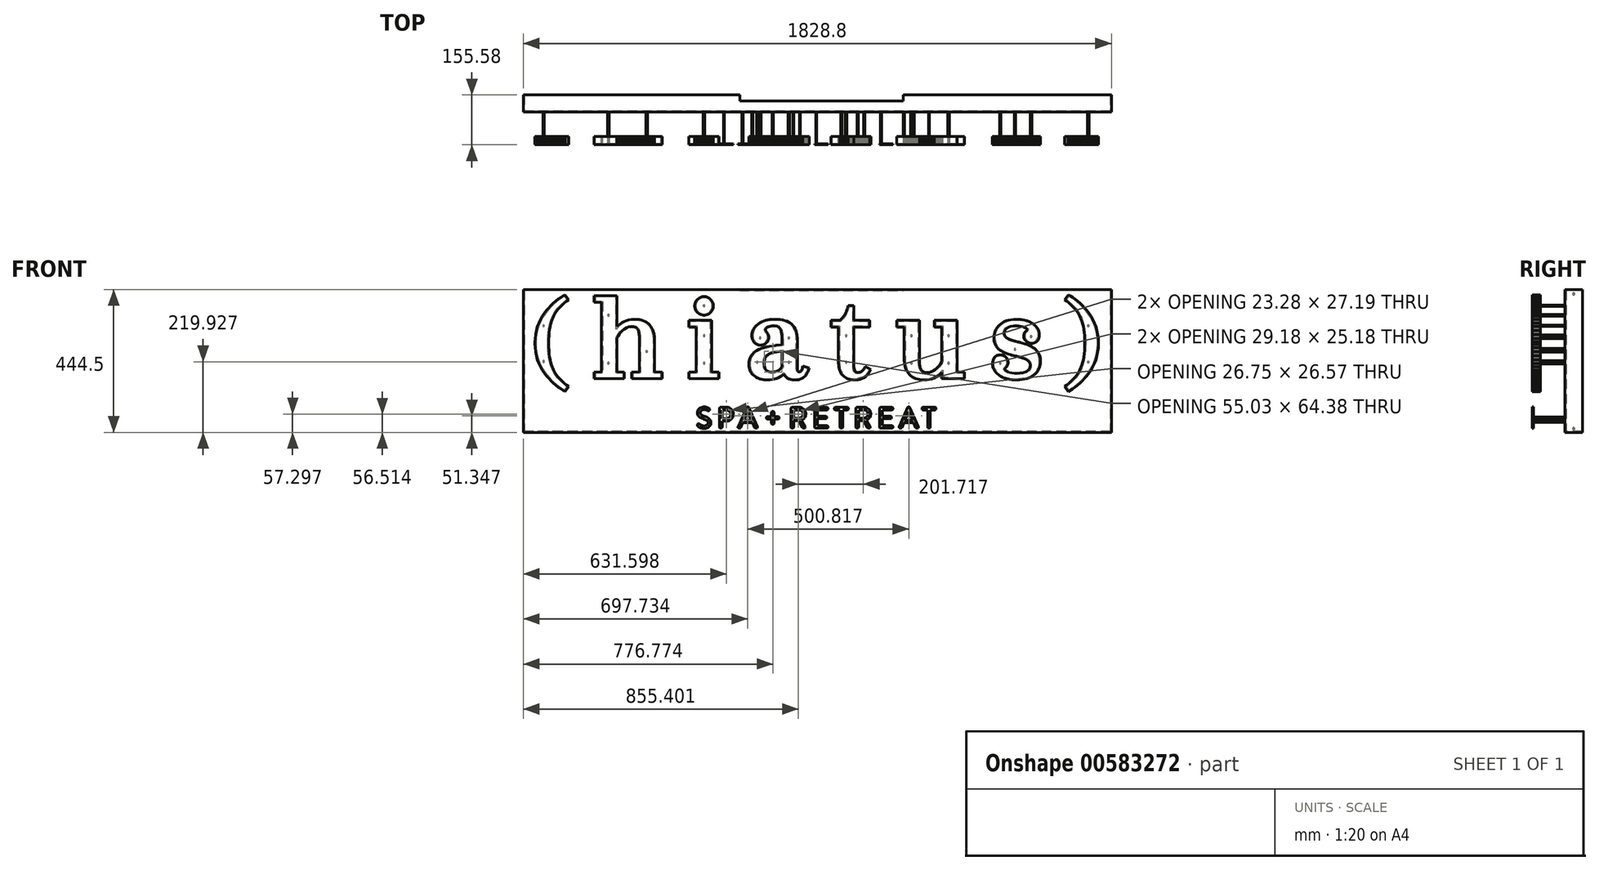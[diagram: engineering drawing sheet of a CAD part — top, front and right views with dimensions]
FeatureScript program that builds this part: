
annotation { "Feature Type Name" : "Feature", "Feature Type Description" : "" }
export const myFeature = defineFeature(function(context is Context, id is Id, definition is map)
    precondition{}
    {
        {
            var Q0;
            Q0=qCreatedBy(makeId("Front.planeOp"),FACE);
            var sketch = newSketch(context, id + "F0", { "sketchPlane" : qUnion([Q0])});
            skLineSegment(sketch, "E0", {"start": v(-821.4, -18.32) * mm, "end": v(-822.15, -16.45) * mm});
            skLineSegment(sketch, "E1", {"start": v(-822.15, -16.45) * mm, "end": v(-824.19, -10.72) * mm});
            skLineSegment(sketch, "E2", {"start": v(-824.19, -10.72) * mm, "end": v(-826.59, -2.66) * mm});
            skLineSegment(sketch, "E3", {"start": v(-826.59, -2.66) * mm, "end": v(-828.6, 5.9) * mm});
            skLineSegment(sketch, "E4", {"start": v(-828.6, 5.9) * mm, "end": v(-830.23, 14.98) * mm});
            skLineSegment(sketch, "E5", {"start": v(-830.23, 14.98) * mm, "end": v(-831.49, 24.64) * mm});
            skLineSegment(sketch, "E6", {"start": v(-831.49, 24.64) * mm, "end": v(-832.38, 34.93) * mm});
            skLineSegment(sketch, "E7", {"start": v(-832.38, 34.93) * mm, "end": v(-832.9, 45.87) * mm});
            skLineSegment(sketch, "E8", {"start": v(-832.9, 45.87) * mm, "end": v(-833.08, 54.6) * mm});
            skLineSegment(sketch, "E9", {"start": v(-833.08, 54.6) * mm, "end": v(-833.08, 57.5) * mm});
            skLineSegment(sketch, "E10", {"start": v(-833.08, 57.5) * mm, "end": v(-833.08, 60.42) * mm});
            skLineSegment(sketch, "E11", {"start": v(-833.08, 60.42) * mm, "end": v(-832.9, 69.15) * mm});
            skLineSegment(sketch, "E12", {"start": v(-832.9, 69.15) * mm, "end": v(-832.38, 80.1) * mm});
            skLineSegment(sketch, "E13", {"start": v(-832.38, 80.1) * mm, "end": v(-831.49, 90.37) * mm});
            skLineSegment(sketch, "E14", {"start": v(-831.49, 90.37) * mm, "end": v(-830.23, 100.03) * mm});
            skLineSegment(sketch, "E15", {"start": v(-830.23, 100.03) * mm, "end": v(-828.6, 109.12) * mm});
            skLineSegment(sketch, "E16", {"start": v(-828.6, 109.12) * mm, "end": v(-826.59, 117.67) * mm});
            skLineSegment(sketch, "E17", {"start": v(-826.59, 117.67) * mm, "end": v(-824.19, 125.73) * mm});
            skLineSegment(sketch, "E18", {"start": v(-824.19, 125.73) * mm, "end": v(-822.15, 131.46) * mm});
            skLineSegment(sketch, "E19", {"start": v(-822.15, 131.46) * mm, "end": v(-821.4, 133.34) * mm});
            skLineSegment(sketch, "E20", {"start": v(-821.4, 133.34) * mm, "end": v(-820.58, 135.36) * mm});
            skLineSegment(sketch, "E21", {"start": v(-820.58, 135.36) * mm, "end": v(-817.84, 141.3) * mm});
            skLineSegment(sketch, "E22", {"start": v(-817.84, 141.3) * mm, "end": v(-813.76, 148.88) * mm});
            skLineSegment(sketch, "E23", {"start": v(-813.76, 148.88) * mm, "end": v(-809.12, 156.12) * mm});
            skLineSegment(sketch, "E24", {"start": v(-809.12, 156.12) * mm, "end": v(-803.9, 163.04) * mm});
            skLineSegment(sketch, "E25", {"start": v(-803.9, 163.04) * mm, "end": v(-798.07, 169.69) * mm});
            skLineSegment(sketch, "E26", {"start": v(-798.07, 169.69) * mm, "end": v(-791.62, 176.07) * mm});
            skLineSegment(sketch, "E27", {"start": v(-791.62, 176.07) * mm, "end": v(-784.52, 182.24) * mm});
            skLineSegment(sketch, "E28", {"start": v(-784.52, 182.24) * mm, "end": v(-778.72, 186.78) * mm});
            skLineSegment(sketch, "E29", {"start": v(-778.72, 186.78) * mm, "end": v(-776.74, 188.22) * mm});
            skLineSegment(sketch, "E30", {"start": v(-776.74, 188.22) * mm, "end": v(-771.25, 192.19) * mm});
            skLineSegment(sketch, "E31", {"start": v(-771.25, 192.19) * mm, "end": v(-782.57, 208.03) * mm});
            skLineSegment(sketch, "E32", {"start": v(-782.57, 208.03) * mm, "end": v(-788, 204.63) * mm});
            skLineSegment(sketch, "E33", {"start": v(-788, 204.63) * mm, "end": v(-789.93, 203.43) * mm});
            skLineSegment(sketch, "E34", {"start": v(-789.93, 203.43) * mm, "end": v(-795.63, 199.68) * mm});
            skLineSegment(sketch, "E35", {"start": v(-795.63, 199.68) * mm, "end": v(-803.36, 194.22) * mm});
            skLineSegment(sketch, "E36", {"start": v(-803.36, 194.22) * mm, "end": v(-811.1, 188.24) * mm});
            skLineSegment(sketch, "E37", {"start": v(-811.1, 188.24) * mm, "end": v(-818.8, 181.74) * mm});
            skLineSegment(sketch, "E38", {"start": v(-818.8, 181.74) * mm, "end": v(-826.33, 174.7) * mm});
            skLineSegment(sketch, "E39", {"start": v(-826.33, 174.7) * mm, "end": v(-833.64, 167.1) * mm});
            skLineSegment(sketch, "E40", {"start": v(-833.64, 167.1) * mm, "end": v(-840.64, 158.93) * mm});
            skLineSegment(sketch, "E41", {"start": v(-840.64, 158.93) * mm, "end": v(-847.26, 150.17) * mm});
            skLineSegment(sketch, "E42", {"start": v(-847.26, 150.17) * mm, "end": v(-853.4, 140.82) * mm});
            skLineSegment(sketch, "E43", {"start": v(-853.4, 140.82) * mm, "end": v(-858.98, 130.86) * mm});
            skLineSegment(sketch, "E44", {"start": v(-858.98, 130.86) * mm, "end": v(-863.94, 120.28) * mm});
            skLineSegment(sketch, "E45", {"start": v(-863.94, 120.28) * mm, "end": v(-868.17, 109.05) * mm});
            skLineSegment(sketch, "E46", {"start": v(-868.17, 109.05) * mm, "end": v(-871.6, 97.18) * mm});
            skLineSegment(sketch, "E47", {"start": v(-871.6, 97.18) * mm, "end": v(-874.16, 84.64) * mm});
            skLineSegment(sketch, "E48", {"start": v(-874.16, 84.64) * mm, "end": v(-875.75, 71.42) * mm});
            skLineSegment(sketch, "E49", {"start": v(-875.75, 71.42) * mm, "end": v(-876.3, 60.99) * mm});
            skLineSegment(sketch, "E50", {"start": v(-876.3, 60.99) * mm, "end": v(-876.3, 57.5) * mm});
            skLineSegment(sketch, "E51", {"start": v(-876.3, 57.5) * mm, "end": v(-876.3, 54.03) * mm});
            skLineSegment(sketch, "E52", {"start": v(-876.3, 54.03) * mm, "end": v(-875.75, 43.6) * mm});
            skLineSegment(sketch, "E53", {"start": v(-875.75, 43.6) * mm, "end": v(-874.16, 30.38) * mm});
            skLineSegment(sketch, "E54", {"start": v(-874.16, 30.38) * mm, "end": v(-871.6, 17.84) * mm});
            skLineSegment(sketch, "E55", {"start": v(-871.6, 17.84) * mm, "end": v(-868.17, 5.96) * mm});
            skLineSegment(sketch, "E56", {"start": v(-868.17, 5.96) * mm, "end": v(-863.94, -5.26) * mm});
            skLineSegment(sketch, "E57", {"start": v(-863.94, -5.26) * mm, "end": v(-858.98, -15.85) * mm});
            skLineSegment(sketch, "E58", {"start": v(-858.98, -15.85) * mm, "end": v(-853.4, -25.8) * mm});
            skLineSegment(sketch, "E59", {"start": v(-853.4, -25.8) * mm, "end": v(-847.26, -35.16) * mm});
            skLineSegment(sketch, "E60", {"start": v(-847.26, -35.16) * mm, "end": v(-840.64, -43.91) * mm});
            skLineSegment(sketch, "E61", {"start": v(-840.64, -43.91) * mm, "end": v(-833.64, -52.08) * mm});
            skLineSegment(sketch, "E62", {"start": v(-833.64, -52.08) * mm, "end": v(-826.33, -59.68) * mm});
            skLineSegment(sketch, "E63", {"start": v(-826.33, -59.68) * mm, "end": v(-818.8, -66.73) * mm});
            skLineSegment(sketch, "E64", {"start": v(-818.8, -66.73) * mm, "end": v(-811.1, -73.23) * mm});
            skLineSegment(sketch, "E65", {"start": v(-811.1, -73.23) * mm, "end": v(-803.36, -79.2) * mm});
            skLineSegment(sketch, "E66", {"start": v(-803.36, -79.2) * mm, "end": v(-795.63, -84.66) * mm});
            skLineSegment(sketch, "E67", {"start": v(-795.63, -84.66) * mm, "end": v(-789.93, -88.42) * mm});
            skLineSegment(sketch, "E68", {"start": v(-789.93, -88.42) * mm, "end": v(-788, -89.62) * mm});
            skLineSegment(sketch, "E69", {"start": v(-788, -89.62) * mm, "end": v(-782.57, -93.01) * mm});
            skLineSegment(sketch, "E70", {"start": v(-782.57, -93.01) * mm, "end": v(-771.25, -77.17) * mm});
            skLineSegment(sketch, "E71", {"start": v(-771.25, -77.17) * mm, "end": v(-776.74, -73.2) * mm});
            skLineSegment(sketch, "E72", {"start": v(-776.74, -73.2) * mm, "end": v(-778.72, -71.76) * mm});
            skLineSegment(sketch, "E73", {"start": v(-778.72, -71.76) * mm, "end": v(-784.52, -67.23) * mm});
            skLineSegment(sketch, "E74", {"start": v(-784.52, -67.23) * mm, "end": v(-791.62, -61.06) * mm});
            skLineSegment(sketch, "E75", {"start": v(-791.62, -61.06) * mm, "end": v(-798.07, -54.67) * mm});
            skLineSegment(sketch, "E76", {"start": v(-798.07, -54.67) * mm, "end": v(-803.9, -48.03) * mm});
            skLineSegment(sketch, "E77", {"start": v(-803.9, -48.03) * mm, "end": v(-809.12, -41.1) * mm});
            skLineSegment(sketch, "E78", {"start": v(-809.12, -41.1) * mm, "end": v(-813.76, -33.86) * mm});
            skLineSegment(sketch, "E79", {"start": v(-813.76, -33.86) * mm, "end": v(-817.84, -26.28) * mm});
            skLineSegment(sketch, "E80", {"start": v(-817.84, -26.28) * mm, "end": v(-820.58, -20.34) * mm});
            skLineSegment(sketch, "E81", {"start": v(-820.58, -20.34) * mm, "end": v(-821.4, -18.32) * mm});
            skLineSegment(sketch, "E82", {"start": v(-503.7, 62.99) * mm, "end": v(-503.7, 65.1) * mm});
            skLineSegment(sketch, "E83", {"start": v(-503.7, 65.1) * mm, "end": v(-503.94, 71.4) * mm});
            skLineSegment(sketch, "E84", {"start": v(-503.94, 71.4) * mm, "end": v(-504.67, 79.26) * mm});
            skLineSegment(sketch, "E85", {"start": v(-504.67, 79.26) * mm, "end": v(-505.9, 86.56) * mm});
            skLineSegment(sketch, "E86", {"start": v(-505.9, 86.56) * mm, "end": v(-507.62, 93.31) * mm});
            skLineSegment(sketch, "E87", {"start": v(-507.62, 93.31) * mm, "end": v(-509.84, 99.51) * mm});
            skLineSegment(sketch, "E88", {"start": v(-509.84, 99.51) * mm, "end": v(-512.56, 105.17) * mm});
            skLineSegment(sketch, "E89", {"start": v(-512.56, 105.17) * mm, "end": v(-515.77, 110.27) * mm});
            skLineSegment(sketch, "E90", {"start": v(-515.77, 110.27) * mm, "end": v(-519.5, 114.82) * mm});
            skLineSegment(sketch, "E91", {"start": v(-519.5, 114.82) * mm, "end": v(-523.71, 118.84) * mm});
            skLineSegment(sketch, "E92", {"start": v(-523.71, 118.84) * mm, "end": v(-528.43, 122.31) * mm});
            skLineSegment(sketch, "E93", {"start": v(-528.43, 122.31) * mm, "end": v(-533.67, 125.25) * mm});
            skLineSegment(sketch, "E94", {"start": v(-533.67, 125.25) * mm, "end": v(-539.4, 127.64) * mm});
            skLineSegment(sketch, "E95", {"start": v(-539.4, 127.64) * mm, "end": v(-545.66, 129.5) * mm});
            skLineSegment(sketch, "E96", {"start": v(-545.66, 129.5) * mm, "end": v(-552.42, 130.83) * mm});
            skLineSegment(sketch, "E97", {"start": v(-552.42, 130.83) * mm, "end": v(-559.7, 131.63) * mm});
            skLineSegment(sketch, "E98", {"start": v(-559.7, 131.63) * mm, "end": v(-565.53, 131.9) * mm});
            skLineSegment(sketch, "E99", {"start": v(-565.53, 131.9) * mm, "end": v(-567.48, 131.9) * mm});
            skLineSegment(sketch, "E100", {"start": v(-567.48, 131.9) * mm, "end": v(-569.67, 131.9) * mm});
            skLineSegment(sketch, "E101", {"start": v(-569.67, 131.9) * mm, "end": v(-576.24, 131.42) * mm});
            skLineSegment(sketch, "E102", {"start": v(-576.24, 131.42) * mm, "end": v(-584.36, 130.08) * mm});
            skLineSegment(sketch, "E103", {"start": v(-584.36, 130.08) * mm, "end": v(-591.88, 127.95) * mm});
            skLineSegment(sketch, "E104", {"start": v(-591.88, 127.95) * mm, "end": v(-598.8, 125.16) * mm});
            skLineSegment(sketch, "E105", {"start": v(-598.8, 125.16) * mm, "end": v(-605.14, 121.78) * mm});
            skLineSegment(sketch, "E106", {"start": v(-605.14, 121.78) * mm, "end": v(-610.93, 117.92) * mm});
            skLineSegment(sketch, "E107", {"start": v(-610.93, 117.92) * mm, "end": v(-616.19, 113.68) * mm});
            skLineSegment(sketch, "E108", {"start": v(-616.19, 113.68) * mm, "end": v(-619.8, 110.34) * mm});
            skLineSegment(sketch, "E109", {"start": v(-619.8, 110.34) * mm, "end": v(-620.93, 109.17) * mm});
            skLineSegment(sketch, "E110", {"start": v(-620.93, 109.17) * mm, "end": v(-620.93, 204.94) * mm});
            skLineSegment(sketch, "E111", {"start": v(-620.93, 204.94) * mm, "end": v(-691.9, 204.94) * mm});
            skLineSegment(sketch, "E112", {"start": v(-691.9, 204.94) * mm, "end": v(-691.9, 184) * mm});
            skLineSegment(sketch, "E113", {"start": v(-691.9, 184) * mm, "end": v(-668.9, 184) * mm});
            skLineSegment(sketch, "E114", {"start": v(-668.9, 184) * mm, "end": v(-668.9, -32.46) * mm});
            skLineSegment(sketch, "E115", {"start": v(-668.9, -32.46) * mm, "end": v(-691.9, -32.46) * mm});
            skLineSegment(sketch, "E116", {"start": v(-691.9, -32.46) * mm, "end": v(-691.9, -53.4) * mm});
            skLineSegment(sketch, "E117", {"start": v(-691.9, -53.4) * mm, "end": v(-597.92, -53.4) * mm});
            skLineSegment(sketch, "E118", {"start": v(-597.92, -53.4) * mm, "end": v(-597.92, -32.46) * mm});
            skLineSegment(sketch, "E119", {"start": v(-597.92, -32.46) * mm, "end": v(-620.93, -32.46) * mm});
            skLineSegment(sketch, "E120", {"start": v(-620.93, -32.46) * mm, "end": v(-620.93, 73.68) * mm});
            skLineSegment(sketch, "E121", {"start": v(-620.93, 73.68) * mm, "end": v(-620.17, 75.07) * mm});
            skLineSegment(sketch, "E122", {"start": v(-620.17, 75.07) * mm, "end": v(-617.74, 79.14) * mm});
            skLineSegment(sketch, "E123", {"start": v(-617.74, 79.14) * mm, "end": v(-613.83, 84.97) * mm});
            skLineSegment(sketch, "E124", {"start": v(-613.83, 84.97) * mm, "end": v(-609.21, 90.83) * mm});
            skLineSegment(sketch, "E125", {"start": v(-609.21, 90.83) * mm, "end": v(-603.9, 96.38) * mm});
            skLineSegment(sketch, "E126", {"start": v(-603.9, 96.38) * mm, "end": v(-597.9, 101.3) * mm});
            skLineSegment(sketch, "E127", {"start": v(-597.9, 101.3) * mm, "end": v(-591.23, 105.22) * mm});
            skLineSegment(sketch, "E128", {"start": v(-591.23, 105.22) * mm, "end": v(-583.88, 107.82) * mm});
            skLineSegment(sketch, "E129", {"start": v(-583.88, 107.82) * mm, "end": v(-577.88, 108.76) * mm});
            skLineSegment(sketch, "E130", {"start": v(-577.88, 108.76) * mm, "end": v(-575.88, 108.76) * mm});
            skLineSegment(sketch, "E131", {"start": v(-575.88, 108.76) * mm, "end": v(-575.22, 108.76) * mm});
            skLineSegment(sketch, "E132", {"start": v(-575.22, 108.76) * mm, "end": v(-573.21, 108.7) * mm});
            skLineSegment(sketch, "E133", {"start": v(-573.21, 108.7) * mm, "end": v(-570.67, 108.46) * mm});
            skLineSegment(sketch, "E134", {"start": v(-570.67, 108.46) * mm, "end": v(-568.25, 108.04) * mm});
            skLineSegment(sketch, "E135", {"start": v(-568.25, 108.04) * mm, "end": v(-565.96, 107.42) * mm});
            skLineSegment(sketch, "E136", {"start": v(-565.96, 107.42) * mm, "end": v(-563.82, 106.55) * mm});
            skLineSegment(sketch, "E137", {"start": v(-563.82, 106.55) * mm, "end": v(-561.83, 105.44) * mm});
            skLineSegment(sketch, "E138", {"start": v(-561.83, 105.44) * mm, "end": v(-560, 104.04) * mm});
            skLineSegment(sketch, "E139", {"start": v(-560, 104.04) * mm, "end": v(-558.32, 102.33) * mm});
            skLineSegment(sketch, "E140", {"start": v(-558.32, 102.33) * mm, "end": v(-556.81, 100.29) * mm});
            skLineSegment(sketch, "E141", {"start": v(-556.81, 100.29) * mm, "end": v(-555.49, 97.9) * mm});
            skLineSegment(sketch, "E142", {"start": v(-555.49, 97.9) * mm, "end": v(-554.35, 95.12) * mm});
            skLineSegment(sketch, "E143", {"start": v(-554.35, 95.12) * mm, "end": v(-553.4, 91.94) * mm});
            skLineSegment(sketch, "E144", {"start": v(-553.4, 91.94) * mm, "end": v(-552.65, 88.33) * mm});
            skLineSegment(sketch, "E145", {"start": v(-552.65, 88.33) * mm, "end": v(-552.1, 84.26) * mm});
            skLineSegment(sketch, "E146", {"start": v(-552.1, 84.26) * mm, "end": v(-551.77, 79.72) * mm});
            skLineSegment(sketch, "E147", {"start": v(-551.77, 79.72) * mm, "end": v(-551.65, 75.94) * mm});
            skLineSegment(sketch, "E148", {"start": v(-551.65, 75.94) * mm, "end": v(-551.65, 74.68) * mm});
            skLineSegment(sketch, "E149", {"start": v(-551.65, 74.68) * mm, "end": v(-551.65, -32.46) * mm});
            skLineSegment(sketch, "E150", {"start": v(-551.65, -32.46) * mm, "end": v(-575.03, -32.46) * mm});
            skLineSegment(sketch, "E151", {"start": v(-575.03, -32.46) * mm, "end": v(-575.03, -53.4) * mm});
            skLineSegment(sketch, "E152", {"start": v(-575.03, -53.4) * mm, "end": v(-480.69, -53.4) * mm});
            skLineSegment(sketch, "E153", {"start": v(-480.69, -53.4) * mm, "end": v(-480.69, -32.46) * mm});
            skLineSegment(sketch, "E154", {"start": v(-480.69, -32.46) * mm, "end": v(-503.7, -32.46) * mm});
            skLineSegment(sketch, "E155", {"start": v(-503.7, -32.46) * mm, "end": v(-503.7, 62.99) * mm});
            skLineSegment(sketch, "E156", {"start": v(-326.96, 128.24) * mm, "end": v(-397.93, 128.24) * mm});
            skLineSegment(sketch, "E157", {"start": v(-397.93, 128.24) * mm, "end": v(-397.93, 107.3) * mm});
            skLineSegment(sketch, "E158", {"start": v(-397.93, 107.3) * mm, "end": v(-374.92, 107.3) * mm});
            skLineSegment(sketch, "E159", {"start": v(-374.92, 107.3) * mm, "end": v(-374.92, -32.46) * mm});
            skLineSegment(sketch, "E160", {"start": v(-374.92, -32.46) * mm, "end": v(-397.93, -32.46) * mm});
            skLineSegment(sketch, "E161", {"start": v(-397.93, -32.46) * mm, "end": v(-397.93, -53.4) * mm});
            skLineSegment(sketch, "E162", {"start": v(-397.93, -53.4) * mm, "end": v(-303.95, -53.4) * mm});
            skLineSegment(sketch, "E163", {"start": v(-303.95, -53.4) * mm, "end": v(-303.95, -32.46) * mm});
            skLineSegment(sketch, "E164", {"start": v(-303.95, -32.46) * mm, "end": v(-326.96, -32.46) * mm});
            skLineSegment(sketch, "E165", {"start": v(-326.96, -32.46) * mm, "end": v(-326.96, 128.24) * mm});
            skLineSegment(sketch, "E166", {"start": v(-349.84, 144.55) * mm, "end": v(-348.42, 144.55) * mm});
            skLineSegment(sketch, "E167", {"start": v(-348.42, 144.55) * mm, "end": v(-344.13, 145.14) * mm});
            skLineSegment(sketch, "E168", {"start": v(-344.13, 145.14) * mm, "end": v(-338.81, 146.82) * mm});
            skLineSegment(sketch, "E169", {"start": v(-338.81, 146.82) * mm, "end": v(-334, 149.47) * mm});
            skLineSegment(sketch, "E170", {"start": v(-334, 149.47) * mm, "end": v(-329.8, 152.98) * mm});
            skLineSegment(sketch, "E171", {"start": v(-329.8, 152.98) * mm, "end": v(-326.33, 157.23) * mm});
            skLineSegment(sketch, "E172", {"start": v(-326.33, 157.23) * mm, "end": v(-323.71, 162.11) * mm});
            skLineSegment(sketch, "E173", {"start": v(-323.71, 162.11) * mm, "end": v(-322.05, 167.5) * mm});
            skLineSegment(sketch, "E174", {"start": v(-322.05, 167.5) * mm, "end": v(-321.47, 171.84) * mm});
            skLineSegment(sketch, "E175", {"start": v(-321.47, 171.84) * mm, "end": v(-321.47, 173.28) * mm});
            skLineSegment(sketch, "E176", {"start": v(-321.47, 173.28) * mm, "end": v(-321.47, 174.77) * mm});
            skLineSegment(sketch, "E177", {"start": v(-321.47, 174.77) * mm, "end": v(-322.04, 179.22) * mm});
            skLineSegment(sketch, "E178", {"start": v(-322.04, 179.22) * mm, "end": v(-323.67, 184.71) * mm});
            skLineSegment(sketch, "E179", {"start": v(-323.67, 184.71) * mm, "end": v(-326.26, 189.66) * mm});
            skLineSegment(sketch, "E180", {"start": v(-326.26, 189.66) * mm, "end": v(-329.7, 193.95) * mm});
            skLineSegment(sketch, "E181", {"start": v(-329.7, 193.95) * mm, "end": v(-333.88, 197.48) * mm});
            skLineSegment(sketch, "E182", {"start": v(-333.88, 197.48) * mm, "end": v(-338.7, 200.13) * mm});
            skLineSegment(sketch, "E183", {"start": v(-338.7, 200.13) * mm, "end": v(-344.06, 201.8) * mm});
            skLineSegment(sketch, "E184", {"start": v(-344.06, 201.8) * mm, "end": v(-348.4, 202.38) * mm});
            skLineSegment(sketch, "E185", {"start": v(-348.4, 202.38) * mm, "end": v(-349.84, 202.38) * mm});
            skLineSegment(sketch, "E186", {"start": v(-349.84, 202.38) * mm, "end": v(-351.32, 202.38) * mm});
            skLineSegment(sketch, "E187", {"start": v(-351.32, 202.38) * mm, "end": v(-355.77, 201.8) * mm});
            skLineSegment(sketch, "E188", {"start": v(-355.77, 201.8) * mm, "end": v(-361.3, 200.1) * mm});
            skLineSegment(sketch, "E189", {"start": v(-361.3, 200.1) * mm, "end": v(-366.3, 197.4) * mm});
            skLineSegment(sketch, "E190", {"start": v(-366.3, 197.4) * mm, "end": v(-370.66, 193.85) * mm});
            skLineSegment(sketch, "E191", {"start": v(-370.66, 193.85) * mm, "end": v(-374.26, 189.54) * mm});
            skLineSegment(sketch, "E192", {"start": v(-374.26, 189.54) * mm, "end": v(-376.98, 184.6) * mm});
            skLineSegment(sketch, "E193", {"start": v(-376.98, 184.6) * mm, "end": v(-378.7, 179.14) * mm});
            skLineSegment(sketch, "E194", {"start": v(-378.7, 179.14) * mm, "end": v(-379.3, 174.75) * mm});
            skLineSegment(sketch, "E195", {"start": v(-379.3, 174.75) * mm, "end": v(-379.3, 173.28) * mm});
            skLineSegment(sketch, "E196", {"start": v(-379.3, 173.28) * mm, "end": v(-379.3, 171.84) * mm});
            skLineSegment(sketch, "E197", {"start": v(-379.3, 171.84) * mm, "end": v(-378.7, 167.5) * mm});
            skLineSegment(sketch, "E198", {"start": v(-378.7, 167.5) * mm, "end": v(-376.98, 162.11) * mm});
            skLineSegment(sketch, "E199", {"start": v(-376.98, 162.11) * mm, "end": v(-374.26, 157.23) * mm});
            skLineSegment(sketch, "E200", {"start": v(-374.26, 157.23) * mm, "end": v(-370.66, 152.98) * mm});
            skLineSegment(sketch, "E201", {"start": v(-370.66, 152.98) * mm, "end": v(-366.3, 149.47) * mm});
            skLineSegment(sketch, "E202", {"start": v(-366.3, 149.47) * mm, "end": v(-361.3, 146.82) * mm});
            skLineSegment(sketch, "E203", {"start": v(-361.3, 146.82) * mm, "end": v(-355.77, 145.14) * mm});
            skLineSegment(sketch, "E204", {"start": v(-355.77, 145.14) * mm, "end": v(-351.32, 144.55) * mm});
            skLineSegment(sketch, "E205", {"start": v(-351.32, 144.55) * mm, "end": v(-349.84, 144.55) * mm});
            skLineSegment(sketch, "E206", {"start": v(-107.97, -16.47) * mm, "end": v(-108.92, -17.64) * mm});
            skLineSegment(sketch, "E207", {"start": v(-108.92, -17.64) * mm, "end": v(-112.02, -20.94) * mm});
            skLineSegment(sketch, "E208", {"start": v(-112.02, -20.94) * mm, "end": v(-116.09, -24.52) * mm});
            skLineSegment(sketch, "E209", {"start": v(-116.09, -24.52) * mm, "end": v(-120.12, -27.31) * mm});
            skLineSegment(sketch, "E210", {"start": v(-120.12, -27.31) * mm, "end": v(-124.07, -29.4) * mm});
            skLineSegment(sketch, "E211", {"start": v(-124.07, -29.4) * mm, "end": v(-127.9, -30.87) * mm});
            skLineSegment(sketch, "E212", {"start": v(-127.9, -30.87) * mm, "end": v(-131.53, -31.82) * mm});
            skLineSegment(sketch, "E213", {"start": v(-131.53, -31.82) * mm, "end": v(-134.92, -32.32) * mm});
            skLineSegment(sketch, "E214", {"start": v(-134.92, -32.32) * mm, "end": v(-137.26, -32.46) * mm});
            skLineSegment(sketch, "E215", {"start": v(-137.26, -32.46) * mm, "end": v(-138.04, -32.46) * mm});
            skLineSegment(sketch, "E216", {"start": v(-138.04, -32.46) * mm, "end": v(-139.55, -32.46) * mm});
            skLineSegment(sketch, "E217", {"start": v(-139.55, -32.46) * mm, "end": v(-144.07, -32.07) * mm});
            skLineSegment(sketch, "E218", {"start": v(-144.07, -32.07) * mm, "end": v(-149.22, -30.86) * mm});
            skLineSegment(sketch, "E219", {"start": v(-149.22, -30.86) * mm, "end": v(-153.52, -28.82) * mm});
            skLineSegment(sketch, "E220", {"start": v(-153.52, -28.82) * mm, "end": v(-157, -25.93) * mm});
            skLineSegment(sketch, "E221", {"start": v(-157, -25.93) * mm, "end": v(-159.66, -22.15) * mm});
            skLineSegment(sketch, "E222", {"start": v(-159.66, -22.15) * mm, "end": v(-161.53, -17.48) * mm});
            skLineSegment(sketch, "E223", {"start": v(-161.53, -17.48) * mm, "end": v(-162.64, -11.87) * mm});
            skLineSegment(sketch, "E224", {"start": v(-162.64, -11.87) * mm, "end": v(-163, -6.95) * mm});
            skLineSegment(sketch, "E225", {"start": v(-163, -6.95) * mm, "end": v(-163, -5.31) * mm});
            skLineSegment(sketch, "E226", {"start": v(-163, -5.31) * mm, "end": v(-163, -4.3) * mm});
            skLineSegment(sketch, "E227", {"start": v(-163, -4.3) * mm, "end": v(-162.87, -1.28) * mm});
            skLineSegment(sketch, "E228", {"start": v(-162.87, -1.28) * mm, "end": v(-162.5, 2.46) * mm});
            skLineSegment(sketch, "E229", {"start": v(-162.5, 2.46) * mm, "end": v(-161.85, 5.92) * mm});
            skLineSegment(sketch, "E230", {"start": v(-161.85, 5.92) * mm, "end": v(-160.93, 9.1) * mm});
            skLineSegment(sketch, "E231", {"start": v(-160.93, 9.1) * mm, "end": v(-159.72, 12.04) * mm});
            skLineSegment(sketch, "E232", {"start": v(-159.72, 12.04) * mm, "end": v(-158.2, 14.72) * mm});
            skLineSegment(sketch, "E233", {"start": v(-158.2, 14.72) * mm, "end": v(-156.4, 17.16) * mm});
            skLineSegment(sketch, "E234", {"start": v(-156.4, 17.16) * mm, "end": v(-154.26, 19.37) * mm});
            skLineSegment(sketch, "E235", {"start": v(-154.26, 19.37) * mm, "end": v(-151.8, 21.36) * mm});
            skLineSegment(sketch, "E236", {"start": v(-151.8, 21.36) * mm, "end": v(-149, 23.14) * mm});
            skLineSegment(sketch, "E237", {"start": v(-149, 23.14) * mm, "end": v(-145.84, 24.72) * mm});
            skLineSegment(sketch, "E238", {"start": v(-145.84, 24.72) * mm, "end": v(-142.32, 26.1) * mm});
            skLineSegment(sketch, "E239", {"start": v(-142.32, 26.1) * mm, "end": v(-138.43, 27.31) * mm});
            skLineSegment(sketch, "E240", {"start": v(-138.43, 27.31) * mm, "end": v(-134.17, 28.34) * mm});
            skLineSegment(sketch, "E241", {"start": v(-134.17, 28.34) * mm, "end": v(-129.5, 29.2) * mm});
            skLineSegment(sketch, "E242", {"start": v(-129.5, 29.2) * mm, "end": v(-125.7, 29.77) * mm});
            skLineSegment(sketch, "E243", {"start": v(-125.7, 29.77) * mm, "end": v(-124.44, 29.92) * mm});
            skLineSegment(sketch, "E244", {"start": v(-124.44, 29.92) * mm, "end": v(-107.97, 31.92) * mm});
            skLineSegment(sketch, "E245", {"start": v(-107.97, 31.92) * mm, "end": v(-107.97, -16.47) * mm});
            skLineSegment(sketch, "E246", {"start": v(-44.83, -20.02) * mm, "end": v(-45.13, -20.97) * mm});
            skLineSegment(sketch, "E247", {"start": v(-45.13, -20.97) * mm, "end": v(-46.21, -23.76) * mm});
            skLineSegment(sketch, "E248", {"start": v(-46.21, -23.76) * mm, "end": v(-47.6, -26.58) * mm});
            skLineSegment(sketch, "E249", {"start": v(-47.6, -26.58) * mm, "end": v(-48.96, -28.6) * mm});
            skLineSegment(sketch, "E250", {"start": v(-48.96, -28.6) * mm, "end": v(-50.27, -29.95) * mm});
            skLineSegment(sketch, "E251", {"start": v(-50.27, -29.95) * mm, "end": v(-51.5, -30.77) * mm});
            skLineSegment(sketch, "E252", {"start": v(-51.5, -30.77) * mm, "end": v(-52.62, -31.19) * mm});
            skLineSegment(sketch, "E253", {"start": v(-52.62, -31.19) * mm, "end": v(-53.6, -31.34) * mm});
            skLineSegment(sketch, "E254", {"start": v(-53.6, -31.34) * mm, "end": v(-54.2, -31.37) * mm});
            skLineSegment(sketch, "E255", {"start": v(-54.2, -31.37) * mm, "end": v(-54.41, -31.37) * mm});
            skLineSegment(sketch, "E256", {"start": v(-54.41, -31.37) * mm, "end": v(-54.79, -31.37) * mm});
            skLineSegment(sketch, "E257", {"start": v(-54.79, -31.37) * mm, "end": v(-55.9, -31.22) * mm});
            skLineSegment(sketch, "E258", {"start": v(-55.9, -31.22) * mm, "end": v(-56.9, -30.84) * mm});
            skLineSegment(sketch, "E259", {"start": v(-56.9, -30.84) * mm, "end": v(-57.57, -30.27) * mm});
            skLineSegment(sketch, "E260", {"start": v(-57.57, -30.27) * mm, "end": v(-57.93, -29.77) * mm});
            skLineSegment(sketch, "E261", {"start": v(-57.93, -29.77) * mm, "end": v(-58.04, -29.59) * mm});
            skLineSegment(sketch, "E262", {"start": v(-58.04, -29.59) * mm, "end": v(-58.25, -29.24) * mm});
            skLineSegment(sketch, "E263", {"start": v(-58.25, -29.24) * mm, "end": v(-58.72, -28.1) * mm});
            skLineSegment(sketch, "E264", {"start": v(-58.72, -28.1) * mm, "end": v(-59.36, -25.81) * mm});
            skLineSegment(sketch, "E265", {"start": v(-59.36, -25.81) * mm, "end": v(-59.82, -22.53) * mm});
            skLineSegment(sketch, "E266", {"start": v(-59.82, -22.53) * mm, "end": v(-60, -19.2) * mm});
            skLineSegment(sketch, "E267", {"start": v(-60, -19.2) * mm, "end": v(-60, -18.1) * mm});
            skLineSegment(sketch, "E268", {"start": v(-60, -18.1) * mm, "end": v(-60, 65.18) * mm});
            skLineSegment(sketch, "E269", {"start": v(-60, 65.18) * mm, "end": v(-60, 67.3) * mm});
            skLineSegment(sketch, "E270", {"start": v(-60, 67.3) * mm, "end": v(-60.26, 73.7) * mm});
            skLineSegment(sketch, "E271", {"start": v(-60.26, 73.7) * mm, "end": v(-61.02, 81.53) * mm});
            skLineSegment(sketch, "E272", {"start": v(-61.02, 81.53) * mm, "end": v(-62.3, 88.7) * mm});
            skLineSegment(sketch, "E273", {"start": v(-62.3, 88.7) * mm, "end": v(-64.11, 95.27) * mm});
            skLineSegment(sketch, "E274", {"start": v(-64.11, 95.27) * mm, "end": v(-66.46, 101.23) * mm});
            skLineSegment(sketch, "E275", {"start": v(-66.46, 101.23) * mm, "end": v(-69.35, 106.62) * mm});
            skLineSegment(sketch, "E276", {"start": v(-69.35, 106.62) * mm, "end": v(-72.8, 111.48) * mm});
            skLineSegment(sketch, "E277", {"start": v(-72.8, 111.48) * mm, "end": v(-75.76, 114.8) * mm});
            skLineSegment(sketch, "E278", {"start": v(-75.76, 114.8) * mm, "end": v(-76.82, 115.82) * mm});
            skLineSegment(sketch, "E279", {"start": v(-76.82, 115.82) * mm, "end": v(-77.9, 116.84) * mm});
            skLineSegment(sketch, "E280", {"start": v(-77.9, 116.84) * mm, "end": v(-81.42, 119.66) * mm});
            skLineSegment(sketch, "E281", {"start": v(-81.42, 119.66) * mm, "end": v(-86.56, 122.95) * mm});
            skLineSegment(sketch, "E282", {"start": v(-86.56, 122.95) * mm, "end": v(-92.3, 125.72) * mm});
            skLineSegment(sketch, "E283", {"start": v(-92.3, 125.72) * mm, "end": v(-98.64, 127.96) * mm});
            skLineSegment(sketch, "E284", {"start": v(-98.64, 127.96) * mm, "end": v(-105.62, 129.7) * mm});
            skLineSegment(sketch, "E285", {"start": v(-105.62, 129.7) * mm, "end": v(-113.28, 130.92) * mm});
            skLineSegment(sketch, "E286", {"start": v(-113.28, 130.92) * mm, "end": v(-121.64, 131.65) * mm});
            skLineSegment(sketch, "E287", {"start": v(-121.64, 131.65) * mm, "end": v(-128.47, 131.9) * mm});
            skLineSegment(sketch, "E288", {"start": v(-128.47, 131.9) * mm, "end": v(-130.74, 131.9) * mm});
            skLineSegment(sketch, "E289", {"start": v(-130.74, 131.9) * mm, "end": v(-132.65, 131.9) * mm});
            skLineSegment(sketch, "E290", {"start": v(-132.65, 131.9) * mm, "end": v(-138.37, 131.65) * mm});
            skLineSegment(sketch, "E291", {"start": v(-138.37, 131.65) * mm, "end": v(-145.7, 130.94) * mm});
            skLineSegment(sketch, "E292", {"start": v(-145.7, 130.94) * mm, "end": v(-152.71, 129.76) * mm});
            skLineSegment(sketch, "E293", {"start": v(-152.71, 129.76) * mm, "end": v(-159.38, 128.11) * mm});
            skLineSegment(sketch, "E294", {"start": v(-159.38, 128.11) * mm, "end": v(-165.68, 126.02) * mm});
            skLineSegment(sketch, "E295", {"start": v(-165.68, 126.02) * mm, "end": v(-171.6, 123.47) * mm});
            skLineSegment(sketch, "E296", {"start": v(-171.6, 123.47) * mm, "end": v(-177.1, 120.48) * mm});
            skLineSegment(sketch, "E297", {"start": v(-177.1, 120.48) * mm, "end": v(-180.95, 117.98) * mm});
            skLineSegment(sketch, "E298", {"start": v(-180.95, 117.98) * mm, "end": v(-182.17, 117.06) * mm});
            skLineSegment(sketch, "E299", {"start": v(-182.17, 117.06) * mm, "end": v(-183.33, 116.18) * mm});
            skLineSegment(sketch, "E300", {"start": v(-183.33, 116.18) * mm, "end": v(-186.66, 113.32) * mm});
            skLineSegment(sketch, "E301", {"start": v(-186.66, 113.32) * mm, "end": v(-190.6, 109.26) * mm});
            skLineSegment(sketch, "E302", {"start": v(-190.6, 109.26) * mm, "end": v(-193.96, 104.9) * mm});
            skLineSegment(sketch, "E303", {"start": v(-193.96, 104.9) * mm, "end": v(-196.75, 100.3) * mm});
            skLineSegment(sketch, "E304", {"start": v(-196.75, 100.3) * mm, "end": v(-198.95, 95.45) * mm});
            skLineSegment(sketch, "E305", {"start": v(-198.95, 95.45) * mm, "end": v(-200.54, 90.4) * mm});
            skLineSegment(sketch, "E306", {"start": v(-200.54, 90.4) * mm, "end": v(-201.5, 85.17) * mm});
            skLineSegment(sketch, "E307", {"start": v(-201.5, 85.17) * mm, "end": v(-201.83, 81.13) * mm});
            skLineSegment(sketch, "E308", {"start": v(-201.83, 81.13) * mm, "end": v(-201.83, 79.79) * mm});
            skLineSegment(sketch, "E309", {"start": v(-201.83, 79.79) * mm, "end": v(-201.83, 78.3) * mm});
            skLineSegment(sketch, "E310", {"start": v(-201.83, 78.3) * mm, "end": v(-201.3, 73.85) * mm});
            skLineSegment(sketch, "E311", {"start": v(-201.3, 73.85) * mm, "end": v(-199.8, 68.39) * mm});
            skLineSegment(sketch, "E312", {"start": v(-199.8, 68.39) * mm, "end": v(-197.42, 63.5) * mm});
            skLineSegment(sketch, "E313", {"start": v(-197.42, 63.5) * mm, "end": v(-194.24, 59.28) * mm});
            skLineSegment(sketch, "E314", {"start": v(-194.24, 59.28) * mm, "end": v(-190.34, 55.83) * mm});
            skLineSegment(sketch, "E315", {"start": v(-190.34, 55.83) * mm, "end": v(-185.82, 53.24) * mm});
            skLineSegment(sketch, "E316", {"start": v(-185.82, 53.24) * mm, "end": v(-180.78, 51.62) * mm});
            skLineSegment(sketch, "E317", {"start": v(-180.78, 51.62) * mm, "end": v(-176.66, 51.06) * mm});
            skLineSegment(sketch, "E318", {"start": v(-176.66, 51.06) * mm, "end": v(-175.3, 51.06) * mm});
            skLineSegment(sketch, "E319", {"start": v(-175.3, 51.06) * mm, "end": v(-173.9, 51.06) * mm});
            skLineSegment(sketch, "E320", {"start": v(-173.9, 51.06) * mm, "end": v(-169.74, 51.55) * mm});
            skLineSegment(sketch, "E321", {"start": v(-169.74, 51.55) * mm, "end": v(-164.66, 52.96) * mm});
            skLineSegment(sketch, "E322", {"start": v(-164.66, 52.96) * mm, "end": v(-160.14, 55.22) * mm});
            skLineSegment(sketch, "E323", {"start": v(-160.14, 55.22) * mm, "end": v(-156.26, 58.25) * mm});
            skLineSegment(sketch, "E324", {"start": v(-156.26, 58.25) * mm, "end": v(-153.1, 61.97) * mm});
            skLineSegment(sketch, "E325", {"start": v(-153.1, 61.97) * mm, "end": v(-150.73, 66.3) * mm});
            skLineSegment(sketch, "E326", {"start": v(-150.73, 66.3) * mm, "end": v(-149.26, 71.17) * mm});
            skLineSegment(sketch, "E327", {"start": v(-149.26, 71.17) * mm, "end": v(-148.75, 75.17) * mm});
            skLineSegment(sketch, "E328", {"start": v(-148.75, 75.17) * mm, "end": v(-148.75, 76.5) * mm});
            skLineSegment(sketch, "E329", {"start": v(-148.75, 76.5) * mm, "end": v(-148.75, 77.73) * mm});
            skLineSegment(sketch, "E330", {"start": v(-148.75, 77.73) * mm, "end": v(-149.4, 81.43) * mm});
            skLineSegment(sketch, "E331", {"start": v(-149.4, 81.43) * mm, "end": v(-151, 85.57) * mm});
            skLineSegment(sketch, "E332", {"start": v(-151, 85.57) * mm, "end": v(-153.15, 89.02) * mm});
            skLineSegment(sketch, "E333", {"start": v(-153.15, 89.02) * mm, "end": v(-154.8, 91.2) * mm});
            skLineSegment(sketch, "E334", {"start": v(-154.8, 91.2) * mm, "end": v(-155.36, 91.9) * mm});
            skLineSegment(sketch, "E335", {"start": v(-155.36, 91.9) * mm, "end": v(-155.76, 92.4) * mm});
            skLineSegment(sketch, "E336", {"start": v(-155.76, 92.4) * mm, "end": v(-156.93, 93.91) * mm});
            skLineSegment(sketch, "E337", {"start": v(-156.93, 93.91) * mm, "end": v(-158.06, 95.6) * mm});
            skLineSegment(sketch, "E338", {"start": v(-158.06, 95.6) * mm, "end": v(-158.75, 97.17) * mm});
            skLineSegment(sketch, "E339", {"start": v(-158.75, 97.17) * mm, "end": v(-158.98, 98.38) * mm});
            skLineSegment(sketch, "E340", {"start": v(-158.98, 98.38) * mm, "end": v(-158.98, 98.78) * mm});
            skLineSegment(sketch, "E341", {"start": v(-158.98, 98.78) * mm, "end": v(-158.98, 99.43) * mm});
            skLineSegment(sketch, "E342", {"start": v(-158.98, 99.43) * mm, "end": v(-158.51, 101.36) * mm});
            skLineSegment(sketch, "E343", {"start": v(-158.51, 101.36) * mm, "end": v(-157.15, 103.7) * mm});
            skLineSegment(sketch, "E344", {"start": v(-157.15, 103.7) * mm, "end": v(-154.96, 105.78) * mm});
            skLineSegment(sketch, "E345", {"start": v(-154.96, 105.78) * mm, "end": v(-152.01, 107.56) * mm});
            skLineSegment(sketch, "E346", {"start": v(-152.01, 107.56) * mm, "end": v(-148.38, 109) * mm});
            skLineSegment(sketch, "E347", {"start": v(-148.38, 109) * mm, "end": v(-144.12, 110.06) * mm});
            skLineSegment(sketch, "E348", {"start": v(-144.12, 110.06) * mm, "end": v(-139.31, 110.73) * mm});
            skLineSegment(sketch, "E349", {"start": v(-139.31, 110.73) * mm, "end": v(-135.35, 110.95) * mm});
            skLineSegment(sketch, "E350", {"start": v(-135.35, 110.95) * mm, "end": v(-134.02, 110.95) * mm});
            skLineSegment(sketch, "E351", {"start": v(-134.02, 110.95) * mm, "end": v(-133.34, 110.95) * mm});
            skLineSegment(sketch, "E352", {"start": v(-133.34, 110.95) * mm, "end": v(-131.3, 110.9) * mm});
            skLineSegment(sketch, "E353", {"start": v(-131.3, 110.9) * mm, "end": v(-128.67, 110.74) * mm});
            skLineSegment(sketch, "E354", {"start": v(-128.67, 110.74) * mm, "end": v(-126.14, 110.4) * mm});
            skLineSegment(sketch, "E355", {"start": v(-126.14, 110.4) * mm, "end": v(-123.73, 109.83) * mm});
            skLineSegment(sketch, "E356", {"start": v(-123.73, 109.83) * mm, "end": v(-121.44, 109) * mm});
            skLineSegment(sketch, "E357", {"start": v(-121.44, 109) * mm, "end": v(-119.3, 107.84) * mm});
            skLineSegment(sketch, "E358", {"start": v(-119.3, 107.84) * mm, "end": v(-117.3, 106.3) * mm});
            skLineSegment(sketch, "E359", {"start": v(-117.3, 106.3) * mm, "end": v(-115.46, 104.36) * mm});
            skLineSegment(sketch, "E360", {"start": v(-115.46, 104.36) * mm, "end": v(-113.8, 101.94) * mm});
            skLineSegment(sketch, "E361", {"start": v(-113.8, 101.94) * mm, "end": v(-112.32, 99) * mm});
            skLineSegment(sketch, "E362", {"start": v(-112.32, 99) * mm, "end": v(-111.04, 95.5) * mm});
            skLineSegment(sketch, "E363", {"start": v(-111.04, 95.5) * mm, "end": v(-109.97, 91.38) * mm});
            skLineSegment(sketch, "E364", {"start": v(-109.97, 91.38) * mm, "end": v(-109.11, 86.6) * mm});
            skLineSegment(sketch, "E365", {"start": v(-109.11, 86.6) * mm, "end": v(-108.49, 81.09) * mm});
            skLineSegment(sketch, "E366", {"start": v(-108.49, 81.09) * mm, "end": v(-108.1, 74.82) * mm});
            skLineSegment(sketch, "E367", {"start": v(-108.1, 74.82) * mm, "end": v(-107.97, 69.5) * mm});
            skLineSegment(sketch, "E368", {"start": v(-107.97, 69.5) * mm, "end": v(-107.97, 67.74) * mm});
            skLineSegment(sketch, "E369", {"start": v(-107.97, 67.74) * mm, "end": v(-107.97, 52.96) * mm});
            skLineSegment(sketch, "E370", {"start": v(-107.97, 52.96) * mm, "end": v(-126.05, 50.76) * mm});
            skLineSegment(sketch, "E371", {"start": v(-126.05, 50.76) * mm, "end": v(-128.76, 50.45) * mm});
            skLineSegment(sketch, "E372", {"start": v(-128.76, 50.45) * mm, "end": v(-136.9, 49.33) * mm});
            skLineSegment(sketch, "E373", {"start": v(-136.9, 49.33) * mm, "end": v(-146.92, 47.65) * mm});
            skLineSegment(sketch, "E374", {"start": v(-146.92, 47.65) * mm, "end": v(-156.15, 45.7) * mm});
            skLineSegment(sketch, "E375", {"start": v(-156.15, 45.7) * mm, "end": v(-164.6, 43.49) * mm});
            skLineSegment(sketch, "E376", {"start": v(-164.6, 43.49) * mm, "end": v(-172.27, 40.99) * mm});
            skLineSegment(sketch, "E377", {"start": v(-172.27, 40.99) * mm, "end": v(-179.19, 38.2) * mm});
            skLineSegment(sketch, "E378", {"start": v(-179.19, 38.2) * mm, "end": v(-185.37, 35.08) * mm});
            skLineSegment(sketch, "E379", {"start": v(-185.37, 35.08) * mm, "end": v(-190.84, 31.66) * mm});
            skLineSegment(sketch, "E380", {"start": v(-190.84, 31.66) * mm, "end": v(-195.6, 27.9) * mm});
            skLineSegment(sketch, "E381", {"start": v(-195.6, 27.9) * mm, "end": v(-199.68, 23.8) * mm});
            skLineSegment(sketch, "E382", {"start": v(-199.68, 23.8) * mm, "end": v(-203.08, 19.35) * mm});
            skLineSegment(sketch, "E383", {"start": v(-203.08, 19.35) * mm, "end": v(-205.83, 14.54) * mm});
            skLineSegment(sketch, "E384", {"start": v(-205.83, 14.54) * mm, "end": v(-207.94, 9.35) * mm});
            skLineSegment(sketch, "E385", {"start": v(-207.94, 9.35) * mm, "end": v(-209.43, 3.77) * mm});
            skLineSegment(sketch, "E386", {"start": v(-209.43, 3.77) * mm, "end": v(-210.3, -2.2) * mm});
            skLineSegment(sketch, "E387", {"start": v(-210.3, -2.2) * mm, "end": v(-210.6, -7) * mm});
            skLineSegment(sketch, "E388", {"start": v(-210.6, -7) * mm, "end": v(-210.6, -8.6) * mm});
            skLineSegment(sketch, "E389", {"start": v(-210.6, -8.6) * mm, "end": v(-210.6, -9.98) * mm});
            skLineSegment(sketch, "E390", {"start": v(-210.6, -9.98) * mm, "end": v(-210.33, -14.14) * mm});
            skLineSegment(sketch, "E391", {"start": v(-210.33, -14.14) * mm, "end": v(-209.57, -19.4) * mm});
            skLineSegment(sketch, "E392", {"start": v(-209.57, -19.4) * mm, "end": v(-208.3, -24.34) * mm});
            skLineSegment(sketch, "E393", {"start": v(-208.3, -24.34) * mm, "end": v(-206.54, -28.97) * mm});
            skLineSegment(sketch, "E394", {"start": v(-206.54, -28.97) * mm, "end": v(-204.3, -33.28) * mm});
            skLineSegment(sketch, "E395", {"start": v(-204.3, -33.28) * mm, "end": v(-201.6, -37.26) * mm});
            skLineSegment(sketch, "E396", {"start": v(-201.6, -37.26) * mm, "end": v(-198.45, -40.9) * mm});
            skLineSegment(sketch, "E397", {"start": v(-198.45, -40.9) * mm, "end": v(-194.84, -44.2) * mm});
            skLineSegment(sketch, "E398", {"start": v(-194.84, -44.2) * mm, "end": v(-190.8, -47.14) * mm});
            skLineSegment(sketch, "E399", {"start": v(-190.8, -47.14) * mm, "end": v(-186.33, -49.72) * mm});
            skLineSegment(sketch, "E400", {"start": v(-186.33, -49.72) * mm, "end": v(-181.45, -51.93) * mm});
            skLineSegment(sketch, "E401", {"start": v(-181.45, -51.93) * mm, "end": v(-176.17, -53.75) * mm});
            skLineSegment(sketch, "E402", {"start": v(-176.17, -53.75) * mm, "end": v(-170.48, -55.18) * mm});
            skLineSegment(sketch, "E403", {"start": v(-170.48, -55.18) * mm, "end": v(-164.42, -56.22) * mm});
            skLineSegment(sketch, "E404", {"start": v(-164.42, -56.22) * mm, "end": v(-157.99, -56.84) * mm});
            skLineSegment(sketch, "E405", {"start": v(-157.99, -56.84) * mm, "end": v(-152.89, -57.05) * mm});
            skLineSegment(sketch, "E406", {"start": v(-152.89, -57.05) * mm, "end": v(-151.19, -57.05) * mm});
            skLineSegment(sketch, "E407", {"start": v(-151.19, -57.05) * mm, "end": v(-149.46, -57.05) * mm});
            skLineSegment(sketch, "E408", {"start": v(-149.46, -57.05) * mm, "end": v(-144.28, -56.78) * mm});
            skLineSegment(sketch, "E409", {"start": v(-144.28, -56.78) * mm, "end": v(-137.6, -55.94) * mm});
            skLineSegment(sketch, "E410", {"start": v(-137.6, -55.94) * mm, "end": v(-131.15, -54.56) * mm});
            skLineSegment(sketch, "E411", {"start": v(-131.15, -54.56) * mm, "end": v(-124.93, -52.62) * mm});
            skLineSegment(sketch, "E412", {"start": v(-124.93, -52.62) * mm, "end": v(-118.94, -50.14) * mm});
            skLineSegment(sketch, "E413", {"start": v(-118.94, -50.14) * mm, "end": v(-113.2, -47.1) * mm});
            skLineSegment(sketch, "E414", {"start": v(-113.2, -47.1) * mm, "end": v(-107.68, -43.52) * mm});
            skLineSegment(sketch, "E415", {"start": v(-107.68, -43.52) * mm, "end": v(-103.7, -40.48) * mm});
            skLineSegment(sketch, "E416", {"start": v(-103.7, -40.48) * mm, "end": v(-102.42, -39.4) * mm});
            skLineSegment(sketch, "E417", {"start": v(-102.42, -39.4) * mm, "end": v(-101.72, -40.67) * mm});
            skLineSegment(sketch, "E418", {"start": v(-101.72, -40.67) * mm, "end": v(-99.16, -44.26) * mm});
            skLineSegment(sketch, "E419", {"start": v(-99.16, -44.26) * mm, "end": v(-95.34, -48.2) * mm});
            skLineSegment(sketch, "E420", {"start": v(-95.34, -48.2) * mm, "end": v(-91.08, -51.27) * mm});
            skLineSegment(sketch, "E421", {"start": v(-91.08, -51.27) * mm, "end": v(-86.5, -53.6) * mm});
            skLineSegment(sketch, "E422", {"start": v(-86.5, -53.6) * mm, "end": v(-81.7, -55.24) * mm});
            skLineSegment(sketch, "E423", {"start": v(-81.7, -55.24) * mm, "end": v(-76.8, -56.3) * mm});
            skLineSegment(sketch, "E424", {"start": v(-76.8, -56.3) * mm, "end": v(-71.93, -56.88) * mm});
            skLineSegment(sketch, "E425", {"start": v(-71.93, -56.88) * mm, "end": v(-68.37, -57.05) * mm});
            skLineSegment(sketch, "E426", {"start": v(-68.37, -57.05) * mm, "end": v(-67.19, -57.05) * mm});
            skLineSegment(sketch, "E427", {"start": v(-67.19, -57.05) * mm, "end": v(-66.54, -57.05) * mm});
            skLineSegment(sketch, "E428", {"start": v(-66.54, -57.05) * mm, "end": v(-64.59, -57.01) * mm});
            skLineSegment(sketch, "E429", {"start": v(-64.59, -57.01) * mm, "end": v(-61.88, -56.86) * mm});
            skLineSegment(sketch, "E430", {"start": v(-61.88, -56.86) * mm, "end": v(-59.1, -56.58) * mm});
            skLineSegment(sketch, "E431", {"start": v(-59.1, -56.58) * mm, "end": v(-56.23, -56.13) * mm});
            skLineSegment(sketch, "E432", {"start": v(-56.23, -56.13) * mm, "end": v(-53.33, -55.49) * mm});
            skLineSegment(sketch, "E433", {"start": v(-53.33, -55.49) * mm, "end": v(-50.41, -54.61) * mm});
            skLineSegment(sketch, "E434", {"start": v(-50.41, -54.61) * mm, "end": v(-47.5, -53.48) * mm});
            skLineSegment(sketch, "E435", {"start": v(-47.5, -53.48) * mm, "end": v(-44.6, -52.06) * mm});
            skLineSegment(sketch, "E436", {"start": v(-44.6, -52.06) * mm, "end": v(-41.75, -50.31) * mm});
            skLineSegment(sketch, "E437", {"start": v(-41.75, -50.31) * mm, "end": v(-38.97, -48.22) * mm});
            skLineSegment(sketch, "E438", {"start": v(-38.97, -48.22) * mm, "end": v(-36.28, -45.74) * mm});
            skLineSegment(sketch, "E439", {"start": v(-36.28, -45.74) * mm, "end": v(-33.7, -42.85) * mm});
            skLineSegment(sketch, "E440", {"start": v(-33.7, -42.85) * mm, "end": v(-31.26, -39.52) * mm});
            skLineSegment(sketch, "E441", {"start": v(-31.26, -39.52) * mm, "end": v(-28.98, -35.72) * mm});
            skLineSegment(sketch, "E442", {"start": v(-28.98, -35.72) * mm, "end": v(-26.87, -31.4) * mm});
            skLineSegment(sketch, "E443", {"start": v(-26.87, -31.4) * mm, "end": v(-25.4, -27.79) * mm});
            skLineSegment(sketch, "E444", {"start": v(-25.4, -27.79) * mm, "end": v(-24.97, -26.56) * mm});
            skLineSegment(sketch, "E445", {"start": v(-24.97, -26.56) * mm, "end": v(-22.64, -19.92) * mm});
            skLineSegment(sketch, "E446", {"start": v(-22.64, -19.92) * mm, "end": v(-42.75, -13.58) * mm});
            skLineSegment(sketch, "E447", {"start": v(-42.75, -13.58) * mm, "end": v(-44.83, -20.02) * mm});
            skLineSegment(sketch, "E448", {"start": v(147.96, -19.96) * mm, "end": v(147.34, -20.94) * mm});
            skLineSegment(sketch, "E449", {"start": v(147.34, -20.94) * mm, "end": v(145.36, -23.8) * mm});
            skLineSegment(sketch, "E450", {"start": v(145.36, -23.8) * mm, "end": v(142.86, -26.86) * mm});
            skLineSegment(sketch, "E451", {"start": v(142.86, -26.86) * mm, "end": v(140.42, -29.24) * mm});
            skLineSegment(sketch, "E452", {"start": v(140.42, -29.24) * mm, "end": v(138.02, -31) * mm});
            skLineSegment(sketch, "E453", {"start": v(138.02, -31) * mm, "end": v(135.63, -32.24) * mm});
            skLineSegment(sketch, "E454", {"start": v(135.63, -32.24) * mm, "end": v(133.2, -33.03) * mm});
            skLineSegment(sketch, "E455", {"start": v(133.2, -33.03) * mm, "end": v(130.73, -33.44) * mm});
            skLineSegment(sketch, "E456", {"start": v(130.73, -33.44) * mm, "end": v(128.81, -33.56) * mm});
            skLineSegment(sketch, "E457", {"start": v(128.81, -33.56) * mm, "end": v(128.17, -33.56) * mm});
            skLineSegment(sketch, "E458", {"start": v(128.17, -33.56) * mm, "end": v(127.53, -33.56) * mm});
            skLineSegment(sketch, "E459", {"start": v(127.53, -33.56) * mm, "end": v(125.6, -33.43) * mm});
            skLineSegment(sketch, "E460", {"start": v(125.6, -33.43) * mm, "end": v(123.21, -32.88) * mm});
            skLineSegment(sketch, "E461", {"start": v(123.21, -32.88) * mm, "end": v(121.08, -31.68) * mm});
            skLineSegment(sketch, "E462", {"start": v(121.08, -31.68) * mm, "end": v(119.24, -29.58) * mm});
            skLineSegment(sketch, "E463", {"start": v(119.24, -29.58) * mm, "end": v(117.72, -26.35) * mm});
            skLineSegment(sketch, "E464", {"start": v(117.72, -26.35) * mm, "end": v(116.6, -21.76) * mm});
            skLineSegment(sketch, "E465", {"start": v(116.6, -21.76) * mm, "end": v(115.88, -15.55) * mm});
            skLineSegment(sketch, "E466", {"start": v(115.88, -15.55) * mm, "end": v(115.63, -9.52) * mm});
            skLineSegment(sketch, "E467", {"start": v(115.63, -9.52) * mm, "end": v(115.63, -7.5) * mm});
            skLineSegment(sketch, "E468", {"start": v(115.63, -7.5) * mm, "end": v(115.63, 107.3) * mm});
            skLineSegment(sketch, "E469", {"start": v(115.63, 107.3) * mm, "end": v(164.94, 107.3) * mm});
            skLineSegment(sketch, "E470", {"start": v(164.94, 107.3) * mm, "end": v(164.94, 128.24) * mm});
            skLineSegment(sketch, "E471", {"start": v(164.94, 128.24) * mm, "end": v(115.63, 128.24) * mm});
            skLineSegment(sketch, "E472", {"start": v(115.63, 128.24) * mm, "end": v(115.63, 173.9) * mm});
            skLineSegment(sketch, "E473", {"start": v(115.63, 173.9) * mm, "end": v(97.68, 173.9) * mm});
            skLineSegment(sketch, "E474", {"start": v(97.68, 173.9) * mm, "end": v(96.37, 168.76) * mm});
            skLineSegment(sketch, "E475", {"start": v(96.37, 168.76) * mm, "end": v(95.97, 167.2) * mm});
            skLineSegment(sketch, "E476", {"start": v(95.97, 167.2) * mm, "end": v(94.57, 162.62) * mm});
            skLineSegment(sketch, "E477", {"start": v(94.57, 162.62) * mm, "end": v(92.4, 156.73) * mm});
            skLineSegment(sketch, "E478", {"start": v(92.4, 156.73) * mm, "end": v(89.84, 151.12) * mm});
            skLineSegment(sketch, "E479", {"start": v(89.84, 151.12) * mm, "end": v(86.93, 145.82) * mm});
            skLineSegment(sketch, "E480", {"start": v(86.93, 145.82) * mm, "end": v(83.68, 140.85) * mm});
            skLineSegment(sketch, "E481", {"start": v(83.68, 140.85) * mm, "end": v(80.11, 136.25) * mm});
            skLineSegment(sketch, "E482", {"start": v(80.11, 136.25) * mm, "end": v(76.25, 132.04) * mm});
            skLineSegment(sketch, "E483", {"start": v(76.25, 132.04) * mm, "end": v(73.17, 129.14) * mm});
            skLineSegment(sketch, "E484", {"start": v(73.17, 129.14) * mm, "end": v(72.1, 128.24) * mm});
            skLineSegment(sketch, "E485", {"start": v(72.1, 128.24) * mm, "end": v(44.67, 128.24) * mm});
            skLineSegment(sketch, "E486", {"start": v(44.67, 128.24) * mm, "end": v(44.67, 107.3) * mm});
            skLineSegment(sketch, "E487", {"start": v(44.67, 107.3) * mm, "end": v(67.67, 107.3) * mm});
            skLineSegment(sketch, "E488", {"start": v(67.67, 107.3) * mm, "end": v(67.67, -2.76) * mm});
            skLineSegment(sketch, "E489", {"start": v(67.67, -2.76) * mm, "end": v(67.67, -4.37) * mm});
            skLineSegment(sketch, "E490", {"start": v(67.67, -4.37) * mm, "end": v(67.88, -9.22) * mm});
            skLineSegment(sketch, "E491", {"start": v(67.88, -9.22) * mm, "end": v(68.52, -15.29) * mm});
            skLineSegment(sketch, "E492", {"start": v(68.52, -15.29) * mm, "end": v(69.58, -20.96) * mm});
            skLineSegment(sketch, "E493", {"start": v(69.58, -20.96) * mm, "end": v(71.06, -26.23) * mm});
            skLineSegment(sketch, "E494", {"start": v(71.06, -26.23) * mm, "end": v(72.96, -31.09) * mm});
            skLineSegment(sketch, "E495", {"start": v(72.96, -31.09) * mm, "end": v(75.27, -35.55) * mm});
            skLineSegment(sketch, "E496", {"start": v(75.27, -35.55) * mm, "end": v(78, -39.6) * mm});
            skLineSegment(sketch, "E497", {"start": v(78, -39.6) * mm, "end": v(81.12, -43.23) * mm});
            skLineSegment(sketch, "E498", {"start": v(81.12, -43.23) * mm, "end": v(84.66, -46.44) * mm});
            skLineSegment(sketch, "E499", {"start": v(84.66, -46.44) * mm, "end": v(88.6, -49.24) * mm});
            skLineSegment(sketch, "E500", {"start": v(88.6, -49.24) * mm, "end": v(92.93, -51.61) * mm});
            skLineSegment(sketch, "E501", {"start": v(92.93, -51.61) * mm, "end": v(97.66, -53.57) * mm});
            skLineSegment(sketch, "E502", {"start": v(97.66, -53.57) * mm, "end": v(102.79, -55.09) * mm});
            skLineSegment(sketch, "E503", {"start": v(102.79, -55.09) * mm, "end": v(108.3, -56.18) * mm});
            skLineSegment(sketch, "E504", {"start": v(108.3, -56.18) * mm, "end": v(114.21, -56.83) * mm});
            skLineSegment(sketch, "E505", {"start": v(114.21, -56.83) * mm, "end": v(118.93, -57.05) * mm});
            skLineSegment(sketch, "E506", {"start": v(118.93, -57.05) * mm, "end": v(120.5, -57.05) * mm});
            skLineSegment(sketch, "E507", {"start": v(120.5, -57.05) * mm, "end": v(122.26, -57.05) * mm});
            skLineSegment(sketch, "E508", {"start": v(122.26, -57.05) * mm, "end": v(127.55, -56.62) * mm});
            skLineSegment(sketch, "E509", {"start": v(127.55, -56.62) * mm, "end": v(134.24, -55.33) * mm});
            skLineSegment(sketch, "E510", {"start": v(134.24, -55.33) * mm, "end": v(140.53, -53.2) * mm});
            skLineSegment(sketch, "E511", {"start": v(140.53, -53.2) * mm, "end": v(146.41, -50.23) * mm});
            skLineSegment(sketch, "E512", {"start": v(146.41, -50.23) * mm, "end": v(151.87, -46.45) * mm});
            skLineSegment(sketch, "E513", {"start": v(151.87, -46.45) * mm, "end": v(156.88, -41.85) * mm});
            skLineSegment(sketch, "E514", {"start": v(156.88, -41.85) * mm, "end": v(161.42, -36.46) * mm});
            skLineSegment(sketch, "E515", {"start": v(161.42, -36.46) * mm, "end": v(164.55, -31.87) * mm});
            skLineSegment(sketch, "E516", {"start": v(164.55, -31.87) * mm, "end": v(165.48, -30.28) * mm});
            skLineSegment(sketch, "E517", {"start": v(165.48, -30.28) * mm, "end": v(168.93, -24.31) * mm});
            skLineSegment(sketch, "E518", {"start": v(168.93, -24.31) * mm, "end": v(151.4, -14.43) * mm});
            skLineSegment(sketch, "E519", {"start": v(151.4, -14.43) * mm, "end": v(147.96, -19.96) * mm});
            skLineSegment(sketch, "E520", {"start": v(437, 128.24) * mm, "end": v(365.66, 128.24) * mm});
            skLineSegment(sketch, "E521", {"start": v(365.66, 128.24) * mm, "end": v(365.66, 107.3) * mm});
            skLineSegment(sketch, "E522", {"start": v(365.66, 107.3) * mm, "end": v(389.03, 107.3) * mm});
            skLineSegment(sketch, "E523", {"start": v(389.03, 107.3) * mm, "end": v(389.03, 1.15) * mm});
            skLineSegment(sketch, "E524", {"start": v(389.03, 1.15) * mm, "end": v(387.91, -0.9) * mm});
            skLineSegment(sketch, "E525", {"start": v(387.91, -0.9) * mm, "end": v(384.22, -6.85) * mm});
            skLineSegment(sketch, "E526", {"start": v(384.22, -6.85) * mm, "end": v(379.1, -13.87) * mm});
            skLineSegment(sketch, "E527", {"start": v(379.1, -13.87) * mm, "end": v(373.68, -19.9) * mm});
            skLineSegment(sketch, "E528", {"start": v(373.68, -19.9) * mm, "end": v(368.03, -24.87) * mm});
            skLineSegment(sketch, "E529", {"start": v(368.03, -24.87) * mm, "end": v(362.16, -28.8) * mm});
            skLineSegment(sketch, "E530", {"start": v(362.16, -28.8) * mm, "end": v(356.12, -31.62) * mm});
            skLineSegment(sketch, "E531", {"start": v(356.12, -31.62) * mm, "end": v(349.93, -33.34) * mm});
            skLineSegment(sketch, "E532", {"start": v(349.93, -33.34) * mm, "end": v(345.2, -33.92) * mm});
            skLineSegment(sketch, "E533", {"start": v(345.2, -33.92) * mm, "end": v(343.63, -33.92) * mm});
            skLineSegment(sketch, "E534", {"start": v(343.63, -33.92) * mm, "end": v(342.97, -33.92) * mm});
            skLineSegment(sketch, "E535", {"start": v(342.97, -33.92) * mm, "end": v(341, -33.85) * mm});
            skLineSegment(sketch, "E536", {"start": v(341, -33.85) * mm, "end": v(338.49, -33.62) * mm});
            skLineSegment(sketch, "E537", {"start": v(338.49, -33.62) * mm, "end": v(336.1, -33.2) * mm});
            skLineSegment(sketch, "E538", {"start": v(336.1, -33.2) * mm, "end": v(333.85, -32.57) * mm});
            skLineSegment(sketch, "E539", {"start": v(333.85, -32.57) * mm, "end": v(331.74, -31.71) * mm});
            skLineSegment(sketch, "E540", {"start": v(331.74, -31.71) * mm, "end": v(329.78, -30.6) * mm});
            skLineSegment(sketch, "E541", {"start": v(329.78, -30.6) * mm, "end": v(327.97, -29.2) * mm});
            skLineSegment(sketch, "E542", {"start": v(327.97, -29.2) * mm, "end": v(326.32, -27.49) * mm});
            skLineSegment(sketch, "E543", {"start": v(326.32, -27.49) * mm, "end": v(324.84, -25.45) * mm});
            skLineSegment(sketch, "E544", {"start": v(324.84, -25.45) * mm, "end": v(323.53, -23.05) * mm});
            skLineSegment(sketch, "E545", {"start": v(323.53, -23.05) * mm, "end": v(322.4, -20.27) * mm});
            skLineSegment(sketch, "E546", {"start": v(322.4, -20.27) * mm, "end": v(321.48, -17.1) * mm});
            skLineSegment(sketch, "E547", {"start": v(321.48, -17.1) * mm, "end": v(320.74, -13.48) * mm});
            skLineSegment(sketch, "E548", {"start": v(320.74, -13.48) * mm, "end": v(320.2, -9.42) * mm});
            skLineSegment(sketch, "E549", {"start": v(320.2, -9.42) * mm, "end": v(319.87, -4.88) * mm});
            skLineSegment(sketch, "E550", {"start": v(319.87, -4.88) * mm, "end": v(319.76, -1.1) * mm});
            skLineSegment(sketch, "E551", {"start": v(319.76, -1.1) * mm, "end": v(319.76, 0.17) * mm});
            skLineSegment(sketch, "E552", {"start": v(319.76, 0.17) * mm, "end": v(319.76, 128.24) * mm});
            skLineSegment(sketch, "E553", {"start": v(319.76, 128.24) * mm, "end": v(248.8, 128.24) * mm});
            skLineSegment(sketch, "E554", {"start": v(248.8, 128.24) * mm, "end": v(248.8, 107.3) * mm});
            skLineSegment(sketch, "E555", {"start": v(248.8, 107.3) * mm, "end": v(271.8, 107.3) * mm});
            skLineSegment(sketch, "E556", {"start": v(271.8, 107.3) * mm, "end": v(271.8, 11.85) * mm});
            skLineSegment(sketch, "E557", {"start": v(271.8, 11.85) * mm, "end": v(271.8, 9.75) * mm});
            skLineSegment(sketch, "E558", {"start": v(271.8, 9.75) * mm, "end": v(272.04, 3.44) * mm});
            skLineSegment(sketch, "E559", {"start": v(272.04, 3.44) * mm, "end": v(272.78, -4.42) * mm});
            skLineSegment(sketch, "E560", {"start": v(272.78, -4.42) * mm, "end": v(274, -11.72) * mm});
            skLineSegment(sketch, "E561", {"start": v(274, -11.72) * mm, "end": v(275.73, -18.47) * mm});
            skLineSegment(sketch, "E562", {"start": v(275.73, -18.47) * mm, "end": v(277.95, -24.67) * mm});
            skLineSegment(sketch, "E563", {"start": v(277.95, -24.67) * mm, "end": v(280.67, -30.33) * mm});
            skLineSegment(sketch, "E564", {"start": v(280.67, -30.33) * mm, "end": v(283.88, -35.43) * mm});
            skLineSegment(sketch, "E565", {"start": v(283.88, -35.43) * mm, "end": v(287.6, -39.99) * mm});
            skLineSegment(sketch, "E566", {"start": v(287.6, -39.99) * mm, "end": v(291.82, -44) * mm});
            skLineSegment(sketch, "E567", {"start": v(291.82, -44) * mm, "end": v(296.54, -47.48) * mm});
            skLineSegment(sketch, "E568", {"start": v(296.54, -47.48) * mm, "end": v(301.78, -50.41) * mm});
            skLineSegment(sketch, "E569", {"start": v(301.78, -50.41) * mm, "end": v(307.51, -52.8) * mm});
            skLineSegment(sketch, "E570", {"start": v(307.51, -52.8) * mm, "end": v(313.77, -54.67) * mm});
            skLineSegment(sketch, "E571", {"start": v(313.77, -54.67) * mm, "end": v(320.53, -56) * mm});
            skLineSegment(sketch, "E572", {"start": v(320.53, -56) * mm, "end": v(327.8, -56.79) * mm});
            skLineSegment(sketch, "E573", {"start": v(327.8, -56.79) * mm, "end": v(333.64, -57.05) * mm});
            skLineSegment(sketch, "E574", {"start": v(333.64, -57.05) * mm, "end": v(335.6, -57.05) * mm});
            skLineSegment(sketch, "E575", {"start": v(335.6, -57.05) * mm, "end": v(337.52, -57.05) * mm});
            skLineSegment(sketch, "E576", {"start": v(337.52, -57.05) * mm, "end": v(343.28, -56.7) * mm});
            skLineSegment(sketch, "E577", {"start": v(343.28, -56.7) * mm, "end": v(350.68, -55.62) * mm});
            skLineSegment(sketch, "E578", {"start": v(350.68, -55.62) * mm, "end": v(357.8, -53.82) * mm});
            skLineSegment(sketch, "E579", {"start": v(357.8, -53.82) * mm, "end": v(364.64, -51.32) * mm});
            skLineSegment(sketch, "E580", {"start": v(364.64, -51.32) * mm, "end": v(371.18, -48.1) * mm});
            skLineSegment(sketch, "E581", {"start": v(371.18, -48.1) * mm, "end": v(377.43, -44.17) * mm});
            skLineSegment(sketch, "E582", {"start": v(377.43, -44.17) * mm, "end": v(383.38, -39.53) * mm});
            skLineSegment(sketch, "E583", {"start": v(383.38, -39.53) * mm, "end": v(387.68, -35.58) * mm});
            skLineSegment(sketch, "E584", {"start": v(387.68, -35.58) * mm, "end": v(389.03, -34.19) * mm});
            skLineSegment(sketch, "E585", {"start": v(389.03, -34.19) * mm, "end": v(389.03, -53.4) * mm});
            skLineSegment(sketch, "E586", {"start": v(389.03, -53.4) * mm, "end": v(460, -53.4) * mm});
            skLineSegment(sketch, "E587", {"start": v(460, -53.4) * mm, "end": v(460, -32.46) * mm});
            skLineSegment(sketch, "E588", {"start": v(460, -32.46) * mm, "end": v(437, -32.46) * mm});
            skLineSegment(sketch, "E589", {"start": v(437, -32.46) * mm, "end": v(437, 128.24) * mm});
            skLineSegment(sketch, "E590", {"start": v(626.48, 61.3) * mm, "end": v(624.1, 61.92) * mm});
            skLineSegment(sketch, "E591", {"start": v(624.1, 61.92) * mm, "end": v(616.96, 63.8) * mm});
            skLineSegment(sketch, "E592", {"start": v(616.96, 63.8) * mm, "end": v(608.49, 66.25) * mm});
            skLineSegment(sketch, "E593", {"start": v(608.49, 66.25) * mm, "end": v(601.12, 68.8) * mm});
            skLineSegment(sketch, "E594", {"start": v(601.12, 68.8) * mm, "end": v(594.94, 71.58) * mm});
            skLineSegment(sketch, "E595", {"start": v(594.94, 71.58) * mm, "end": v(590, 74.74) * mm});
            skLineSegment(sketch, "E596", {"start": v(590, 74.74) * mm, "end": v(586.4, 78.4) * mm});
            skLineSegment(sketch, "E597", {"start": v(586.4, 78.4) * mm, "end": v(584.17, 82.72) * mm});
            skLineSegment(sketch, "E598", {"start": v(584.17, 82.72) * mm, "end": v(583.42, 86.54) * mm});
            skLineSegment(sketch, "E599", {"start": v(583.42, 86.54) * mm, "end": v(583.42, 87.82) * mm});
            skLineSegment(sketch, "E600", {"start": v(583.42, 87.82) * mm, "end": v(583.42, 89) * mm});
            skLineSegment(sketch, "E601", {"start": v(583.42, 89) * mm, "end": v(583.92, 92.5) * mm});
            skLineSegment(sketch, "E602", {"start": v(583.92, 92.5) * mm, "end": v(585.4, 96.71) * mm});
            skLineSegment(sketch, "E603", {"start": v(585.4, 96.71) * mm, "end": v(587.88, 100.43) * mm});
            skLineSegment(sketch, "E604", {"start": v(587.88, 100.43) * mm, "end": v(590.4, 102.94) * mm});
            skLineSegment(sketch, "E605", {"start": v(590.4, 102.94) * mm, "end": v(591.34, 103.65) * mm});
            skLineSegment(sketch, "E606", {"start": v(591.34, 103.65) * mm, "end": v(592.58, 104.58) * mm});
            skLineSegment(sketch, "E607", {"start": v(592.58, 104.58) * mm, "end": v(596.75, 106.8) * mm});
            skLineSegment(sketch, "E608", {"start": v(596.75, 106.8) * mm, "end": v(603.42, 109.1) * mm});
            skLineSegment(sketch, "E609", {"start": v(603.42, 109.1) * mm, "end": v(611.22, 110.49) * mm});
            skLineSegment(sketch, "E610", {"start": v(611.22, 110.49) * mm, "end": v(617.85, 110.95) * mm});
            skLineSegment(sketch, "E611", {"start": v(617.85, 110.95) * mm, "end": v(620.06, 110.95) * mm});
            skLineSegment(sketch, "E612", {"start": v(620.06, 110.95) * mm, "end": v(622.05, 110.95) * mm});
            skLineSegment(sketch, "E613", {"start": v(622.05, 110.95) * mm, "end": v(628.03, 110.57) * mm});
            skLineSegment(sketch, "E614", {"start": v(628.03, 110.57) * mm, "end": v(634.98, 109.53) * mm});
            skLineSegment(sketch, "E615", {"start": v(634.98, 109.53) * mm, "end": v(640.9, 108.03) * mm});
            skLineSegment(sketch, "E616", {"start": v(640.9, 108.03) * mm, "end": v(645.79, 106.22) * mm});
            skLineSegment(sketch, "E617", {"start": v(645.79, 106.22) * mm, "end": v(649.63, 104.28) * mm});
            skLineSegment(sketch, "E618", {"start": v(649.63, 104.28) * mm, "end": v(652.43, 102.4) * mm});
            skLineSegment(sketch, "E619", {"start": v(652.43, 102.4) * mm, "end": v(654.18, 100.76) * mm});
            skLineSegment(sketch, "E620", {"start": v(654.18, 100.76) * mm, "end": v(654.82, 99.84) * mm});
            skLineSegment(sketch, "E621", {"start": v(654.82, 99.84) * mm, "end": v(654.88, 99.51) * mm});
            skLineSegment(sketch, "E622", {"start": v(654.88, 99.51) * mm, "end": v(654.88, 99.36) * mm});
            skLineSegment(sketch, "E623", {"start": v(654.88, 99.36) * mm, "end": v(654.76, 98.9) * mm});
            skLineSegment(sketch, "E624", {"start": v(654.76, 98.9) * mm, "end": v(654.34, 98.22) * mm});
            skLineSegment(sketch, "E625", {"start": v(654.34, 98.22) * mm, "end": v(653.46, 97.28) * mm});
            skLineSegment(sketch, "E626", {"start": v(653.46, 97.28) * mm, "end": v(652.36, 96.27) * mm});
            skLineSegment(sketch, "E627", {"start": v(652.36, 96.27) * mm, "end": v(652, 95.93) * mm});
            skLineSegment(sketch, "E628", {"start": v(652, 95.93) * mm, "end": v(651.67, 95.65) * mm});
            skLineSegment(sketch, "E629", {"start": v(651.67, 95.65) * mm, "end": v(650.72, 94.78) * mm});
            skLineSegment(sketch, "E630", {"start": v(650.72, 94.78) * mm, "end": v(649.37, 93.46) * mm});
            skLineSegment(sketch, "E631", {"start": v(649.37, 93.46) * mm, "end": v(648.03, 91.94) * mm});
            skLineSegment(sketch, "E632", {"start": v(648.03, 91.94) * mm, "end": v(646.75, 90.2) * mm});
            skLineSegment(sketch, "E633", {"start": v(646.75, 90.2) * mm, "end": v(645.63, 88.22) * mm});
            skLineSegment(sketch, "E634", {"start": v(645.63, 88.22) * mm, "end": v(644.73, 85.97) * mm});
            skLineSegment(sketch, "E635", {"start": v(644.73, 85.97) * mm, "end": v(644.13, 83.4) * mm});
            skLineSegment(sketch, "E636", {"start": v(644.13, 83.4) * mm, "end": v(643.92, 81.24) * mm});
            skLineSegment(sketch, "E637", {"start": v(643.92, 81.24) * mm, "end": v(643.92, 80.52) * mm});
            skLineSegment(sketch, "E638", {"start": v(643.92, 80.52) * mm, "end": v(643.92, 79.26) * mm});
            skLineSegment(sketch, "E639", {"start": v(643.92, 79.26) * mm, "end": v(644.39, 75.51) * mm});
            skLineSegment(sketch, "E640", {"start": v(644.39, 75.51) * mm, "end": v(645.74, 70.96) * mm});
            skLineSegment(sketch, "E641", {"start": v(645.74, 70.96) * mm, "end": v(647.9, 66.94) * mm});
            skLineSegment(sketch, "E642", {"start": v(647.9, 66.94) * mm, "end": v(650.82, 63.5) * mm});
            skLineSegment(sketch, "E643", {"start": v(650.82, 63.5) * mm, "end": v(654.42, 60.7) * mm});
            skLineSegment(sketch, "E644", {"start": v(654.42, 60.7) * mm, "end": v(658.63, 58.64) * mm});
            skLineSegment(sketch, "E645", {"start": v(658.63, 58.64) * mm, "end": v(663.4, 57.35) * mm});
            skLineSegment(sketch, "E646", {"start": v(663.4, 57.35) * mm, "end": v(667.32, 56.9) * mm});
            skLineSegment(sketch, "E647", {"start": v(667.32, 56.9) * mm, "end": v(668.63, 56.9) * mm});
            skLineSegment(sketch, "E648", {"start": v(668.63, 56.9) * mm, "end": v(669.93, 56.9) * mm});
            skLineSegment(sketch, "E649", {"start": v(669.93, 56.9) * mm, "end": v(673.84, 57.39) * mm});
            skLineSegment(sketch, "E650", {"start": v(673.84, 57.39) * mm, "end": v(678.53, 58.8) * mm});
            skLineSegment(sketch, "E651", {"start": v(678.53, 58.8) * mm, "end": v(682.62, 61.1) * mm});
            skLineSegment(sketch, "E652", {"start": v(682.62, 61.1) * mm, "end": v(686.09, 64.22) * mm});
            skLineSegment(sketch, "E653", {"start": v(686.09, 64.22) * mm, "end": v(688.87, 68.1) * mm});
            skLineSegment(sketch, "E654", {"start": v(688.87, 68.1) * mm, "end": v(690.92, 72.7) * mm});
            skLineSegment(sketch, "E655", {"start": v(690.92, 72.7) * mm, "end": v(692.18, 77.95) * mm});
            skLineSegment(sketch, "E656", {"start": v(692.18, 77.95) * mm, "end": v(692.62, 82.34) * mm});
            skLineSegment(sketch, "E657", {"start": v(692.62, 82.34) * mm, "end": v(692.62, 83.8) * mm});
            skLineSegment(sketch, "E658", {"start": v(692.62, 83.8) * mm, "end": v(692.62, 85.12) * mm});
            skLineSegment(sketch, "E659", {"start": v(692.62, 85.12) * mm, "end": v(692.25, 89.08) * mm});
            skLineSegment(sketch, "E660", {"start": v(692.25, 89.08) * mm, "end": v(691.16, 94.18) * mm});
            skLineSegment(sketch, "E661", {"start": v(691.16, 94.18) * mm, "end": v(689.36, 99.07) * mm});
            skLineSegment(sketch, "E662", {"start": v(689.36, 99.07) * mm, "end": v(686.87, 103.74) * mm});
            skLineSegment(sketch, "E663", {"start": v(686.87, 103.74) * mm, "end": v(683.7, 108.15) * mm});
            skLineSegment(sketch, "E664", {"start": v(683.7, 108.15) * mm, "end": v(679.9, 112.28) * mm});
            skLineSegment(sketch, "E665", {"start": v(679.9, 112.28) * mm, "end": v(675.44, 116.1) * mm});
            skLineSegment(sketch, "E666", {"start": v(675.44, 116.1) * mm, "end": v(671.68, 118.76) * mm});
            skLineSegment(sketch, "E667", {"start": v(671.68, 118.76) * mm, "end": v(670.37, 119.56) * mm});
            skLineSegment(sketch, "E668", {"start": v(670.37, 119.56) * mm, "end": v(669.13, 120.32) * mm});
            skLineSegment(sketch, "E669", {"start": v(669.13, 120.32) * mm, "end": v(665.28, 122.38) * mm});
            skLineSegment(sketch, "E670", {"start": v(665.28, 122.38) * mm, "end": v(659.8, 124.85) * mm});
            skLineSegment(sketch, "E671", {"start": v(659.8, 124.85) * mm, "end": v(653.93, 126.96) * mm});
            skLineSegment(sketch, "E672", {"start": v(653.93, 126.96) * mm, "end": v(647.74, 128.7) * mm});
            skLineSegment(sketch, "E673", {"start": v(647.74, 128.7) * mm, "end": v(641.25, 130.09) * mm});
            skLineSegment(sketch, "E674", {"start": v(641.25, 130.09) * mm, "end": v(634.52, 131.08) * mm});
            skLineSegment(sketch, "E675", {"start": v(634.52, 131.08) * mm, "end": v(627.56, 131.69) * mm});
            skLineSegment(sketch, "E676", {"start": v(627.56, 131.69) * mm, "end": v(622.2, 131.9) * mm});
            skLineSegment(sketch, "E677", {"start": v(622.2, 131.9) * mm, "end": v(620.42, 131.9) * mm});
            skLineSegment(sketch, "E678", {"start": v(620.42, 131.9) * mm, "end": v(618.25, 131.9) * mm});
            skLineSegment(sketch, "E679", {"start": v(618.25, 131.9) * mm, "end": v(611.71, 131.56) * mm});
            skLineSegment(sketch, "E680", {"start": v(611.71, 131.56) * mm, "end": v(603.62, 130.6) * mm});
            skLineSegment(sketch, "E681", {"start": v(603.62, 130.6) * mm, "end": v(596.14, 129.03) * mm});
            skLineSegment(sketch, "E682", {"start": v(596.14, 129.03) * mm, "end": v(589.25, 126.92) * mm});
            skLineSegment(sketch, "E683", {"start": v(589.25, 126.92) * mm, "end": v(582.96, 124.3) * mm});
            skLineSegment(sketch, "E684", {"start": v(582.96, 124.3) * mm, "end": v(577.25, 121.23) * mm});
            skLineSegment(sketch, "E685", {"start": v(577.25, 121.23) * mm, "end": v(572.13, 117.73) * mm});
            skLineSegment(sketch, "E686", {"start": v(572.13, 117.73) * mm, "end": v(567.57, 113.85) * mm});
            skLineSegment(sketch, "E687", {"start": v(567.57, 113.85) * mm, "end": v(563.58, 109.63) * mm});
            skLineSegment(sketch, "E688", {"start": v(563.58, 109.63) * mm, "end": v(560.14, 105.12) * mm});
            skLineSegment(sketch, "E689", {"start": v(560.14, 105.12) * mm, "end": v(557.25, 100.36) * mm});
            skLineSegment(sketch, "E690", {"start": v(557.25, 100.36) * mm, "end": v(554.9, 95.4) * mm});
            skLineSegment(sketch, "E691", {"start": v(554.9, 95.4) * mm, "end": v(553.1, 90.27) * mm});
            skLineSegment(sketch, "E692", {"start": v(553.1, 90.27) * mm, "end": v(551.81, 85.01) * mm});
            skLineSegment(sketch, "E693", {"start": v(551.81, 85.01) * mm, "end": v(551.04, 79.68) * mm});
            skLineSegment(sketch, "E694", {"start": v(551.04, 79.68) * mm, "end": v(550.79, 75.65) * mm});
            skLineSegment(sketch, "E695", {"start": v(550.79, 75.65) * mm, "end": v(550.79, 74.3) * mm});
            skLineSegment(sketch, "E696", {"start": v(550.79, 74.3) * mm, "end": v(550.79, 72.5) * mm});
            skLineSegment(sketch, "E697", {"start": v(550.79, 72.5) * mm, "end": v(551.22, 67.04) * mm});
            skLineSegment(sketch, "E698", {"start": v(551.22, 67.04) * mm, "end": v(552.47, 60.46) * mm});
            skLineSegment(sketch, "E699", {"start": v(552.47, 60.46) * mm, "end": v(554.47, 54.54) * mm});
            skLineSegment(sketch, "E700", {"start": v(554.47, 54.54) * mm, "end": v(557.16, 49.23) * mm});
            skLineSegment(sketch, "E701", {"start": v(557.16, 49.23) * mm, "end": v(560.46, 44.48) * mm});
            skLineSegment(sketch, "E702", {"start": v(560.46, 44.48) * mm, "end": v(564.32, 40.26) * mm});
            skLineSegment(sketch, "E703", {"start": v(564.32, 40.26) * mm, "end": v(568.67, 36.51) * mm});
            skLineSegment(sketch, "E704", {"start": v(568.67, 36.51) * mm, "end": v(573.43, 33.2) * mm});
            skLineSegment(sketch, "E705", {"start": v(573.43, 33.2) * mm, "end": v(578.56, 30.28) * mm});
            skLineSegment(sketch, "E706", {"start": v(578.56, 30.28) * mm, "end": v(583.97, 27.71) * mm});
            skLineSegment(sketch, "E707", {"start": v(583.97, 27.71) * mm, "end": v(589.6, 25.45) * mm});
            skLineSegment(sketch, "E708", {"start": v(589.6, 25.45) * mm, "end": v(595.4, 23.44) * mm});
            skLineSegment(sketch, "E709", {"start": v(595.4, 23.44) * mm, "end": v(601.28, 21.65) * mm});
            skLineSegment(sketch, "E710", {"start": v(601.28, 21.65) * mm, "end": v(607.18, 20.03) * mm});
            skLineSegment(sketch, "E711", {"start": v(607.18, 20.03) * mm, "end": v(613.05, 18.54) * mm});
            skLineSegment(sketch, "E712", {"start": v(613.05, 18.54) * mm, "end": v(617.37, 17.49) * mm});
            skLineSegment(sketch, "E713", {"start": v(617.37, 17.49) * mm, "end": v(618.8, 17.14) * mm});
            skLineSegment(sketch, "E714", {"start": v(618.8, 17.14) * mm, "end": v(621.29, 16.54) * mm});
            skLineSegment(sketch, "E715", {"start": v(621.29, 16.54) * mm, "end": v(628.71, 14.68) * mm});
            skLineSegment(sketch, "E716", {"start": v(628.71, 14.68) * mm, "end": v(637.54, 12.23) * mm});
            skLineSegment(sketch, "E717", {"start": v(637.54, 12.23) * mm, "end": v(645.2, 9.64) * mm});
            skLineSegment(sketch, "E718", {"start": v(645.2, 9.64) * mm, "end": v(651.64, 6.75) * mm});
            skLineSegment(sketch, "E719", {"start": v(651.64, 6.75) * mm, "end": v(656.78, 3.42) * mm});
            skLineSegment(sketch, "E720", {"start": v(656.78, 3.42) * mm, "end": v(660.54, -0.5) * mm});
            skLineSegment(sketch, "E721", {"start": v(660.54, -0.5) * mm, "end": v(662.85, -5.2) * mm});
            skLineSegment(sketch, "E722", {"start": v(662.85, -5.2) * mm, "end": v(663.64, -9.4) * mm});
            skLineSegment(sketch, "E723", {"start": v(663.64, -9.4) * mm, "end": v(663.64, -10.8) * mm});
            skLineSegment(sketch, "E724", {"start": v(663.64, -10.8) * mm, "end": v(663.64, -12.33) * mm});
            skLineSegment(sketch, "E725", {"start": v(663.64, -12.33) * mm, "end": v(663, -16.95) * mm});
            skLineSegment(sketch, "E726", {"start": v(663, -16.95) * mm, "end": v(661.04, -22.15) * mm});
            skLineSegment(sketch, "E727", {"start": v(661.04, -22.15) * mm, "end": v(657.71, -26.47) * mm});
            skLineSegment(sketch, "E728", {"start": v(657.71, -26.47) * mm, "end": v(654.25, -29.27) * mm});
            skLineSegment(sketch, "E729", {"start": v(654.25, -29.27) * mm, "end": v(652.98, -30) * mm});
            skLineSegment(sketch, "E730", {"start": v(652.98, -30) * mm, "end": v(651.6, -30.8) * mm});
            skLineSegment(sketch, "E731", {"start": v(651.6, -30.8) * mm, "end": v(647.14, -32.64) * mm});
            skLineSegment(sketch, "E732", {"start": v(647.14, -32.64) * mm, "end": v(640.07, -34.56) * mm});
            skLineSegment(sketch, "E733", {"start": v(640.07, -34.56) * mm, "end": v(631.85, -35.72) * mm});
            skLineSegment(sketch, "E734", {"start": v(631.85, -35.72) * mm, "end": v(624.93, -36.11) * mm});
            skLineSegment(sketch, "E735", {"start": v(624.93, -36.11) * mm, "end": v(622.62, -36.11) * mm});
            skLineSegment(sketch, "E736", {"start": v(622.62, -36.11) * mm, "end": v(620.56, -36.11) * mm});
            skLineSegment(sketch, "E737", {"start": v(620.56, -36.11) * mm, "end": v(614.4, -35.8) * mm});
            skLineSegment(sketch, "E738", {"start": v(614.4, -35.8) * mm, "end": v(606.78, -34.85) * mm});
            skLineSegment(sketch, "E739", {"start": v(606.78, -34.85) * mm, "end": v(599.9, -33.3) * mm});
            skLineSegment(sketch, "E740", {"start": v(599.9, -33.3) * mm, "end": v(595.38, -31.83) * mm});
            skLineSegment(sketch, "E741", {"start": v(595.38, -31.83) * mm, "end": v(593.94, -31.2) * mm});
            skLineSegment(sketch, "E742", {"start": v(593.94, -31.2) * mm, "end": v(593, -30.8) * mm});
            skLineSegment(sketch, "E743", {"start": v(593, -30.8) * mm, "end": v(590.28, -29.32) * mm});
            skLineSegment(sketch, "E744", {"start": v(590.28, -29.32) * mm, "end": v(587.55, -27.3) * mm});
            skLineSegment(sketch, "E745", {"start": v(587.55, -27.3) * mm, "end": v(585.83, -25.23) * mm});
            skLineSegment(sketch, "E746", {"start": v(585.83, -25.23) * mm, "end": v(585.24, -23.72) * mm});
            skLineSegment(sketch, "E747", {"start": v(585.24, -23.72) * mm, "end": v(585.24, -23.2) * mm});
            skLineSegment(sketch, "E748", {"start": v(585.24, -23.2) * mm, "end": v(585.24, -22.96) * mm});
            skLineSegment(sketch, "E749", {"start": v(585.24, -22.96) * mm, "end": v(585.33, -22.2) * mm});
            skLineSegment(sketch, "E750", {"start": v(585.33, -22.2) * mm, "end": v(585.7, -21.34) * mm});
            skLineSegment(sketch, "E751", {"start": v(585.7, -21.34) * mm, "end": v(586.47, -20.35) * mm});
            skLineSegment(sketch, "E752", {"start": v(586.47, -20.35) * mm, "end": v(587.43, -19.33) * mm});
            skLineSegment(sketch, "E753", {"start": v(587.43, -19.33) * mm, "end": v(587.76, -19) * mm});
            skLineSegment(sketch, "E754", {"start": v(587.76, -19) * mm, "end": v(588.05, -18.7) * mm});
            skLineSegment(sketch, "E755", {"start": v(588.05, -18.7) * mm, "end": v(588.92, -17.81) * mm});
            skLineSegment(sketch, "E756", {"start": v(588.92, -17.81) * mm, "end": v(590.14, -16.45) * mm});
            skLineSegment(sketch, "E757", {"start": v(590.14, -16.45) * mm, "end": v(591.37, -14.87) * mm});
            skLineSegment(sketch, "E758", {"start": v(591.37, -14.87) * mm, "end": v(592.53, -13.03) * mm});
            skLineSegment(sketch, "E759", {"start": v(592.53, -13.03) * mm, "end": v(593.55, -10.9) * mm});
            skLineSegment(sketch, "E760", {"start": v(593.55, -10.9) * mm, "end": v(594.37, -8.45) * mm});
            skLineSegment(sketch, "E761", {"start": v(594.37, -8.45) * mm, "end": v(594.9, -5.62) * mm});
            skLineSegment(sketch, "E762", {"start": v(594.9, -5.62) * mm, "end": v(595.1, -3.2) * mm});
            skLineSegment(sketch, "E763", {"start": v(595.1, -3.2) * mm, "end": v(595.1, -2.39) * mm});
            skLineSegment(sketch, "E764", {"start": v(595.1, -2.39) * mm, "end": v(595.1, -1.16) * mm});
            skLineSegment(sketch, "E765", {"start": v(595.1, -1.16) * mm, "end": v(594.65, 2.54) * mm});
            skLineSegment(sketch, "E766", {"start": v(594.65, 2.54) * mm, "end": v(593.32, 7.02) * mm});
            skLineSegment(sketch, "E767", {"start": v(593.32, 7.02) * mm, "end": v(591.18, 10.99) * mm});
            skLineSegment(sketch, "E768", {"start": v(591.18, 10.99) * mm, "end": v(588.3, 14.37) * mm});
            skLineSegment(sketch, "E769", {"start": v(588.3, 14.37) * mm, "end": v(584.76, 17.12) * mm});
            skLineSegment(sketch, "E770", {"start": v(584.76, 17.12) * mm, "end": v(580.6, 19.16) * mm});
            skLineSegment(sketch, "E771", {"start": v(580.6, 19.16) * mm, "end": v(575.92, 20.43) * mm});
            skLineSegment(sketch, "E772", {"start": v(575.92, 20.43) * mm, "end": v(572.05, 20.86) * mm});
            skLineSegment(sketch, "E773", {"start": v(572.05, 20.86) * mm, "end": v(570.76, 20.86) * mm});
            skLineSegment(sketch, "E774", {"start": v(570.76, 20.86) * mm, "end": v(569.4, 20.86) * mm});
            skLineSegment(sketch, "E775", {"start": v(569.4, 20.86) * mm, "end": v(565.34, 20.38) * mm});
            skLineSegment(sketch, "E776", {"start": v(565.34, 20.38) * mm, "end": v(560.52, 18.95) * mm});
            skLineSegment(sketch, "E777", {"start": v(560.52, 18.95) * mm, "end": v(556.36, 16.63) * mm});
            skLineSegment(sketch, "E778", {"start": v(556.36, 16.63) * mm, "end": v(552.87, 13.44) * mm});
            skLineSegment(sketch, "E779", {"start": v(552.87, 13.44) * mm, "end": v(550.1, 9.43) * mm});
            skLineSegment(sketch, "E780", {"start": v(550.1, 9.43) * mm, "end": v(548.07, 4.64) * mm});
            skLineSegment(sketch, "E781", {"start": v(548.07, 4.64) * mm, "end": v(546.83, -0.9) * mm});
            skLineSegment(sketch, "E782", {"start": v(546.83, -0.9) * mm, "end": v(546.41, -5.58) * mm});
            skLineSegment(sketch, "E783", {"start": v(546.41, -5.58) * mm, "end": v(546.41, -7.14) * mm});
            skLineSegment(sketch, "E784", {"start": v(546.41, -7.14) * mm, "end": v(546.41, -8.43) * mm});
            skLineSegment(sketch, "E785", {"start": v(546.41, -8.43) * mm, "end": v(546.75, -12.31) * mm});
            skLineSegment(sketch, "E786", {"start": v(546.75, -12.31) * mm, "end": v(547.76, -17.34) * mm});
            skLineSegment(sketch, "E787", {"start": v(547.76, -17.34) * mm, "end": v(549.43, -22.18) * mm});
            skLineSegment(sketch, "E788", {"start": v(549.43, -22.18) * mm, "end": v(551.73, -26.83) * mm});
            skLineSegment(sketch, "E789", {"start": v(551.73, -26.83) * mm, "end": v(554.65, -31.24) * mm});
            skLineSegment(sketch, "E790", {"start": v(554.65, -31.24) * mm, "end": v(558.2, -35.4) * mm});
            skLineSegment(sketch, "E791", {"start": v(558.2, -35.4) * mm, "end": v(562.32, -39.26) * mm});
            skLineSegment(sketch, "E792", {"start": v(562.32, -39.26) * mm, "end": v(565.8, -41.99) * mm});
            skLineSegment(sketch, "E793", {"start": v(565.8, -41.99) * mm, "end": v(567.02, -42.82) * mm});
            skLineSegment(sketch, "E794", {"start": v(567.02, -42.82) * mm, "end": v(568.32, -43.7) * mm});
            skLineSegment(sketch, "E795", {"start": v(568.32, -43.7) * mm, "end": v(572.41, -46.1) * mm});
            skLineSegment(sketch, "E796", {"start": v(572.41, -46.1) * mm, "end": v(578.32, -48.97) * mm});
            skLineSegment(sketch, "E797", {"start": v(578.32, -48.97) * mm, "end": v(584.7, -51.41) * mm});
            skLineSegment(sketch, "E798", {"start": v(584.7, -51.41) * mm, "end": v(591.54, -53.43) * mm});
            skLineSegment(sketch, "E799", {"start": v(591.54, -53.43) * mm, "end": v(598.82, -55) * mm});
            skLineSegment(sketch, "E800", {"start": v(598.82, -55) * mm, "end": v(606.5, -56.14) * mm});
            skLineSegment(sketch, "E801", {"start": v(606.5, -56.14) * mm, "end": v(614.56, -56.82) * mm});
            skLineSegment(sketch, "E802", {"start": v(614.56, -56.82) * mm, "end": v(620.87, -57.05) * mm});
            skLineSegment(sketch, "E803", {"start": v(620.87, -57.05) * mm, "end": v(622.98, -57.05) * mm});
            skLineSegment(sketch, "E804", {"start": v(622.98, -57.05) * mm, "end": v(625.04, -57.05) * mm});
            skLineSegment(sketch, "E805", {"start": v(625.04, -57.05) * mm, "end": v(631.23, -56.79) * mm});
            skLineSegment(sketch, "E806", {"start": v(631.23, -56.79) * mm, "end": v(639.1, -56) * mm});
            skLineSegment(sketch, "E807", {"start": v(639.1, -56) * mm, "end": v(646.57, -54.67) * mm});
            skLineSegment(sketch, "E808", {"start": v(646.57, -54.67) * mm, "end": v(653.61, -52.84) * mm});
            skLineSegment(sketch, "E809", {"start": v(653.61, -52.84) * mm, "end": v(660.2, -50.5) * mm});
            skLineSegment(sketch, "E810", {"start": v(660.2, -50.5) * mm, "end": v(666.3, -47.67) * mm});
            skLineSegment(sketch, "E811", {"start": v(666.3, -47.67) * mm, "end": v(671.91, -44.34) * mm});
            skLineSegment(sketch, "E812", {"start": v(671.91, -44.34) * mm, "end": v(675.78, -41.54) * mm});
            skLineSegment(sketch, "E813", {"start": v(675.78, -41.54) * mm, "end": v(677, -40.52) * mm});
            skLineSegment(sketch, "E814", {"start": v(677, -40.52) * mm, "end": v(678.13, -39.56) * mm});
            skLineSegment(sketch, "E815", {"start": v(678.13, -39.56) * mm, "end": v(681.36, -36.43) * mm});
            skLineSegment(sketch, "E816", {"start": v(681.36, -36.43) * mm, "end": v(685.17, -31.98) * mm});
            skLineSegment(sketch, "E817", {"start": v(685.17, -31.98) * mm, "end": v(688.41, -27.18) * mm});
            skLineSegment(sketch, "E818", {"start": v(688.41, -27.18) * mm, "end": v(691.09, -22.07) * mm});
            skLineSegment(sketch, "E819", {"start": v(691.09, -22.07) * mm, "end": v(693.18, -16.65) * mm});
            skLineSegment(sketch, "E820", {"start": v(693.18, -16.65) * mm, "end": v(694.69, -10.94) * mm});
            skLineSegment(sketch, "E821", {"start": v(694.69, -10.94) * mm, "end": v(695.6, -4.97) * mm});
            skLineSegment(sketch, "E822", {"start": v(695.6, -4.97) * mm, "end": v(695.9, -0.3) * mm});
            skLineSegment(sketch, "E823", {"start": v(695.9, -0.3) * mm, "end": v(695.9, 1.26) * mm});
            skLineSegment(sketch, "E824", {"start": v(695.9, 1.26) * mm, "end": v(695.9, 3.15) * mm});
            skLineSegment(sketch, "E825", {"start": v(695.9, 3.15) * mm, "end": v(695.46, 8.82) * mm});
            skLineSegment(sketch, "E826", {"start": v(695.46, 8.82) * mm, "end": v(694.19, 15.66) * mm});
            skLineSegment(sketch, "E827", {"start": v(694.19, 15.66) * mm, "end": v(692.15, 21.84) * mm});
            skLineSegment(sketch, "E828", {"start": v(692.15, 21.84) * mm, "end": v(689.4, 27.38) * mm});
            skLineSegment(sketch, "E829", {"start": v(689.4, 27.38) * mm, "end": v(686.03, 32.35) * mm});
            skLineSegment(sketch, "E830", {"start": v(686.03, 32.35) * mm, "end": v(682.09, 36.77) * mm});
            skLineSegment(sketch, "E831", {"start": v(682.09, 36.77) * mm, "end": v(677.65, 40.7) * mm});
            skLineSegment(sketch, "E832", {"start": v(677.65, 40.7) * mm, "end": v(672.79, 44.2) * mm});
            skLineSegment(sketch, "E833", {"start": v(672.79, 44.2) * mm, "end": v(667.56, 47.27) * mm});
            skLineSegment(sketch, "E834", {"start": v(667.56, 47.27) * mm, "end": v(662.03, 50) * mm});
            skLineSegment(sketch, "E835", {"start": v(662.03, 50) * mm, "end": v(656.28, 52.4) * mm});
            skLineSegment(sketch, "E836", {"start": v(656.28, 52.4) * mm, "end": v(650.37, 54.54) * mm});
            skLineSegment(sketch, "E837", {"start": v(650.37, 54.54) * mm, "end": v(644.37, 56.46) * mm});
            skLineSegment(sketch, "E838", {"start": v(644.37, 56.46) * mm, "end": v(638.34, 58.2) * mm});
            skLineSegment(sketch, "E839", {"start": v(638.34, 58.2) * mm, "end": v(632.36, 59.8) * mm});
            skLineSegment(sketch, "E840", {"start": v(632.36, 59.8) * mm, "end": v(627.95, 60.93) * mm});
            skLineSegment(sketch, "E841", {"start": v(627.95, 60.93) * mm, "end": v(626.48, 61.3) * mm});
            skLineSegment(sketch, "E842", {"start": v(788, 204.63) * mm, "end": v(782.57, 208.03) * mm});
            skLineSegment(sketch, "E843", {"start": v(782.57, 208.03) * mm, "end": v(771.25, 192.19) * mm});
            skLineSegment(sketch, "E844", {"start": v(771.25, 192.19) * mm, "end": v(776.74, 188.22) * mm});
            skLineSegment(sketch, "E845", {"start": v(776.74, 188.22) * mm, "end": v(778.72, 186.78) * mm});
            skLineSegment(sketch, "E846", {"start": v(778.72, 186.78) * mm, "end": v(784.51, 182.24) * mm});
            skLineSegment(sketch, "E847", {"start": v(784.51, 182.24) * mm, "end": v(791.62, 176.07) * mm});
            skLineSegment(sketch, "E848", {"start": v(791.62, 176.07) * mm, "end": v(798.07, 169.69) * mm});
            skLineSegment(sketch, "E849", {"start": v(798.07, 169.69) * mm, "end": v(803.9, 163.04) * mm});
            skLineSegment(sketch, "E850", {"start": v(803.9, 163.04) * mm, "end": v(809.11, 156.12) * mm});
            skLineSegment(sketch, "E851", {"start": v(809.11, 156.12) * mm, "end": v(813.75, 148.88) * mm});
            skLineSegment(sketch, "E852", {"start": v(813.75, 148.88) * mm, "end": v(817.84, 141.3) * mm});
            skLineSegment(sketch, "E853", {"start": v(817.84, 141.3) * mm, "end": v(820.58, 135.36) * mm});
            skLineSegment(sketch, "E854", {"start": v(820.58, 135.36) * mm, "end": v(821.4, 133.34) * mm});
            skLineSegment(sketch, "E855", {"start": v(821.4, 133.34) * mm, "end": v(822.15, 131.46) * mm});
            skLineSegment(sketch, "E856", {"start": v(822.15, 131.46) * mm, "end": v(824.18, 125.73) * mm});
            skLineSegment(sketch, "E857", {"start": v(824.18, 125.73) * mm, "end": v(826.58, 117.67) * mm});
            skLineSegment(sketch, "E858", {"start": v(826.58, 117.67) * mm, "end": v(828.6, 109.12) * mm});
            skLineSegment(sketch, "E859", {"start": v(828.6, 109.12) * mm, "end": v(830.23, 100.03) * mm});
            skLineSegment(sketch, "E860", {"start": v(830.23, 100.03) * mm, "end": v(831.49, 90.37) * mm});
            skLineSegment(sketch, "E861", {"start": v(831.49, 90.37) * mm, "end": v(832.38, 80.1) * mm});
            skLineSegment(sketch, "E862", {"start": v(832.38, 80.1) * mm, "end": v(832.9, 69.15) * mm});
            skLineSegment(sketch, "E863", {"start": v(832.9, 69.15) * mm, "end": v(833.08, 60.42) * mm});
            skLineSegment(sketch, "E864", {"start": v(833.08, 60.42) * mm, "end": v(833.08, 57.5) * mm});
            skLineSegment(sketch, "E865", {"start": v(833.08, 57.5) * mm, "end": v(833.08, 54.6) * mm});
            skLineSegment(sketch, "E866", {"start": v(833.08, 54.6) * mm, "end": v(832.9, 45.87) * mm});
            skLineSegment(sketch, "E867", {"start": v(832.9, 45.87) * mm, "end": v(832.38, 34.93) * mm});
            skLineSegment(sketch, "E868", {"start": v(832.38, 34.93) * mm, "end": v(831.49, 24.65) * mm});
            skLineSegment(sketch, "E869", {"start": v(831.49, 24.65) * mm, "end": v(830.23, 14.98) * mm});
            skLineSegment(sketch, "E870", {"start": v(830.23, 14.98) * mm, "end": v(828.6, 5.9) * mm});
            skLineSegment(sketch, "E871", {"start": v(828.6, 5.9) * mm, "end": v(826.58, -2.66) * mm});
            skLineSegment(sketch, "E872", {"start": v(826.58, -2.66) * mm, "end": v(824.18, -10.72) * mm});
            skLineSegment(sketch, "E873", {"start": v(824.18, -10.72) * mm, "end": v(822.15, -16.45) * mm});
            skLineSegment(sketch, "E874", {"start": v(822.15, -16.45) * mm, "end": v(821.4, -18.32) * mm});
            skLineSegment(sketch, "E875", {"start": v(821.4, -18.32) * mm, "end": v(820.58, -20.34) * mm});
            skLineSegment(sketch, "E876", {"start": v(820.58, -20.34) * mm, "end": v(817.84, -26.28) * mm});
            skLineSegment(sketch, "E877", {"start": v(817.84, -26.28) * mm, "end": v(813.75, -33.86) * mm});
            skLineSegment(sketch, "E878", {"start": v(813.75, -33.86) * mm, "end": v(809.11, -41.1) * mm});
            skLineSegment(sketch, "E879", {"start": v(809.11, -41.1) * mm, "end": v(803.9, -48.03) * mm});
            skLineSegment(sketch, "E880", {"start": v(803.9, -48.03) * mm, "end": v(798.07, -54.67) * mm});
            skLineSegment(sketch, "E881", {"start": v(798.07, -54.67) * mm, "end": v(791.62, -61.06) * mm});
            skLineSegment(sketch, "E882", {"start": v(791.62, -61.06) * mm, "end": v(784.51, -67.23) * mm});
            skLineSegment(sketch, "E883", {"start": v(784.51, -67.23) * mm, "end": v(778.72, -71.76) * mm});
            skLineSegment(sketch, "E884", {"start": v(778.72, -71.76) * mm, "end": v(776.74, -73.2) * mm});
            skLineSegment(sketch, "E885", {"start": v(776.74, -73.2) * mm, "end": v(771.25, -77.17) * mm});
            skLineSegment(sketch, "E886", {"start": v(771.25, -77.17) * mm, "end": v(782.57, -93.01) * mm});
            skLineSegment(sketch, "E887", {"start": v(782.57, -93.01) * mm, "end": v(788, -89.62) * mm});
            skLineSegment(sketch, "E888", {"start": v(788, -89.62) * mm, "end": v(789.93, -88.42) * mm});
            skLineSegment(sketch, "E889", {"start": v(789.93, -88.42) * mm, "end": v(795.63, -84.66) * mm});
            skLineSegment(sketch, "E890", {"start": v(795.63, -84.66) * mm, "end": v(803.36, -79.2) * mm});
            skLineSegment(sketch, "E891", {"start": v(803.36, -79.2) * mm, "end": v(811.1, -73.23) * mm});
            skLineSegment(sketch, "E892", {"start": v(811.1, -73.23) * mm, "end": v(818.8, -66.73) * mm});
            skLineSegment(sketch, "E893", {"start": v(818.8, -66.73) * mm, "end": v(826.33, -59.68) * mm});
            skLineSegment(sketch, "E894", {"start": v(826.33, -59.68) * mm, "end": v(833.64, -52.08) * mm});
            skLineSegment(sketch, "E895", {"start": v(833.64, -52.08) * mm, "end": v(840.64, -43.91) * mm});
            skLineSegment(sketch, "E896", {"start": v(840.64, -43.91) * mm, "end": v(847.25, -35.16) * mm});
            skLineSegment(sketch, "E897", {"start": v(847.25, -35.16) * mm, "end": v(853.4, -25.8) * mm});
            skLineSegment(sketch, "E898", {"start": v(853.4, -25.8) * mm, "end": v(858.98, -15.85) * mm});
            skLineSegment(sketch, "E899", {"start": v(858.98, -15.85) * mm, "end": v(863.93, -5.26) * mm});
            skLineSegment(sketch, "E900", {"start": v(863.93, -5.26) * mm, "end": v(868.17, 5.96) * mm});
            skLineSegment(sketch, "E901", {"start": v(868.17, 5.96) * mm, "end": v(871.6, 17.84) * mm});
            skLineSegment(sketch, "E902", {"start": v(871.6, 17.84) * mm, "end": v(874.16, 30.38) * mm});
            skLineSegment(sketch, "E903", {"start": v(874.16, 30.38) * mm, "end": v(875.75, 43.6) * mm});
            skLineSegment(sketch, "E904", {"start": v(875.75, 43.6) * mm, "end": v(876.3, 54.03) * mm});
            skLineSegment(sketch, "E905", {"start": v(876.3, 54.03) * mm, "end": v(876.3, 57.5) * mm});
            skLineSegment(sketch, "E906", {"start": v(876.3, 57.5) * mm, "end": v(876.3, 60.99) * mm});
            skLineSegment(sketch, "E907", {"start": v(876.3, 60.99) * mm, "end": v(875.75, 71.42) * mm});
            skLineSegment(sketch, "E908", {"start": v(875.75, 71.42) * mm, "end": v(874.16, 84.64) * mm});
            skLineSegment(sketch, "E909", {"start": v(874.16, 84.64) * mm, "end": v(871.6, 97.18) * mm});
            skLineSegment(sketch, "E910", {"start": v(871.6, 97.18) * mm, "end": v(868.17, 109.05) * mm});
            skLineSegment(sketch, "E911", {"start": v(868.17, 109.05) * mm, "end": v(863.93, 120.28) * mm});
            skLineSegment(sketch, "E912", {"start": v(863.93, 120.28) * mm, "end": v(858.98, 130.86) * mm});
            skLineSegment(sketch, "E913", {"start": v(858.98, 130.86) * mm, "end": v(853.4, 140.82) * mm});
            skLineSegment(sketch, "E914", {"start": v(853.4, 140.82) * mm, "end": v(847.25, 150.17) * mm});
            skLineSegment(sketch, "E915", {"start": v(847.25, 150.17) * mm, "end": v(840.64, 158.93) * mm});
            skLineSegment(sketch, "E916", {"start": v(840.64, 158.93) * mm, "end": v(833.64, 167.1) * mm});
            skLineSegment(sketch, "E917", {"start": v(833.64, 167.1) * mm, "end": v(826.33, 174.7) * mm});
            skLineSegment(sketch, "E918", {"start": v(826.33, 174.7) * mm, "end": v(818.8, 181.74) * mm});
            skLineSegment(sketch, "E919", {"start": v(818.8, 181.74) * mm, "end": v(811.1, 188.24) * mm});
            skLineSegment(sketch, "E920", {"start": v(811.1, 188.24) * mm, "end": v(803.36, 194.22) * mm});
            skLineSegment(sketch, "E921", {"start": v(803.36, 194.22) * mm, "end": v(795.63, 199.68) * mm});
            skLineSegment(sketch, "E922", {"start": v(795.63, 199.68) * mm, "end": v(789.93, 203.43) * mm});
            skLineSegment(sketch, "E923", {"start": v(789.93, 203.43) * mm, "end": v(788, 204.63) * mm});
            skLineSegment(sketch, "E924", {"start": v(-349.78, -169.78) * mm, "end": v(-350.6, -169.51) * mm});
            skLineSegment(sketch, "E925", {"start": v(-350.6, -169.51) * mm, "end": v(-353.05, -168.62) * mm});
            skLineSegment(sketch, "E926", {"start": v(-353.05, -168.62) * mm, "end": v(-355.8, -167.44) * mm});
            skLineSegment(sketch, "E927", {"start": v(-355.8, -167.44) * mm, "end": v(-358.02, -166.22) * mm});
            skLineSegment(sketch, "E928", {"start": v(-358.02, -166.22) * mm, "end": v(-359.77, -164.93) * mm});
            skLineSegment(sketch, "E929", {"start": v(-359.77, -164.93) * mm, "end": v(-361.07, -163.54) * mm});
            skLineSegment(sketch, "E930", {"start": v(-361.07, -163.54) * mm, "end": v(-361.97, -162.02) * mm});
            skLineSegment(sketch, "E931", {"start": v(-361.97, -162.02) * mm, "end": v(-362.48, -160.34) * mm});
            skLineSegment(sketch, "E932", {"start": v(-362.48, -160.34) * mm, "end": v(-362.64, -158.94) * mm});
            skLineSegment(sketch, "E933", {"start": v(-362.64, -158.94) * mm, "end": v(-362.64, -158.47) * mm});
            skLineSegment(sketch, "E934", {"start": v(-362.64, -158.47) * mm, "end": v(-362.64, -157.84) * mm});
            skLineSegment(sketch, "E935", {"start": v(-362.64, -157.84) * mm, "end": v(-362.29, -155.96) * mm});
            skLineSegment(sketch, "E936", {"start": v(-362.29, -155.96) * mm, "end": v(-361.3, -153.92) * mm});
            skLineSegment(sketch, "E937", {"start": v(-361.3, -153.92) * mm, "end": v(-359.84, -152.3) * mm});
            skLineSegment(sketch, "E938", {"start": v(-359.84, -152.3) * mm, "end": v(-358.04, -151.07) * mm});
            skLineSegment(sketch, "E939", {"start": v(-358.04, -151.07) * mm, "end": v(-356.04, -150.18) * mm});
            skLineSegment(sketch, "E940", {"start": v(-356.04, -150.18) * mm, "end": v(-353.97, -149.6) * mm});
            skLineSegment(sketch, "E941", {"start": v(-353.97, -149.6) * mm, "end": v(-352, -149.28) * mm});
            skLineSegment(sketch, "E942", {"start": v(-352, -149.28) * mm, "end": v(-350.66, -149.18) * mm});
            skLineSegment(sketch, "E943", {"start": v(-350.66, -149.18) * mm, "end": v(-350.22, -149.18) * mm});
            skLineSegment(sketch, "E944", {"start": v(-350.22, -149.18) * mm, "end": v(-349.69, -149.18) * mm});
            skLineSegment(sketch, "E945", {"start": v(-349.69, -149.18) * mm, "end": v(-348.1, -149.32) * mm});
            skLineSegment(sketch, "E946", {"start": v(-348.1, -149.32) * mm, "end": v(-346.07, -149.7) * mm});
            skLineSegment(sketch, "E947", {"start": v(-346.07, -149.7) * mm, "end": v(-344.2, -150.25) * mm});
            skLineSegment(sketch, "E948", {"start": v(-344.2, -150.25) * mm, "end": v(-342.52, -150.89) * mm});
            skLineSegment(sketch, "E949", {"start": v(-342.52, -150.89) * mm, "end": v(-341.08, -151.54) * mm});
            skLineSegment(sketch, "E950", {"start": v(-341.08, -151.54) * mm, "end": v(-339.94, -152.14) * mm});
            skLineSegment(sketch, "E951", {"start": v(-339.94, -152.14) * mm, "end": v(-339.13, -152.61) * mm});
            skLineSegment(sketch, "E952", {"start": v(-339.13, -152.61) * mm, "end": v(-338.81, -152.81) * mm});
            skLineSegment(sketch, "E953", {"start": v(-338.81, -152.81) * mm, "end": v(-338.7, -152.88) * mm});
            skLineSegment(sketch, "E954", {"start": v(-338.7, -152.88) * mm, "end": v(-338.62, -152.94) * mm});
            skLineSegment(sketch, "E955", {"start": v(-338.62, -152.94) * mm, "end": v(-338.31, -153.12) * mm});
            skLineSegment(sketch, "E956", {"start": v(-338.31, -153.12) * mm, "end": v(-337.28, -153.48) * mm});
            skLineSegment(sketch, "E957", {"start": v(-337.28, -153.48) * mm, "end": v(-335.97, -153.48) * mm});
            skLineSegment(sketch, "E958", {"start": v(-335.97, -153.48) * mm, "end": v(-334.77, -152.96) * mm});
            skLineSegment(sketch, "E959", {"start": v(-334.77, -152.96) * mm, "end": v(-333.93, -152.22) * mm});
            skLineSegment(sketch, "E960", {"start": v(-333.93, -152.22) * mm, "end": v(-333.71, -151.93) * mm});
            skLineSegment(sketch, "E961", {"start": v(-333.71, -151.93) * mm, "end": v(-333.5, -151.58) * mm});
            skLineSegment(sketch, "E962", {"start": v(-333.5, -151.58) * mm, "end": v(-333.47, -151.51) * mm});
            skLineSegment(sketch, "E963", {"start": v(-333.47, -151.51) * mm, "end": v(-333.05, -150.84) * mm});
            skLineSegment(sketch, "E964", {"start": v(-333.05, -150.84) * mm, "end": v(-333.01, -150.79) * mm});
            skLineSegment(sketch, "E965", {"start": v(-333.01, -150.79) * mm, "end": v(-332.92, -150.65) * mm});
            skLineSegment(sketch, "E966", {"start": v(-332.92, -150.65) * mm, "end": v(-332.73, -150.36) * mm});
            skLineSegment(sketch, "E967", {"start": v(-332.73, -150.36) * mm, "end": v(-332.38, -149.34) * mm});
            skLineSegment(sketch, "E968", {"start": v(-332.38, -149.34) * mm, "end": v(-332.36, -148.03) * mm});
            skLineSegment(sketch, "E969", {"start": v(-332.36, -148.03) * mm, "end": v(-332.87, -146.8) * mm});
            skLineSegment(sketch, "E970", {"start": v(-332.87, -146.8) * mm, "end": v(-333.6, -145.96) * mm});
            skLineSegment(sketch, "E971", {"start": v(-333.6, -145.96) * mm, "end": v(-333.88, -145.74) * mm});
            skLineSegment(sketch, "E972", {"start": v(-333.88, -145.74) * mm, "end": v(-333.95, -145.7) * mm});
            skLineSegment(sketch, "E973", {"start": v(-333.95, -145.7) * mm, "end": v(-334.28, -145.48) * mm});
            skLineSegment(sketch, "E974", {"start": v(-334.28, -145.48) * mm, "end": v(-335.24, -144.9) * mm});
            skLineSegment(sketch, "E975", {"start": v(-335.24, -144.9) * mm, "end": v(-336.72, -144.12) * mm});
            skLineSegment(sketch, "E976", {"start": v(-336.72, -144.12) * mm, "end": v(-338.66, -143.25) * mm});
            skLineSegment(sketch, "E977", {"start": v(-338.66, -143.25) * mm, "end": v(-341.02, -142.38) * mm});
            skLineSegment(sketch, "E978", {"start": v(-341.02, -142.38) * mm, "end": v(-343.75, -141.63) * mm});
            skLineSegment(sketch, "E979", {"start": v(-343.75, -141.63) * mm, "end": v(-346.8, -141.1) * mm});
            skLineSegment(sketch, "E980", {"start": v(-346.8, -141.1) * mm, "end": v(-349.3, -140.9) * mm});
            skLineSegment(sketch, "E981", {"start": v(-349.3, -140.9) * mm, "end": v(-350.13, -140.9) * mm});
            skLineSegment(sketch, "E982", {"start": v(-350.13, -140.9) * mm, "end": v(-351.47, -140.9) * mm});
            skLineSegment(sketch, "E983", {"start": v(-351.47, -140.9) * mm, "end": v(-355.47, -141.37) * mm});
            skLineSegment(sketch, "E984", {"start": v(-355.47, -141.37) * mm, "end": v(-359.94, -142.66) * mm});
            skLineSegment(sketch, "E985", {"start": v(-359.94, -142.66) * mm, "end": v(-363.58, -144.61) * mm});
            skLineSegment(sketch, "E986", {"start": v(-363.58, -144.61) * mm, "end": v(-366.45, -147.07) * mm});
            skLineSegment(sketch, "E987", {"start": v(-366.45, -147.07) * mm, "end": v(-368.6, -149.85) * mm});
            skLineSegment(sketch, "E988", {"start": v(-368.6, -149.85) * mm, "end": v(-370.06, -152.8) * mm});
            skLineSegment(sketch, "E989", {"start": v(-370.06, -152.8) * mm, "end": v(-370.9, -155.76) * mm});
            skLineSegment(sketch, "E990", {"start": v(-370.9, -155.76) * mm, "end": v(-371.18, -157.86) * mm});
            skLineSegment(sketch, "E991", {"start": v(-371.18, -157.86) * mm, "end": v(-371.18, -158.56) * mm});
            skLineSegment(sketch, "E992", {"start": v(-371.18, -158.56) * mm, "end": v(-371.18, -159.58) * mm});
            skLineSegment(sketch, "E993", {"start": v(-371.18, -159.58) * mm, "end": v(-370.79, -162.64) * mm});
            skLineSegment(sketch, "E994", {"start": v(-370.79, -162.64) * mm, "end": v(-369.68, -166.07) * mm});
            skLineSegment(sketch, "E995", {"start": v(-369.68, -166.07) * mm, "end": v(-367.93, -168.95) * mm});
            skLineSegment(sketch, "E996", {"start": v(-367.93, -168.95) * mm, "end": v(-365.65, -171.34) * mm});
            skLineSegment(sketch, "E997", {"start": v(-365.65, -171.34) * mm, "end": v(-362.9, -173.35) * mm});
            skLineSegment(sketch, "E998", {"start": v(-362.9, -173.35) * mm, "end": v(-359.8, -175.04) * mm});
            skLineSegment(sketch, "E999", {"start": v(-359.8, -175.04) * mm, "end": v(-356.43, -176.5) * mm});
            skLineSegment(sketch, "E1000", {"start": v(-356.43, -176.5) * mm, "end": v(-353.76, -177.52) * mm});
            skLineSegment(sketch, "E1001", {"start": v(-353.76, -177.52) * mm, "end": v(-352.86, -177.83) * mm});
            skLineSegment(sketch, "E1002", {"start": v(-352.86, -177.83) * mm, "end": v(-351.87, -178.17) * mm});
            skLineSegment(sketch, "E1003", {"start": v(-351.87, -178.17) * mm, "end": v(-348.91, -179.26) * mm});
            skLineSegment(sketch, "E1004", {"start": v(-348.91, -179.26) * mm, "end": v(-345.64, -180.66) * mm});
            skLineSegment(sketch, "E1005", {"start": v(-345.64, -180.66) * mm, "end": v(-342.98, -182.07) * mm});
            skLineSegment(sketch, "E1006", {"start": v(-342.98, -182.07) * mm, "end": v(-340.9, -183.52) * mm});
            skLineSegment(sketch, "E1007", {"start": v(-340.9, -183.52) * mm, "end": v(-339.37, -185.04) * mm});
            skLineSegment(sketch, "E1008", {"start": v(-339.37, -185.04) * mm, "end": v(-338.32, -186.69) * mm});
            skLineSegment(sketch, "E1009", {"start": v(-338.32, -186.69) * mm, "end": v(-337.73, -188.48) * mm});
            skLineSegment(sketch, "E1010", {"start": v(-337.73, -188.48) * mm, "end": v(-337.54, -189.96) * mm});
            skLineSegment(sketch, "E1011", {"start": v(-337.54, -189.96) * mm, "end": v(-337.54, -190.46) * mm});
            skLineSegment(sketch, "E1012", {"start": v(-337.54, -190.46) * mm, "end": v(-337.54, -190.92) * mm});
            skLineSegment(sketch, "E1013", {"start": v(-337.54, -190.92) * mm, "end": v(-337.8, -192.32) * mm});
            skLineSegment(sketch, "E1014", {"start": v(-337.8, -192.32) * mm, "end": v(-338.53, -194.07) * mm});
            skLineSegment(sketch, "E1015", {"start": v(-338.53, -194.07) * mm, "end": v(-339.68, -195.66) * mm});
            skLineSegment(sketch, "E1016", {"start": v(-339.68, -195.66) * mm, "end": v(-341.2, -197.05) * mm});
            skLineSegment(sketch, "E1017", {"start": v(-341.2, -197.05) * mm, "end": v(-343.03, -198.2) * mm});
            skLineSegment(sketch, "E1018", {"start": v(-343.03, -198.2) * mm, "end": v(-345.12, -199.08) * mm});
            skLineSegment(sketch, "E1019", {"start": v(-345.12, -199.08) * mm, "end": v(-347.43, -199.64) * mm});
            skLineSegment(sketch, "E1020", {"start": v(-347.43, -199.64) * mm, "end": v(-349.26, -199.83) * mm});
            skLineSegment(sketch, "E1021", {"start": v(-349.26, -199.83) * mm, "end": v(-349.87, -199.83) * mm});
            skLineSegment(sketch, "E1022", {"start": v(-349.87, -199.83) * mm, "end": v(-350.51, -199.83) * mm});
            skLineSegment(sketch, "E1023", {"start": v(-350.51, -199.83) * mm, "end": v(-352.43, -199.65) * mm});
            skLineSegment(sketch, "E1024", {"start": v(-352.43, -199.65) * mm, "end": v(-354.82, -199.14) * mm});
            skLineSegment(sketch, "E1025", {"start": v(-354.82, -199.14) * mm, "end": v(-357.02, -198.4) * mm});
            skLineSegment(sketch, "E1026", {"start": v(-357.02, -198.4) * mm, "end": v(-359.01, -197.48) * mm});
            skLineSegment(sketch, "E1027", {"start": v(-359.01, -197.48) * mm, "end": v(-360.76, -196.48) * mm});
            skLineSegment(sketch, "E1028", {"start": v(-360.76, -196.48) * mm, "end": v(-362.26, -195.48) * mm});
            skLineSegment(sketch, "E1029", {"start": v(-362.26, -195.48) * mm, "end": v(-363.48, -194.54) * mm});
            skLineSegment(sketch, "E1030", {"start": v(-363.48, -194.54) * mm, "end": v(-364.17, -193.96) * mm});
            skLineSegment(sketch, "E1031", {"start": v(-364.17, -193.96) * mm, "end": v(-364.4, -193.76) * mm});
            skLineSegment(sketch, "E1032", {"start": v(-364.4, -193.76) * mm, "end": v(-364.46, -193.7) * mm});
            skLineSegment(sketch, "E1033", {"start": v(-364.46, -193.7) * mm, "end": v(-364.7, -193.5) * mm});
            skLineSegment(sketch, "E1034", {"start": v(-364.7, -193.5) * mm, "end": v(-365.52, -193.04) * mm});
            skLineSegment(sketch, "E1035", {"start": v(-365.52, -193.04) * mm, "end": v(-366.79, -192.8) * mm});
            skLineSegment(sketch, "E1036", {"start": v(-366.79, -192.8) * mm, "end": v(-368.17, -193.14) * mm});
            skLineSegment(sketch, "E1037", {"start": v(-368.17, -193.14) * mm, "end": v(-369.29, -193.93) * mm});
            skLineSegment(sketch, "E1038", {"start": v(-369.29, -193.93) * mm, "end": v(-369.57, -194.26) * mm});
            skLineSegment(sketch, "E1039", {"start": v(-369.57, -194.26) * mm, "end": v(-370.49, -195.46) * mm});
            skLineSegment(sketch, "E1040", {"start": v(-370.49, -195.46) * mm, "end": v(-370.55, -195.55) * mm});
            skLineSegment(sketch, "E1041", {"start": v(-370.55, -195.55) * mm, "end": v(-370.73, -195.82) * mm});
            skLineSegment(sketch, "E1042", {"start": v(-370.73, -195.82) * mm, "end": v(-370.97, -196.29) * mm});
            skLineSegment(sketch, "E1043", {"start": v(-370.97, -196.29) * mm, "end": v(-371.16, -196.84) * mm});
            skLineSegment(sketch, "E1044", {"start": v(-371.16, -196.84) * mm, "end": v(-371.27, -197.47) * mm});
            skLineSegment(sketch, "E1045", {"start": v(-371.27, -197.47) * mm, "end": v(-371.25, -198.14) * mm});
            skLineSegment(sketch, "E1046", {"start": v(-371.25, -198.14) * mm, "end": v(-371.04, -198.86) * mm});
            skLineSegment(sketch, "E1047", {"start": v(-371.04, -198.86) * mm, "end": v(-370.6, -199.6) * mm});
            skLineSegment(sketch, "E1048", {"start": v(-370.6, -199.6) * mm, "end": v(-370.08, -200.17) * mm});
            skLineSegment(sketch, "E1049", {"start": v(-370.08, -200.17) * mm, "end": v(-369.89, -200.33) * mm});
            skLineSegment(sketch, "E1050", {"start": v(-369.89, -200.33) * mm, "end": v(-369.69, -200.52) * mm});
            skLineSegment(sketch, "E1051", {"start": v(-369.69, -200.52) * mm, "end": v(-369.05, -201.06) * mm});
            skLineSegment(sketch, "E1052", {"start": v(-369.05, -201.06) * mm, "end": v(-367.69, -202.11) * mm});
            skLineSegment(sketch, "E1053", {"start": v(-367.69, -202.11) * mm, "end": v(-365.82, -203.37) * mm});
            skLineSegment(sketch, "E1054", {"start": v(-365.82, -203.37) * mm, "end": v(-363.47, -204.7) * mm});
            skLineSegment(sketch, "E1055", {"start": v(-363.47, -204.7) * mm, "end": v(-360.68, -205.95) * mm});
            skLineSegment(sketch, "E1056", {"start": v(-360.68, -205.95) * mm, "end": v(-357.48, -207.02) * mm});
            skLineSegment(sketch, "E1057", {"start": v(-357.48, -207.02) * mm, "end": v(-353.9, -207.75) * mm});
            skLineSegment(sketch, "E1058", {"start": v(-353.9, -207.75) * mm, "end": v(-350.95, -208.03) * mm});
            skLineSegment(sketch, "E1059", {"start": v(-350.95, -208.03) * mm, "end": v(-349.96, -208.03) * mm});
            skLineSegment(sketch, "E1060", {"start": v(-349.96, -208.03) * mm, "end": v(-348.9, -208.03) * mm});
            skLineSegment(sketch, "E1061", {"start": v(-348.9, -208.03) * mm, "end": v(-345.69, -207.66) * mm});
            skLineSegment(sketch, "E1062", {"start": v(-345.69, -207.66) * mm, "end": v(-341.7, -206.63) * mm});
            skLineSegment(sketch, "E1063", {"start": v(-341.7, -206.63) * mm, "end": v(-338.1, -205) * mm});
            skLineSegment(sketch, "E1064", {"start": v(-338.1, -205) * mm, "end": v(-334.96, -202.82) * mm});
            skLineSegment(sketch, "E1065", {"start": v(-334.96, -202.82) * mm, "end": v(-332.37, -200.2) * mm});
            skLineSegment(sketch, "E1066", {"start": v(-332.37, -200.2) * mm, "end": v(-330.41, -197.18) * mm});
            skLineSegment(sketch, "E1067", {"start": v(-330.41, -197.18) * mm, "end": v(-329.17, -193.85) * mm});
            skLineSegment(sketch, "E1068", {"start": v(-329.17, -193.85) * mm, "end": v(-328.74, -191.17) * mm});
            skLineSegment(sketch, "E1069", {"start": v(-328.74, -191.17) * mm, "end": v(-328.74, -190.28) * mm});
            skLineSegment(sketch, "E1070", {"start": v(-328.74, -190.28) * mm, "end": v(-328.74, -189.22) * mm});
            skLineSegment(sketch, "E1071", {"start": v(-328.74, -189.22) * mm, "end": v(-329.19, -186.03) * mm});
            skLineSegment(sketch, "E1072", {"start": v(-329.19, -186.03) * mm, "end": v(-330.46, -182.44) * mm});
            skLineSegment(sketch, "E1073", {"start": v(-330.46, -182.44) * mm, "end": v(-332.47, -179.4) * mm});
            skLineSegment(sketch, "E1074", {"start": v(-332.47, -179.4) * mm, "end": v(-335.1, -176.86) * mm});
            skLineSegment(sketch, "E1075", {"start": v(-335.1, -176.86) * mm, "end": v(-338.24, -174.7) * mm});
            skLineSegment(sketch, "E1076", {"start": v(-338.24, -174.7) * mm, "end": v(-341.8, -172.87) * mm});
            skLineSegment(sketch, "E1077", {"start": v(-341.8, -172.87) * mm, "end": v(-345.69, -171.25) * mm});
            skLineSegment(sketch, "E1078", {"start": v(-345.69, -171.25) * mm, "end": v(-348.75, -170.13) * mm});
            skLineSegment(sketch, "E1079", {"start": v(-348.75, -170.13) * mm, "end": v(-349.78, -169.78) * mm});
            skLineSegment(sketch, "E1080", {"start": v(-294.04, -176.97) * mm, "end": v(-294.04, -150.4) * mm});
            skLineSegment(sketch, "E1081", {"start": v(-294.04, -150.4) * mm, "end": v(-280.83, -150.4) * mm});
            skLineSegment(sketch, "E1082", {"start": v(-280.83, -150.4) * mm, "end": v(-280.15, -150.4) * mm});
            skLineSegment(sketch, "E1083", {"start": v(-280.15, -150.4) * mm, "end": v(-278.1, -150.66) * mm});
            skLineSegment(sketch, "E1084", {"start": v(-278.1, -150.66) * mm, "end": v(-275.57, -151.42) * mm});
            skLineSegment(sketch, "E1085", {"start": v(-275.57, -151.42) * mm, "end": v(-273.27, -152.63) * mm});
            skLineSegment(sketch, "E1086", {"start": v(-273.27, -152.63) * mm, "end": v(-271.26, -154.22) * mm});
            skLineSegment(sketch, "E1087", {"start": v(-271.26, -154.22) * mm, "end": v(-269.6, -156.14) * mm});
            skLineSegment(sketch, "E1088", {"start": v(-269.6, -156.14) * mm, "end": v(-268.35, -158.36) * mm});
            skLineSegment(sketch, "E1089", {"start": v(-268.35, -158.36) * mm, "end": v(-267.57, -160.8) * mm});
            skLineSegment(sketch, "E1090", {"start": v(-267.57, -160.8) * mm, "end": v(-267.29, -162.77) * mm});
            skLineSegment(sketch, "E1091", {"start": v(-267.29, -162.77) * mm, "end": v(-267.29, -163.42) * mm});
            skLineSegment(sketch, "E1092", {"start": v(-267.29, -163.42) * mm, "end": v(-267.29, -164.1) * mm});
            skLineSegment(sketch, "E1093", {"start": v(-267.29, -164.1) * mm, "end": v(-267.56, -166.15) * mm});
            skLineSegment(sketch, "E1094", {"start": v(-267.56, -166.15) * mm, "end": v(-268.35, -168.7) * mm});
            skLineSegment(sketch, "E1095", {"start": v(-268.35, -168.7) * mm, "end": v(-269.6, -171) * mm});
            skLineSegment(sketch, "E1096", {"start": v(-269.6, -171) * mm, "end": v(-271.24, -173) * mm});
            skLineSegment(sketch, "E1097", {"start": v(-271.24, -173) * mm, "end": v(-273.23, -174.65) * mm});
            skLineSegment(sketch, "E1098", {"start": v(-273.23, -174.65) * mm, "end": v(-275.52, -175.9) * mm});
            skLineSegment(sketch, "E1099", {"start": v(-275.52, -175.9) * mm, "end": v(-278.04, -176.7) * mm});
            skLineSegment(sketch, "E1100", {"start": v(-278.04, -176.7) * mm, "end": v(-280.07, -176.97) * mm});
            skLineSegment(sketch, "E1101", {"start": v(-280.07, -176.97) * mm, "end": v(-280.75, -176.97) * mm});
            skLineSegment(sketch, "E1102", {"start": v(-280.75, -176.97) * mm, "end": v(-294.04, -176.97) * mm});
            skLineSegment(sketch, "E1103", {"start": v(-280.58, -141.77) * mm, "end": v(-299.26, -141.77) * mm});
            skLineSegment(sketch, "E1104", {"start": v(-299.26, -141.77) * mm, "end": v(-299.6, -141.77) * mm});
            skLineSegment(sketch, "E1105", {"start": v(-299.6, -141.77) * mm, "end": v(-300.59, -142.04) * mm});
            skLineSegment(sketch, "E1106", {"start": v(-300.59, -142.04) * mm, "end": v(-301.67, -142.77) * mm});
            skLineSegment(sketch, "E1107", {"start": v(-301.67, -142.77) * mm, "end": v(-302.4, -143.85) * mm});
            skLineSegment(sketch, "E1108", {"start": v(-302.4, -143.85) * mm, "end": v(-302.66, -144.84) * mm});
            skLineSegment(sketch, "E1109", {"start": v(-302.66, -144.84) * mm, "end": v(-302.66, -145.17) * mm});
            skLineSegment(sketch, "E1110", {"start": v(-302.66, -145.17) * mm, "end": v(-302.66, -203.76) * mm});
            skLineSegment(sketch, "E1111", {"start": v(-302.66, -203.76) * mm, "end": v(-302.66, -204.09) * mm});
            skLineSegment(sketch, "E1112", {"start": v(-302.66, -204.09) * mm, "end": v(-302.4, -205.08) * mm});
            skLineSegment(sketch, "E1113", {"start": v(-302.4, -205.08) * mm, "end": v(-301.67, -206.16) * mm});
            skLineSegment(sketch, "E1114", {"start": v(-301.67, -206.16) * mm, "end": v(-300.59, -206.89) * mm});
            skLineSegment(sketch, "E1115", {"start": v(-300.59, -206.89) * mm, "end": v(-299.6, -207.16) * mm});
            skLineSegment(sketch, "E1116", {"start": v(-299.6, -207.16) * mm, "end": v(-299.26, -207.16) * mm});
            skLineSegment(sketch, "E1117", {"start": v(-299.26, -207.16) * mm, "end": v(-297.7, -207.16) * mm});
            skLineSegment(sketch, "E1118", {"start": v(-297.7, -207.16) * mm, "end": v(-297.34, -207.16) * mm});
            skLineSegment(sketch, "E1119", {"start": v(-297.34, -207.16) * mm, "end": v(-296.26, -206.9) * mm});
            skLineSegment(sketch, "E1120", {"start": v(-296.26, -206.9) * mm, "end": v(-295.1, -206.17) * mm});
            skLineSegment(sketch, "E1121", {"start": v(-295.1, -206.17) * mm, "end": v(-294.32, -205.1) * mm});
            skLineSegment(sketch, "E1122", {"start": v(-294.32, -205.1) * mm, "end": v(-294.04, -204.09) * mm});
            skLineSegment(sketch, "E1123", {"start": v(-294.04, -204.09) * mm, "end": v(-294.04, -203.76) * mm});
            skLineSegment(sketch, "E1124", {"start": v(-294.04, -203.76) * mm, "end": v(-294.04, -185.51) * mm});
            skLineSegment(sketch, "E1125", {"start": v(-294.04, -185.51) * mm, "end": v(-280.49, -185.51) * mm});
            skLineSegment(sketch, "E1126", {"start": v(-280.49, -185.51) * mm, "end": v(-279.4, -185.51) * mm});
            skLineSegment(sketch, "E1127", {"start": v(-279.4, -185.51) * mm, "end": v(-276.1, -185.06) * mm});
            skLineSegment(sketch, "E1128", {"start": v(-276.1, -185.06) * mm, "end": v(-272, -183.78) * mm});
            skLineSegment(sketch, "E1129", {"start": v(-272, -183.78) * mm, "end": v(-268.3, -181.75) * mm});
            skLineSegment(sketch, "E1130", {"start": v(-268.3, -181.75) * mm, "end": v(-265.06, -179.06) * mm});
            skLineSegment(sketch, "E1131", {"start": v(-265.06, -179.06) * mm, "end": v(-262.4, -175.8) * mm});
            skLineSegment(sketch, "E1132", {"start": v(-262.4, -175.8) * mm, "end": v(-260.38, -172.07) * mm});
            skLineSegment(sketch, "E1133", {"start": v(-260.38, -172.07) * mm, "end": v(-259.1, -167.94) * mm});
            skLineSegment(sketch, "E1134", {"start": v(-259.1, -167.94) * mm, "end": v(-258.66, -164.62) * mm});
            skLineSegment(sketch, "E1135", {"start": v(-258.66, -164.62) * mm, "end": v(-258.66, -163.51) * mm});
            skLineSegment(sketch, "E1136", {"start": v(-258.66, -163.51) * mm, "end": v(-258.66, -162.42) * mm});
            skLineSegment(sketch, "E1137", {"start": v(-258.66, -162.42) * mm, "end": v(-259.1, -159.13) * mm});
            skLineSegment(sketch, "E1138", {"start": v(-259.1, -159.13) * mm, "end": v(-260.39, -155.06) * mm});
            skLineSegment(sketch, "E1139", {"start": v(-260.39, -155.06) * mm, "end": v(-262.4, -151.36) * mm});
            skLineSegment(sketch, "E1140", {"start": v(-262.4, -151.36) * mm, "end": v(-265.09, -148.15) * mm});
            skLineSegment(sketch, "E1141", {"start": v(-265.09, -148.15) * mm, "end": v(-268.33, -145.49) * mm});
            skLineSegment(sketch, "E1142", {"start": v(-268.33, -145.49) * mm, "end": v(-272.05, -143.48) * mm});
            skLineSegment(sketch, "E1143", {"start": v(-272.05, -143.48) * mm, "end": v(-276.16, -142.21) * mm});
            skLineSegment(sketch, "E1144", {"start": v(-276.16, -142.21) * mm, "end": v(-279.47, -141.77) * mm});
            skLineSegment(sketch, "E1145", {"start": v(-279.47, -141.77) * mm, "end": v(-280.58, -141.77) * mm});
            skLineSegment(sketch, "E1146", {"start": v(-226.16, -182.45) * mm, "end": v(-214.42, -155.26) * mm});
            skLineSegment(sketch, "E1147", {"start": v(-214.42, -155.26) * mm, "end": v(-202.89, -182.45) * mm});
            skLineSegment(sketch, "E1148", {"start": v(-202.89, -182.45) * mm, "end": v(-226.16, -182.45) * mm});
            skLineSegment(sketch, "E1149", {"start": v(-211.11, -142.43) * mm, "end": v(-211.16, -142.32) * mm});
            skLineSegment(sketch, "E1150", {"start": v(-211.16, -142.32) * mm, "end": v(-211.24, -142.17) * mm});
            skLineSegment(sketch, "E1151", {"start": v(-211.24, -142.17) * mm, "end": v(-211.53, -141.74) * mm});
            skLineSegment(sketch, "E1152", {"start": v(-211.53, -141.74) * mm, "end": v(-212.15, -141.13) * mm});
            skLineSegment(sketch, "E1153", {"start": v(-212.15, -141.13) * mm, "end": v(-213.06, -140.66) * mm});
            skLineSegment(sketch, "E1154", {"start": v(-213.06, -140.66) * mm, "end": v(-214, -140.46) * mm});
            skLineSegment(sketch, "E1155", {"start": v(-214, -140.46) * mm, "end": v(-214.32, -140.46) * mm});
            skLineSegment(sketch, "E1156", {"start": v(-214.32, -140.46) * mm, "end": v(-214.58, -140.46) * mm});
            skLineSegment(sketch, "E1157", {"start": v(-214.58, -140.46) * mm, "end": v(-214.82, -140.46) * mm});
            skLineSegment(sketch, "E1158", {"start": v(-214.82, -140.46) * mm, "end": v(-215.52, -140.6) * mm});
            skLineSegment(sketch, "E1159", {"start": v(-215.52, -140.6) * mm, "end": v(-216.38, -140.97) * mm});
            skLineSegment(sketch, "E1160", {"start": v(-216.38, -140.97) * mm, "end": v(-217.11, -141.55) * mm});
            skLineSegment(sketch, "E1161", {"start": v(-217.11, -141.55) * mm, "end": v(-217.55, -142.1) * mm});
            skLineSegment(sketch, "E1162", {"start": v(-217.55, -142.1) * mm, "end": v(-217.65, -142.3) * mm});
            skLineSegment(sketch, "E1163", {"start": v(-217.65, -142.3) * mm, "end": v(-244.47, -202.92) * mm});
            skLineSegment(sketch, "E1164", {"start": v(-244.47, -202.92) * mm, "end": v(-244.52, -203.04) * mm});
            skLineSegment(sketch, "E1165", {"start": v(-244.52, -203.04) * mm, "end": v(-244.61, -203.28) * mm});
            skLineSegment(sketch, "E1166", {"start": v(-244.61, -203.28) * mm, "end": v(-244.76, -204.03) * mm});
            skLineSegment(sketch, "E1167", {"start": v(-244.76, -204.03) * mm, "end": v(-244.72, -204.85) * mm});
            skLineSegment(sketch, "E1168", {"start": v(-244.72, -204.85) * mm, "end": v(-244.52, -205.49) * mm});
            skLineSegment(sketch, "E1169", {"start": v(-244.52, -205.49) * mm, "end": v(-244.35, -205.83) * mm});
            skLineSegment(sketch, "E1170", {"start": v(-244.35, -205.83) * mm, "end": v(-244.27, -205.94) * mm});
            skLineSegment(sketch, "E1171", {"start": v(-244.27, -205.94) * mm, "end": v(-244.14, -206.13) * mm});
            skLineSegment(sketch, "E1172", {"start": v(-244.14, -206.13) * mm, "end": v(-243.22, -206.84) * mm});
            skLineSegment(sketch, "E1173", {"start": v(-243.22, -206.84) * mm, "end": v(-242.15, -207.16) * mm});
            skLineSegment(sketch, "E1174", {"start": v(-242.15, -207.16) * mm, "end": v(-241.79, -207.16) * mm});
            skLineSegment(sketch, "E1175", {"start": v(-241.79, -207.16) * mm, "end": v(-239.35, -207.16) * mm});
            skLineSegment(sketch, "E1176", {"start": v(-239.35, -207.16) * mm, "end": v(-239.1, -207.16) * mm});
            skLineSegment(sketch, "E1177", {"start": v(-239.1, -207.16) * mm, "end": v(-238.36, -207.01) * mm});
            skLineSegment(sketch, "E1178", {"start": v(-238.36, -207.01) * mm, "end": v(-237.45, -206.6) * mm});
            skLineSegment(sketch, "E1179", {"start": v(-237.45, -206.6) * mm, "end": v(-236.68, -205.96) * mm});
            skLineSegment(sketch, "E1180", {"start": v(-236.68, -205.96) * mm, "end": v(-236.22, -205.34) * mm});
            skLineSegment(sketch, "E1181", {"start": v(-236.22, -205.34) * mm, "end": v(-236.1, -205.12) * mm});
            skLineSegment(sketch, "E1182", {"start": v(-236.1, -205.12) * mm, "end": v(-229.7, -190.38) * mm});
            skLineSegment(sketch, "E1183", {"start": v(-229.7, -190.38) * mm, "end": v(-199.46, -190.38) * mm});
            skLineSegment(sketch, "E1184", {"start": v(-199.46, -190.38) * mm, "end": v(-193.02, -205.02) * mm});
            skLineSegment(sketch, "E1185", {"start": v(-193.02, -205.02) * mm, "end": v(-192.97, -205.12) * mm});
            skLineSegment(sketch, "E1186", {"start": v(-192.97, -205.12) * mm, "end": v(-192.85, -205.34) * mm});
            skLineSegment(sketch, "E1187", {"start": v(-192.85, -205.34) * mm, "end": v(-192.4, -205.96) * mm});
            skLineSegment(sketch, "E1188", {"start": v(-192.4, -205.96) * mm, "end": v(-191.62, -206.6) * mm});
            skLineSegment(sketch, "E1189", {"start": v(-191.62, -206.6) * mm, "end": v(-190.71, -207.01) * mm});
            skLineSegment(sketch, "E1190", {"start": v(-190.71, -207.01) * mm, "end": v(-189.97, -207.16) * mm});
            skLineSegment(sketch, "E1191", {"start": v(-189.97, -207.16) * mm, "end": v(-189.72, -207.16) * mm});
            skLineSegment(sketch, "E1192", {"start": v(-189.72, -207.16) * mm, "end": v(-187.46, -207.16) * mm});
            skLineSegment(sketch, "E1193", {"start": v(-187.46, -207.16) * mm, "end": v(-187.22, -207.16) * mm});
            skLineSegment(sketch, "E1194", {"start": v(-187.22, -207.16) * mm, "end": v(-186.5, -207.05) * mm});
            skLineSegment(sketch, "E1195", {"start": v(-186.5, -207.05) * mm, "end": v(-185.76, -206.76) * mm});
            skLineSegment(sketch, "E1196", {"start": v(-185.76, -206.76) * mm, "end": v(-185.22, -206.37) * mm});
            skLineSegment(sketch, "E1197", {"start": v(-185.22, -206.37) * mm, "end": v(-184.92, -206.07) * mm});
            skLineSegment(sketch, "E1198", {"start": v(-184.92, -206.07) * mm, "end": v(-184.84, -205.95) * mm});
            skLineSegment(sketch, "E1199", {"start": v(-184.84, -205.95) * mm, "end": v(-184.76, -205.84) * mm});
            skLineSegment(sketch, "E1200", {"start": v(-184.76, -205.84) * mm, "end": v(-184.57, -205.47) * mm});
            skLineSegment(sketch, "E1201", {"start": v(-184.57, -205.47) * mm, "end": v(-184.37, -204.84) * mm});
            skLineSegment(sketch, "E1202", {"start": v(-184.37, -204.84) * mm, "end": v(-184.33, -204.06) * mm});
            skLineSegment(sketch, "E1203", {"start": v(-184.33, -204.06) * mm, "end": v(-184.44, -203.36) * mm});
            skLineSegment(sketch, "E1204", {"start": v(-184.44, -203.36) * mm, "end": v(-184.52, -203.13) * mm});
            skLineSegment(sketch, "E1205", {"start": v(-184.52, -203.13) * mm, "end": v(-211.11, -142.43) * mm});
            skLineSegment(sketch, "E1206", {"start": v(-119.9, -170.71) * mm, "end": v(-132.5, -170.71) * mm});
            skLineSegment(sketch, "E1207", {"start": v(-132.5, -170.71) * mm, "end": v(-132.5, -157.95) * mm});
            skLineSegment(sketch, "E1208", {"start": v(-132.5, -157.95) * mm, "end": v(-132.5, -157.62) * mm});
            skLineSegment(sketch, "E1209", {"start": v(-132.5, -157.62) * mm, "end": v(-132.76, -156.66) * mm});
            skLineSegment(sketch, "E1210", {"start": v(-132.76, -156.66) * mm, "end": v(-133.49, -155.6) * mm});
            skLineSegment(sketch, "E1211", {"start": v(-133.49, -155.6) * mm, "end": v(-134.57, -154.9) * mm});
            skLineSegment(sketch, "E1212", {"start": v(-134.57, -154.9) * mm, "end": v(-135.56, -154.63) * mm});
            skLineSegment(sketch, "E1213", {"start": v(-135.56, -154.63) * mm, "end": v(-135.9, -154.63) * mm});
            skLineSegment(sketch, "E1214", {"start": v(-135.9, -154.63) * mm, "end": v(-137.29, -154.63) * mm});
            skLineSegment(sketch, "E1215", {"start": v(-137.29, -154.63) * mm, "end": v(-137.61, -154.63) * mm});
            skLineSegment(sketch, "E1216", {"start": v(-137.61, -154.63) * mm, "end": v(-138.61, -154.9) * mm});
            skLineSegment(sketch, "E1217", {"start": v(-138.61, -154.9) * mm, "end": v(-139.69, -155.6) * mm});
            skLineSegment(sketch, "E1218", {"start": v(-139.69, -155.6) * mm, "end": v(-140.42, -156.66) * mm});
            skLineSegment(sketch, "E1219", {"start": v(-140.42, -156.66) * mm, "end": v(-140.68, -157.62) * mm});
            skLineSegment(sketch, "E1220", {"start": v(-140.68, -157.62) * mm, "end": v(-140.68, -157.95) * mm});
            skLineSegment(sketch, "E1221", {"start": v(-140.68, -157.95) * mm, "end": v(-140.68, -170.71) * mm});
            skLineSegment(sketch, "E1222", {"start": v(-140.68, -170.71) * mm, "end": v(-153.36, -170.71) * mm});
            skLineSegment(sketch, "E1223", {"start": v(-153.36, -170.71) * mm, "end": v(-153.7, -170.71) * mm});
            skLineSegment(sketch, "E1224", {"start": v(-153.7, -170.71) * mm, "end": v(-154.69, -170.98) * mm});
            skLineSegment(sketch, "E1225", {"start": v(-154.69, -170.98) * mm, "end": v(-155.77, -171.71) * mm});
            skLineSegment(sketch, "E1226", {"start": v(-155.77, -171.71) * mm, "end": v(-156.5, -172.8) * mm});
            skLineSegment(sketch, "E1227", {"start": v(-156.5, -172.8) * mm, "end": v(-156.77, -173.79) * mm});
            skLineSegment(sketch, "E1228", {"start": v(-156.77, -173.79) * mm, "end": v(-156.77, -174.12) * mm});
            skLineSegment(sketch, "E1229", {"start": v(-156.77, -174.12) * mm, "end": v(-156.77, -175.42) * mm});
            skLineSegment(sketch, "E1230", {"start": v(-156.77, -175.42) * mm, "end": v(-156.77, -175.75) * mm});
            skLineSegment(sketch, "E1231", {"start": v(-156.77, -175.75) * mm, "end": v(-156.5, -176.74) * mm});
            skLineSegment(sketch, "E1232", {"start": v(-156.5, -176.74) * mm, "end": v(-155.77, -177.82) * mm});
            skLineSegment(sketch, "E1233", {"start": v(-155.77, -177.82) * mm, "end": v(-154.69, -178.55) * mm});
            skLineSegment(sketch, "E1234", {"start": v(-154.69, -178.55) * mm, "end": v(-153.7, -178.82) * mm});
            skLineSegment(sketch, "E1235", {"start": v(-153.7, -178.82) * mm, "end": v(-153.36, -178.82) * mm});
            skLineSegment(sketch, "E1236", {"start": v(-153.36, -178.82) * mm, "end": v(-140.68, -178.82) * mm});
            skLineSegment(sketch, "E1237", {"start": v(-140.68, -178.82) * mm, "end": v(-140.68, -191.41) * mm});
            skLineSegment(sketch, "E1238", {"start": v(-140.68, -191.41) * mm, "end": v(-140.68, -191.74) * mm});
            skLineSegment(sketch, "E1239", {"start": v(-140.68, -191.74) * mm, "end": v(-140.42, -192.74) * mm});
            skLineSegment(sketch, "E1240", {"start": v(-140.42, -192.74) * mm, "end": v(-139.69, -193.82) * mm});
            skLineSegment(sketch, "E1241", {"start": v(-139.69, -193.82) * mm, "end": v(-138.61, -194.55) * mm});
            skLineSegment(sketch, "E1242", {"start": v(-138.61, -194.55) * mm, "end": v(-137.61, -194.82) * mm});
            skLineSegment(sketch, "E1243", {"start": v(-137.61, -194.82) * mm, "end": v(-137.29, -194.82) * mm});
            skLineSegment(sketch, "E1244", {"start": v(-137.29, -194.82) * mm, "end": v(-135.9, -194.82) * mm});
            skLineSegment(sketch, "E1245", {"start": v(-135.9, -194.82) * mm, "end": v(-135.56, -194.82) * mm});
            skLineSegment(sketch, "E1246", {"start": v(-135.56, -194.82) * mm, "end": v(-134.57, -194.55) * mm});
            skLineSegment(sketch, "E1247", {"start": v(-134.57, -194.55) * mm, "end": v(-133.49, -193.82) * mm});
            skLineSegment(sketch, "E1248", {"start": v(-133.49, -193.82) * mm, "end": v(-132.76, -192.74) * mm});
            skLineSegment(sketch, "E1249", {"start": v(-132.76, -192.74) * mm, "end": v(-132.5, -191.74) * mm});
            skLineSegment(sketch, "E1250", {"start": v(-132.5, -191.74) * mm, "end": v(-132.5, -191.41) * mm});
            skLineSegment(sketch, "E1251", {"start": v(-132.5, -191.41) * mm, "end": v(-132.5, -178.82) * mm});
            skLineSegment(sketch, "E1252", {"start": v(-132.5, -178.82) * mm, "end": v(-119.9, -178.82) * mm});
            skLineSegment(sketch, "E1253", {"start": v(-119.9, -178.82) * mm, "end": v(-119.57, -178.82) * mm});
            skLineSegment(sketch, "E1254", {"start": v(-119.57, -178.82) * mm, "end": v(-118.57, -178.55) * mm});
            skLineSegment(sketch, "E1255", {"start": v(-118.57, -178.55) * mm, "end": v(-117.5, -177.82) * mm});
            skLineSegment(sketch, "E1256", {"start": v(-117.5, -177.82) * mm, "end": v(-116.76, -176.74) * mm});
            skLineSegment(sketch, "E1257", {"start": v(-116.76, -176.74) * mm, "end": v(-116.5, -175.75) * mm});
            skLineSegment(sketch, "E1258", {"start": v(-116.5, -175.75) * mm, "end": v(-116.5, -175.42) * mm});
            skLineSegment(sketch, "E1259", {"start": v(-116.5, -175.42) * mm, "end": v(-116.5, -174.12) * mm});
            skLineSegment(sketch, "E1260", {"start": v(-116.5, -174.12) * mm, "end": v(-116.5, -173.79) * mm});
            skLineSegment(sketch, "E1261", {"start": v(-116.5, -173.79) * mm, "end": v(-116.76, -172.8) * mm});
            skLineSegment(sketch, "E1262", {"start": v(-116.76, -172.8) * mm, "end": v(-117.5, -171.71) * mm});
            skLineSegment(sketch, "E1263", {"start": v(-117.5, -171.71) * mm, "end": v(-118.57, -170.98) * mm});
            skLineSegment(sketch, "E1264", {"start": v(-118.57, -170.98) * mm, "end": v(-119.57, -170.71) * mm});
            skLineSegment(sketch, "E1265", {"start": v(-119.57, -170.71) * mm, "end": v(-119.9, -170.71) * mm});
            skLineSegment(sketch, "E1266", {"start": v(-71.45, -150.31) * mm, "end": v(-55.47, -150.31) * mm});
            skLineSegment(sketch, "E1267", {"start": v(-55.47, -150.31) * mm, "end": v(-54.8, -150.31) * mm});
            skLineSegment(sketch, "E1268", {"start": v(-54.8, -150.31) * mm, "end": v(-52.81, -150.56) * mm});
            skLineSegment(sketch, "E1269", {"start": v(-52.81, -150.56) * mm, "end": v(-50.34, -151.28) * mm});
            skLineSegment(sketch, "E1270", {"start": v(-50.34, -151.28) * mm, "end": v(-48.1, -152.42) * mm});
            skLineSegment(sketch, "E1271", {"start": v(-48.1, -152.42) * mm, "end": v(-46.14, -153.93) * mm});
            skLineSegment(sketch, "E1272", {"start": v(-46.14, -153.93) * mm, "end": v(-44.53, -155.75) * mm});
            skLineSegment(sketch, "E1273", {"start": v(-44.53, -155.75) * mm, "end": v(-43.3, -157.85) * mm});
            skLineSegment(sketch, "E1274", {"start": v(-43.3, -157.85) * mm, "end": v(-42.54, -160.16) * mm});
            skLineSegment(sketch, "E1275", {"start": v(-42.54, -160.16) * mm, "end": v(-42.27, -162.02) * mm});
            skLineSegment(sketch, "E1276", {"start": v(-42.27, -162.02) * mm, "end": v(-42.27, -162.64) * mm});
            skLineSegment(sketch, "E1277", {"start": v(-42.27, -162.64) * mm, "end": v(-42.27, -163.3) * mm});
            skLineSegment(sketch, "E1278", {"start": v(-42.27, -163.3) * mm, "end": v(-42.53, -165.26) * mm});
            skLineSegment(sketch, "E1279", {"start": v(-42.53, -165.26) * mm, "end": v(-43.28, -167.7) * mm});
            skLineSegment(sketch, "E1280", {"start": v(-43.28, -167.7) * mm, "end": v(-44.48, -169.88) * mm});
            skLineSegment(sketch, "E1281", {"start": v(-44.48, -169.88) * mm, "end": v(-46.07, -171.77) * mm});
            skLineSegment(sketch, "E1282", {"start": v(-46.07, -171.77) * mm, "end": v(-48, -173.33) * mm});
            skLineSegment(sketch, "E1283", {"start": v(-48, -173.33) * mm, "end": v(-50.23, -174.5) * mm});
            skLineSegment(sketch, "E1284", {"start": v(-50.23, -174.5) * mm, "end": v(-52.7, -175.24) * mm});
            skLineSegment(sketch, "E1285", {"start": v(-52.7, -175.24) * mm, "end": v(-54.71, -175.5) * mm});
            skLineSegment(sketch, "E1286", {"start": v(-54.71, -175.5) * mm, "end": v(-55.38, -175.5) * mm});
            skLineSegment(sketch, "E1287", {"start": v(-55.38, -175.5) * mm, "end": v(-71.45, -175.5) * mm});
            skLineSegment(sketch, "E1288", {"start": v(-71.45, -175.5) * mm, "end": v(-71.45, -150.31) * mm});
            skLineSegment(sketch, "E1289", {"start": v(-33.55, -162.64) * mm, "end": v(-33.55, -161.58) * mm});
            skLineSegment(sketch, "E1290", {"start": v(-33.55, -161.58) * mm, "end": v(-33.98, -158.39) * mm});
            skLineSegment(sketch, "E1291", {"start": v(-33.98, -158.39) * mm, "end": v(-35.23, -154.44) * mm});
            skLineSegment(sketch, "E1292", {"start": v(-35.23, -154.44) * mm, "end": v(-37.2, -150.9) * mm});
            skLineSegment(sketch, "E1293", {"start": v(-37.2, -150.9) * mm, "end": v(-39.82, -147.82) * mm});
            skLineSegment(sketch, "E1294", {"start": v(-39.82, -147.82) * mm, "end": v(-43.02, -145.29) * mm});
            skLineSegment(sketch, "E1295", {"start": v(-43.02, -145.29) * mm, "end": v(-46.7, -143.39) * mm});
            skLineSegment(sketch, "E1296", {"start": v(-46.7, -143.39) * mm, "end": v(-50.8, -142.19) * mm});
            skLineSegment(sketch, "E1297", {"start": v(-50.8, -142.19) * mm, "end": v(-54.1, -141.77) * mm});
            skLineSegment(sketch, "E1298", {"start": v(-54.1, -141.77) * mm, "end": v(-55.2, -141.77) * mm});
            skLineSegment(sketch, "E1299", {"start": v(-55.2, -141.77) * mm, "end": v(-76.77, -141.77) * mm});
            skLineSegment(sketch, "E1300", {"start": v(-76.77, -141.77) * mm, "end": v(-77.1, -141.77) * mm});
            skLineSegment(sketch, "E1301", {"start": v(-77.1, -141.77) * mm, "end": v(-78.1, -142.03) * mm});
            skLineSegment(sketch, "E1302", {"start": v(-78.1, -142.03) * mm, "end": v(-79.18, -142.76) * mm});
            skLineSegment(sketch, "E1303", {"start": v(-79.18, -142.76) * mm, "end": v(-79.9, -143.83) * mm});
            skLineSegment(sketch, "E1304", {"start": v(-79.9, -143.83) * mm, "end": v(-80.17, -144.84) * mm});
            skLineSegment(sketch, "E1305", {"start": v(-80.17, -144.84) * mm, "end": v(-80.17, -145.17) * mm});
            skLineSegment(sketch, "E1306", {"start": v(-80.17, -145.17) * mm, "end": v(-80.17, -203.76) * mm});
            skLineSegment(sketch, "E1307", {"start": v(-80.17, -203.76) * mm, "end": v(-80.17, -204.09) * mm});
            skLineSegment(sketch, "E1308", {"start": v(-80.17, -204.09) * mm, "end": v(-79.9, -205.08) * mm});
            skLineSegment(sketch, "E1309", {"start": v(-79.9, -205.08) * mm, "end": v(-79.17, -206.16) * mm});
            skLineSegment(sketch, "E1310", {"start": v(-79.17, -206.16) * mm, "end": v(-78.09, -206.89) * mm});
            skLineSegment(sketch, "E1311", {"start": v(-78.09, -206.89) * mm, "end": v(-77.1, -207.16) * mm});
            skLineSegment(sketch, "E1312", {"start": v(-77.1, -207.16) * mm, "end": v(-76.77, -207.16) * mm});
            skLineSegment(sketch, "E1313", {"start": v(-76.77, -207.16) * mm, "end": v(-75.2, -207.16) * mm});
            skLineSegment(sketch, "E1314", {"start": v(-75.2, -207.16) * mm, "end": v(-74.84, -207.16) * mm});
            skLineSegment(sketch, "E1315", {"start": v(-74.84, -207.16) * mm, "end": v(-73.76, -206.9) * mm});
            skLineSegment(sketch, "E1316", {"start": v(-73.76, -206.9) * mm, "end": v(-72.6, -206.17) * mm});
            skLineSegment(sketch, "E1317", {"start": v(-72.6, -206.17) * mm, "end": v(-71.82, -205.1) * mm});
            skLineSegment(sketch, "E1318", {"start": v(-71.82, -205.1) * mm, "end": v(-71.54, -204.09) * mm});
            skLineSegment(sketch, "E1319", {"start": v(-71.54, -204.09) * mm, "end": v(-71.54, -203.76) * mm});
            skLineSegment(sketch, "E1320", {"start": v(-71.54, -203.76) * mm, "end": v(-71.54, -183.7) * mm});
            skLineSegment(sketch, "E1321", {"start": v(-71.54, -183.7) * mm, "end": v(-57.82, -183.7) * mm});
            skLineSegment(sketch, "E1322", {"start": v(-57.82, -183.7) * mm, "end": v(-57.34, -183.7) * mm});
            skLineSegment(sketch, "E1323", {"start": v(-57.34, -183.7) * mm, "end": v(-56.06, -183.68) * mm});
            skLineSegment(sketch, "E1324", {"start": v(-56.06, -183.68) * mm, "end": v(-55.9, -183.67) * mm});
            skLineSegment(sketch, "E1325", {"start": v(-55.9, -183.67) * mm, "end": v(-44, -205.17) * mm});
            skLineSegment(sketch, "E1326", {"start": v(-44, -205.17) * mm, "end": v(-43.89, -205.4) * mm});
            skLineSegment(sketch, "E1327", {"start": v(-43.89, -205.4) * mm, "end": v(-43.42, -206.02) * mm});
            skLineSegment(sketch, "E1328", {"start": v(-43.42, -206.02) * mm, "end": v(-42.68, -206.64) * mm});
            skLineSegment(sketch, "E1329", {"start": v(-42.68, -206.64) * mm, "end": v(-41.8, -207.03) * mm});
            skLineSegment(sketch, "E1330", {"start": v(-41.8, -207.03) * mm, "end": v(-41.03, -207.16) * mm});
            skLineSegment(sketch, "E1331", {"start": v(-41.03, -207.16) * mm, "end": v(-40.78, -207.16) * mm});
            skLineSegment(sketch, "E1332", {"start": v(-40.78, -207.16) * mm, "end": v(-38.08, -207.16) * mm});
            skLineSegment(sketch, "E1333", {"start": v(-38.08, -207.16) * mm, "end": v(-37.87, -207.16) * mm});
            skLineSegment(sketch, "E1334", {"start": v(-37.87, -207.16) * mm, "end": v(-37.25, -207.05) * mm});
            skLineSegment(sketch, "E1335", {"start": v(-37.25, -207.05) * mm, "end": v(-36.49, -206.75) * mm});
            skLineSegment(sketch, "E1336", {"start": v(-36.49, -206.75) * mm, "end": v(-35.85, -206.26) * mm});
            skLineSegment(sketch, "E1337", {"start": v(-35.85, -206.26) * mm, "end": v(-35.46, -205.79) * mm});
            skLineSegment(sketch, "E1338", {"start": v(-35.46, -205.79) * mm, "end": v(-35.36, -205.61) * mm});
            skLineSegment(sketch, "E1339", {"start": v(-35.36, -205.61) * mm, "end": v(-35.22, -205.35) * mm});
            skLineSegment(sketch, "E1340", {"start": v(-35.22, -205.35) * mm, "end": v(-34.98, -203.92) * mm});
            skLineSegment(sketch, "E1341", {"start": v(-34.98, -203.92) * mm, "end": v(-35.35, -202.44) * mm});
            skLineSegment(sketch, "E1342", {"start": v(-35.35, -202.44) * mm, "end": v(-35.51, -202.17) * mm});
            skLineSegment(sketch, "E1343", {"start": v(-35.51, -202.17) * mm, "end": v(-46.86, -182.06) * mm});
            skLineSegment(sketch, "E1344", {"start": v(-46.86, -182.06) * mm, "end": v(-46.11, -181.74) * mm});
            skLineSegment(sketch, "E1345", {"start": v(-46.11, -181.74) * mm, "end": v(-43.97, -180.6) * mm});
            skLineSegment(sketch, "E1346", {"start": v(-43.97, -180.6) * mm, "end": v(-41.38, -178.8) * mm});
            skLineSegment(sketch, "E1347", {"start": v(-41.38, -178.8) * mm, "end": v(-39.1, -176.68) * mm});
            skLineSegment(sketch, "E1348", {"start": v(-39.1, -176.68) * mm, "end": v(-37.18, -174.28) * mm});
            skLineSegment(sketch, "E1349", {"start": v(-37.18, -174.28) * mm, "end": v(-35.64, -171.65) * mm});
            skLineSegment(sketch, "E1350", {"start": v(-35.64, -171.65) * mm, "end": v(-34.5, -168.8) * mm});
            skLineSegment(sketch, "E1351", {"start": v(-34.5, -168.8) * mm, "end": v(-33.8, -165.79) * mm});
            skLineSegment(sketch, "E1352", {"start": v(-33.8, -165.79) * mm, "end": v(-33.55, -163.43) * mm});
            skLineSegment(sketch, "E1353", {"start": v(-33.55, -163.43) * mm, "end": v(-33.55, -162.64) * mm});
            skLineSegment(sketch, "E1354", {"start": v(32, -141.77) * mm, "end": v(-2.86, -141.77) * mm});
            skLineSegment(sketch, "E1355", {"start": v(-2.86, -141.77) * mm, "end": v(-3.2, -141.77) * mm});
            skLineSegment(sketch, "E1356", {"start": v(-3.2, -141.77) * mm, "end": v(-4.18, -142.04) * mm});
            skLineSegment(sketch, "E1357", {"start": v(-4.18, -142.04) * mm, "end": v(-5.26, -142.77) * mm});
            skLineSegment(sketch, "E1358", {"start": v(-5.26, -142.77) * mm, "end": v(-6, -143.85) * mm});
            skLineSegment(sketch, "E1359", {"start": v(-6, -143.85) * mm, "end": v(-6.26, -144.84) * mm});
            skLineSegment(sketch, "E1360", {"start": v(-6.26, -144.84) * mm, "end": v(-6.26, -145.17) * mm});
            skLineSegment(sketch, "E1361", {"start": v(-6.26, -145.17) * mm, "end": v(-6.26, -203.76) * mm});
            skLineSegment(sketch, "E1362", {"start": v(-6.26, -203.76) * mm, "end": v(-6.26, -204.09) * mm});
            skLineSegment(sketch, "E1363", {"start": v(-6.26, -204.09) * mm, "end": v(-6, -205.08) * mm});
            skLineSegment(sketch, "E1364", {"start": v(-6, -205.08) * mm, "end": v(-5.26, -206.16) * mm});
            skLineSegment(sketch, "E1365", {"start": v(-5.26, -206.16) * mm, "end": v(-4.18, -206.89) * mm});
            skLineSegment(sketch, "E1366", {"start": v(-4.18, -206.89) * mm, "end": v(-3.2, -207.16) * mm});
            skLineSegment(sketch, "E1367", {"start": v(-3.2, -207.16) * mm, "end": v(-2.86, -207.16) * mm});
            skLineSegment(sketch, "E1368", {"start": v(-2.86, -207.16) * mm, "end": v(32, -207.16) * mm});
            skLineSegment(sketch, "E1369", {"start": v(32, -207.16) * mm, "end": v(32.33, -207.16) * mm});
            skLineSegment(sketch, "E1370", {"start": v(32.33, -207.16) * mm, "end": v(33.32, -206.89) * mm});
            skLineSegment(sketch, "E1371", {"start": v(33.32, -206.89) * mm, "end": v(34.4, -206.16) * mm});
            skLineSegment(sketch, "E1372", {"start": v(34.4, -206.16) * mm, "end": v(35.13, -205.08) * mm});
            skLineSegment(sketch, "E1373", {"start": v(35.13, -205.08) * mm, "end": v(35.4, -204.09) * mm});
            skLineSegment(sketch, "E1374", {"start": v(35.4, -204.09) * mm, "end": v(35.4, -203.76) * mm});
            skLineSegment(sketch, "E1375", {"start": v(35.4, -203.76) * mm, "end": v(35.4, -202.36) * mm});
            skLineSegment(sketch, "E1376", {"start": v(35.4, -202.36) * mm, "end": v(35.4, -202.03) * mm});
            skLineSegment(sketch, "E1377", {"start": v(35.4, -202.03) * mm, "end": v(35.13, -201.04) * mm});
            skLineSegment(sketch, "E1378", {"start": v(35.13, -201.04) * mm, "end": v(34.4, -199.96) * mm});
            skLineSegment(sketch, "E1379", {"start": v(34.4, -199.96) * mm, "end": v(33.32, -199.23) * mm});
            skLineSegment(sketch, "E1380", {"start": v(33.32, -199.23) * mm, "end": v(32.33, -198.96) * mm});
            skLineSegment(sketch, "E1381", {"start": v(32.33, -198.96) * mm, "end": v(32, -198.96) * mm});
            skLineSegment(sketch, "E1382", {"start": v(32, -198.96) * mm, "end": v(2.45, -198.96) * mm});
            skLineSegment(sketch, "E1383", {"start": v(2.45, -198.96) * mm, "end": v(2.45, -177.78) * mm});
            skLineSegment(sketch, "E1384", {"start": v(2.45, -177.78) * mm, "end": v(27.74, -177.78) * mm});
            skLineSegment(sketch, "E1385", {"start": v(27.74, -177.78) * mm, "end": v(28.07, -177.78) * mm});
            skLineSegment(sketch, "E1386", {"start": v(28.07, -177.78) * mm, "end": v(29.06, -177.5) * mm});
            skLineSegment(sketch, "E1387", {"start": v(29.06, -177.5) * mm, "end": v(30.14, -176.78) * mm});
            skLineSegment(sketch, "E1388", {"start": v(30.14, -176.78) * mm, "end": v(30.87, -175.7) * mm});
            skLineSegment(sketch, "E1389", {"start": v(30.87, -175.7) * mm, "end": v(31.14, -174.7) * mm});
            skLineSegment(sketch, "E1390", {"start": v(31.14, -174.7) * mm, "end": v(31.14, -174.38) * mm});
            skLineSegment(sketch, "E1391", {"start": v(31.14, -174.38) * mm, "end": v(31.14, -172.9) * mm});
            skLineSegment(sketch, "E1392", {"start": v(31.14, -172.9) * mm, "end": v(31.14, -172.57) * mm});
            skLineSegment(sketch, "E1393", {"start": v(31.14, -172.57) * mm, "end": v(30.87, -171.57) * mm});
            skLineSegment(sketch, "E1394", {"start": v(30.87, -171.57) * mm, "end": v(30.14, -170.5) * mm});
            skLineSegment(sketch, "E1395", {"start": v(30.14, -170.5) * mm, "end": v(29.06, -169.77) * mm});
            skLineSegment(sketch, "E1396", {"start": v(29.06, -169.77) * mm, "end": v(28.07, -169.5) * mm});
            skLineSegment(sketch, "E1397", {"start": v(28.07, -169.5) * mm, "end": v(27.74, -169.5) * mm});
            skLineSegment(sketch, "E1398", {"start": v(27.74, -169.5) * mm, "end": v(2.45, -169.5) * mm});
            skLineSegment(sketch, "E1399", {"start": v(2.45, -169.5) * mm, "end": v(2.45, -150.05) * mm});
            skLineSegment(sketch, "E1400", {"start": v(2.45, -150.05) * mm, "end": v(32, -150.05) * mm});
            skLineSegment(sketch, "E1401", {"start": v(32, -150.05) * mm, "end": v(32.33, -150.05) * mm});
            skLineSegment(sketch, "E1402", {"start": v(32.33, -150.05) * mm, "end": v(33.32, -149.78) * mm});
            skLineSegment(sketch, "E1403", {"start": v(33.32, -149.78) * mm, "end": v(34.4, -149.05) * mm});
            skLineSegment(sketch, "E1404", {"start": v(34.4, -149.05) * mm, "end": v(35.13, -147.97) * mm});
            skLineSegment(sketch, "E1405", {"start": v(35.13, -147.97) * mm, "end": v(35.4, -146.98) * mm});
            skLineSegment(sketch, "E1406", {"start": v(35.4, -146.98) * mm, "end": v(35.4, -146.65) * mm});
            skLineSegment(sketch, "E1407", {"start": v(35.4, -146.65) * mm, "end": v(35.4, -145.17) * mm});
            skLineSegment(sketch, "E1408", {"start": v(35.4, -145.17) * mm, "end": v(35.4, -144.84) * mm});
            skLineSegment(sketch, "E1409", {"start": v(35.4, -144.84) * mm, "end": v(35.13, -143.85) * mm});
            skLineSegment(sketch, "E1410", {"start": v(35.13, -143.85) * mm, "end": v(34.4, -142.77) * mm});
            skLineSegment(sketch, "E1411", {"start": v(34.4, -142.77) * mm, "end": v(33.32, -142.04) * mm});
            skLineSegment(sketch, "E1412", {"start": v(33.32, -142.04) * mm, "end": v(32.33, -141.77) * mm});
            skLineSegment(sketch, "E1413", {"start": v(32.33, -141.77) * mm, "end": v(32, -141.77) * mm});
            skLineSegment(sketch, "E1414", {"start": v(95.38, -141.77) * mm, "end": v(58, -141.77) * mm});
            skLineSegment(sketch, "E1415", {"start": v(58, -141.77) * mm, "end": v(57.67, -141.77) * mm});
            skLineSegment(sketch, "E1416", {"start": v(57.67, -141.77) * mm, "end": v(56.67, -142.03) * mm});
            skLineSegment(sketch, "E1417", {"start": v(56.67, -142.03) * mm, "end": v(55.59, -142.76) * mm});
            skLineSegment(sketch, "E1418", {"start": v(55.59, -142.76) * mm, "end": v(54.86, -143.83) * mm});
            skLineSegment(sketch, "E1419", {"start": v(54.86, -143.83) * mm, "end": v(54.6, -144.84) * mm});
            skLineSegment(sketch, "E1420", {"start": v(54.6, -144.84) * mm, "end": v(54.6, -145.17) * mm});
            skLineSegment(sketch, "E1421", {"start": v(54.6, -145.17) * mm, "end": v(54.6, -146.48) * mm});
            skLineSegment(sketch, "E1422", {"start": v(54.6, -146.48) * mm, "end": v(54.6, -146.88) * mm});
            skLineSegment(sketch, "E1423", {"start": v(54.6, -146.88) * mm, "end": v(54.9, -148.08) * mm});
            skLineSegment(sketch, "E1424", {"start": v(54.9, -148.08) * mm, "end": v(55.67, -149.19) * mm});
            skLineSegment(sketch, "E1425", {"start": v(55.67, -149.19) * mm, "end": v(56.76, -149.84) * mm});
            skLineSegment(sketch, "E1426", {"start": v(56.76, -149.84) * mm, "end": v(57.7, -150.05) * mm});
            skLineSegment(sketch, "E1427", {"start": v(57.7, -150.05) * mm, "end": v(58, -150.05) * mm});
            skLineSegment(sketch, "E1428", {"start": v(58, -150.05) * mm, "end": v(72.34, -150.05) * mm});
            skLineSegment(sketch, "E1429", {"start": v(72.34, -150.05) * mm, "end": v(72.34, -203.76) * mm});
            skLineSegment(sketch, "E1430", {"start": v(72.34, -203.76) * mm, "end": v(72.34, -204.09) * mm});
            skLineSegment(sketch, "E1431", {"start": v(72.34, -204.09) * mm, "end": v(72.6, -205.08) * mm});
            skLineSegment(sketch, "E1432", {"start": v(72.6, -205.08) * mm, "end": v(73.34, -206.16) * mm});
            skLineSegment(sketch, "E1433", {"start": v(73.34, -206.16) * mm, "end": v(74.42, -206.89) * mm});
            skLineSegment(sketch, "E1434", {"start": v(74.42, -206.89) * mm, "end": v(75.4, -207.16) * mm});
            skLineSegment(sketch, "E1435", {"start": v(75.4, -207.16) * mm, "end": v(75.74, -207.16) * mm});
            skLineSegment(sketch, "E1436", {"start": v(75.74, -207.16) * mm, "end": v(77.3, -207.16) * mm});
            skLineSegment(sketch, "E1437", {"start": v(77.3, -207.16) * mm, "end": v(77.66, -207.16) * mm});
            skLineSegment(sketch, "E1438", {"start": v(77.66, -207.16) * mm, "end": v(78.74, -206.9) * mm});
            skLineSegment(sketch, "E1439", {"start": v(78.74, -206.9) * mm, "end": v(79.9, -206.17) * mm});
            skLineSegment(sketch, "E1440", {"start": v(79.9, -206.17) * mm, "end": v(80.69, -205.1) * mm});
            skLineSegment(sketch, "E1441", {"start": v(80.69, -205.1) * mm, "end": v(80.97, -204.09) * mm});
            skLineSegment(sketch, "E1442", {"start": v(80.97, -204.09) * mm, "end": v(80.97, -203.76) * mm});
            skLineSegment(sketch, "E1443", {"start": v(80.97, -203.76) * mm, "end": v(80.97, -150.05) * mm});
            skLineSegment(sketch, "E1444", {"start": v(80.97, -150.05) * mm, "end": v(95.38, -150.05) * mm});
            skLineSegment(sketch, "E1445", {"start": v(95.38, -150.05) * mm, "end": v(95.72, -150.05) * mm});
            skLineSegment(sketch, "E1446", {"start": v(95.72, -150.05) * mm, "end": v(96.72, -149.79) * mm});
            skLineSegment(sketch, "E1447", {"start": v(96.72, -149.79) * mm, "end": v(97.8, -149.07) * mm});
            skLineSegment(sketch, "E1448", {"start": v(97.8, -149.07) * mm, "end": v(98.52, -147.99) * mm});
            skLineSegment(sketch, "E1449", {"start": v(98.52, -147.99) * mm, "end": v(98.79, -146.98) * mm});
            skLineSegment(sketch, "E1450", {"start": v(98.79, -146.98) * mm, "end": v(98.79, -146.65) * mm});
            skLineSegment(sketch, "E1451", {"start": v(98.79, -146.65) * mm, "end": v(98.79, -145.17) * mm});
            skLineSegment(sketch, "E1452", {"start": v(98.79, -145.17) * mm, "end": v(98.79, -144.84) * mm});
            skLineSegment(sketch, "E1453", {"start": v(98.79, -144.84) * mm, "end": v(98.52, -143.83) * mm});
            skLineSegment(sketch, "E1454", {"start": v(98.52, -143.83) * mm, "end": v(97.8, -142.76) * mm});
            skLineSegment(sketch, "E1455", {"start": v(97.8, -142.76) * mm, "end": v(96.72, -142.03) * mm});
            skLineSegment(sketch, "E1456", {"start": v(96.72, -142.03) * mm, "end": v(95.72, -141.77) * mm});
            skLineSegment(sketch, "E1457", {"start": v(95.72, -141.77) * mm, "end": v(95.38, -141.77) * mm});
            skLineSegment(sketch, "E1458", {"start": v(130.27, -150.31) * mm, "end": v(146.25, -150.31) * mm});
            skLineSegment(sketch, "E1459", {"start": v(146.25, -150.31) * mm, "end": v(146.91, -150.31) * mm});
            skLineSegment(sketch, "E1460", {"start": v(146.91, -150.31) * mm, "end": v(148.9, -150.56) * mm});
            skLineSegment(sketch, "E1461", {"start": v(148.9, -150.56) * mm, "end": v(151.38, -151.28) * mm});
            skLineSegment(sketch, "E1462", {"start": v(151.38, -151.28) * mm, "end": v(153.62, -152.42) * mm});
            skLineSegment(sketch, "E1463", {"start": v(153.62, -152.42) * mm, "end": v(155.58, -153.93) * mm});
            skLineSegment(sketch, "E1464", {"start": v(155.58, -153.93) * mm, "end": v(157.19, -155.75) * mm});
            skLineSegment(sketch, "E1465", {"start": v(157.19, -155.75) * mm, "end": v(158.4, -157.85) * mm});
            skLineSegment(sketch, "E1466", {"start": v(158.4, -157.85) * mm, "end": v(159.18, -160.16) * mm});
            skLineSegment(sketch, "E1467", {"start": v(159.18, -160.16) * mm, "end": v(159.45, -162.02) * mm});
            skLineSegment(sketch, "E1468", {"start": v(159.45, -162.02) * mm, "end": v(159.45, -162.64) * mm});
            skLineSegment(sketch, "E1469", {"start": v(159.45, -162.64) * mm, "end": v(159.45, -163.3) * mm});
            skLineSegment(sketch, "E1470", {"start": v(159.45, -163.3) * mm, "end": v(159.18, -165.26) * mm});
            skLineSegment(sketch, "E1471", {"start": v(159.18, -165.26) * mm, "end": v(158.43, -167.7) * mm});
            skLineSegment(sketch, "E1472", {"start": v(158.43, -167.7) * mm, "end": v(157.24, -169.88) * mm});
            skLineSegment(sketch, "E1473", {"start": v(157.24, -169.88) * mm, "end": v(155.65, -171.77) * mm});
            skLineSegment(sketch, "E1474", {"start": v(155.65, -171.77) * mm, "end": v(153.71, -173.33) * mm});
            skLineSegment(sketch, "E1475", {"start": v(153.71, -173.33) * mm, "end": v(151.49, -174.5) * mm});
            skLineSegment(sketch, "E1476", {"start": v(151.49, -174.5) * mm, "end": v(149, -175.24) * mm});
            skLineSegment(sketch, "E1477", {"start": v(149, -175.24) * mm, "end": v(147, -175.5) * mm});
            skLineSegment(sketch, "E1478", {"start": v(147, -175.5) * mm, "end": v(146.34, -175.5) * mm});
            skLineSegment(sketch, "E1479", {"start": v(146.34, -175.5) * mm, "end": v(130.27, -175.5) * mm});
            skLineSegment(sketch, "E1480", {"start": v(130.27, -175.5) * mm, "end": v(130.27, -150.31) * mm});
            skLineSegment(sketch, "E1481", {"start": v(168.17, -162.64) * mm, "end": v(168.17, -161.58) * mm});
            skLineSegment(sketch, "E1482", {"start": v(168.17, -161.58) * mm, "end": v(167.73, -158.39) * mm});
            skLineSegment(sketch, "E1483", {"start": v(167.73, -158.39) * mm, "end": v(166.49, -154.44) * mm});
            skLineSegment(sketch, "E1484", {"start": v(166.49, -154.44) * mm, "end": v(164.52, -150.9) * mm});
            skLineSegment(sketch, "E1485", {"start": v(164.52, -150.9) * mm, "end": v(161.89, -147.82) * mm});
            skLineSegment(sketch, "E1486", {"start": v(161.89, -147.82) * mm, "end": v(158.7, -145.29) * mm});
            skLineSegment(sketch, "E1487", {"start": v(158.7, -145.29) * mm, "end": v(155.02, -143.39) * mm});
            skLineSegment(sketch, "E1488", {"start": v(155.02, -143.39) * mm, "end": v(150.92, -142.19) * mm});
            skLineSegment(sketch, "E1489", {"start": v(150.92, -142.19) * mm, "end": v(147.6, -141.77) * mm});
            skLineSegment(sketch, "E1490", {"start": v(147.6, -141.77) * mm, "end": v(146.5, -141.77) * mm});
            skLineSegment(sketch, "E1491", {"start": v(146.5, -141.77) * mm, "end": v(124.95, -141.77) * mm});
            skLineSegment(sketch, "E1492", {"start": v(124.95, -141.77) * mm, "end": v(124.62, -141.77) * mm});
            skLineSegment(sketch, "E1493", {"start": v(124.62, -141.77) * mm, "end": v(123.61, -142.03) * mm});
            skLineSegment(sketch, "E1494", {"start": v(123.61, -142.03) * mm, "end": v(122.53, -142.76) * mm});
            skLineSegment(sketch, "E1495", {"start": v(122.53, -142.76) * mm, "end": v(121.81, -143.83) * mm});
            skLineSegment(sketch, "E1496", {"start": v(121.81, -143.83) * mm, "end": v(121.55, -144.84) * mm});
            skLineSegment(sketch, "E1497", {"start": v(121.55, -144.84) * mm, "end": v(121.55, -145.17) * mm});
            skLineSegment(sketch, "E1498", {"start": v(121.55, -145.17) * mm, "end": v(121.55, -203.76) * mm});
            skLineSegment(sketch, "E1499", {"start": v(121.55, -203.76) * mm, "end": v(121.55, -204.09) * mm});
            skLineSegment(sketch, "E1500", {"start": v(121.55, -204.09) * mm, "end": v(121.82, -205.08) * mm});
            skLineSegment(sketch, "E1501", {"start": v(121.82, -205.08) * mm, "end": v(122.55, -206.16) * mm});
            skLineSegment(sketch, "E1502", {"start": v(122.55, -206.16) * mm, "end": v(123.62, -206.89) * mm});
            skLineSegment(sketch, "E1503", {"start": v(123.62, -206.89) * mm, "end": v(124.62, -207.16) * mm});
            skLineSegment(sketch, "E1504", {"start": v(124.62, -207.16) * mm, "end": v(124.95, -207.16) * mm});
            skLineSegment(sketch, "E1505", {"start": v(124.95, -207.16) * mm, "end": v(126.52, -207.16) * mm});
            skLineSegment(sketch, "E1506", {"start": v(126.52, -207.16) * mm, "end": v(126.87, -207.16) * mm});
            skLineSegment(sketch, "E1507", {"start": v(126.87, -207.16) * mm, "end": v(127.95, -206.9) * mm});
            skLineSegment(sketch, "E1508", {"start": v(127.95, -206.9) * mm, "end": v(129.12, -206.17) * mm});
            skLineSegment(sketch, "E1509", {"start": v(129.12, -206.17) * mm, "end": v(129.9, -205.1) * mm});
            skLineSegment(sketch, "E1510", {"start": v(129.9, -205.1) * mm, "end": v(130.18, -204.09) * mm});
            skLineSegment(sketch, "E1511", {"start": v(130.18, -204.09) * mm, "end": v(130.18, -203.76) * mm});
            skLineSegment(sketch, "E1512", {"start": v(130.18, -203.76) * mm, "end": v(130.18, -183.7) * mm});
            skLineSegment(sketch, "E1513", {"start": v(130.18, -183.7) * mm, "end": v(143.9, -183.7) * mm});
            skLineSegment(sketch, "E1514", {"start": v(143.9, -183.7) * mm, "end": v(144.38, -183.7) * mm});
            skLineSegment(sketch, "E1515", {"start": v(144.38, -183.7) * mm, "end": v(145.66, -183.68) * mm});
            skLineSegment(sketch, "E1516", {"start": v(145.66, -183.68) * mm, "end": v(145.82, -183.67) * mm});
            skLineSegment(sketch, "E1517", {"start": v(145.82, -183.67) * mm, "end": v(157.71, -205.17) * mm});
            skLineSegment(sketch, "E1518", {"start": v(157.71, -205.17) * mm, "end": v(157.83, -205.4) * mm});
            skLineSegment(sketch, "E1519", {"start": v(157.83, -205.4) * mm, "end": v(158.3, -206.02) * mm});
            skLineSegment(sketch, "E1520", {"start": v(158.3, -206.02) * mm, "end": v(159.04, -206.64) * mm});
            skLineSegment(sketch, "E1521", {"start": v(159.04, -206.64) * mm, "end": v(159.93, -207.03) * mm});
            skLineSegment(sketch, "E1522", {"start": v(159.93, -207.03) * mm, "end": v(160.68, -207.16) * mm});
            skLineSegment(sketch, "E1523", {"start": v(160.68, -207.16) * mm, "end": v(160.94, -207.16) * mm});
            skLineSegment(sketch, "E1524", {"start": v(160.94, -207.16) * mm, "end": v(163.63, -207.16) * mm});
            skLineSegment(sketch, "E1525", {"start": v(163.63, -207.16) * mm, "end": v(163.84, -207.16) * mm});
            skLineSegment(sketch, "E1526", {"start": v(163.84, -207.16) * mm, "end": v(164.47, -207.05) * mm});
            skLineSegment(sketch, "E1527", {"start": v(164.47, -207.05) * mm, "end": v(165.22, -206.75) * mm});
            skLineSegment(sketch, "E1528", {"start": v(165.22, -206.75) * mm, "end": v(165.86, -206.26) * mm});
            skLineSegment(sketch, "E1529", {"start": v(165.86, -206.26) * mm, "end": v(166.26, -205.78) * mm});
            skLineSegment(sketch, "E1530", {"start": v(166.26, -205.78) * mm, "end": v(166.35, -205.6) * mm});
            skLineSegment(sketch, "E1531", {"start": v(166.35, -205.6) * mm, "end": v(166.5, -205.35) * mm});
            skLineSegment(sketch, "E1532", {"start": v(166.5, -205.35) * mm, "end": v(166.74, -203.92) * mm});
            skLineSegment(sketch, "E1533", {"start": v(166.74, -203.92) * mm, "end": v(166.37, -202.44) * mm});
            skLineSegment(sketch, "E1534", {"start": v(166.37, -202.44) * mm, "end": v(166.2, -202.17) * mm});
            skLineSegment(sketch, "E1535", {"start": v(166.2, -202.17) * mm, "end": v(154.86, -182.06) * mm});
            skLineSegment(sketch, "E1536", {"start": v(154.86, -182.06) * mm, "end": v(155.6, -181.74) * mm});
            skLineSegment(sketch, "E1537", {"start": v(155.6, -181.74) * mm, "end": v(157.75, -180.6) * mm});
            skLineSegment(sketch, "E1538", {"start": v(157.75, -180.6) * mm, "end": v(160.34, -178.8) * mm});
            skLineSegment(sketch, "E1539", {"start": v(160.34, -178.8) * mm, "end": v(162.61, -176.68) * mm});
            skLineSegment(sketch, "E1540", {"start": v(162.61, -176.68) * mm, "end": v(164.54, -174.28) * mm});
            skLineSegment(sketch, "E1541", {"start": v(164.54, -174.28) * mm, "end": v(166.08, -171.65) * mm});
            skLineSegment(sketch, "E1542", {"start": v(166.08, -171.65) * mm, "end": v(167.22, -168.8) * mm});
            skLineSegment(sketch, "E1543", {"start": v(167.22, -168.8) * mm, "end": v(167.92, -165.79) * mm});
            skLineSegment(sketch, "E1544", {"start": v(167.92, -165.79) * mm, "end": v(168.17, -163.43) * mm});
            skLineSegment(sketch, "E1545", {"start": v(168.17, -163.43) * mm, "end": v(168.17, -162.64) * mm});
            skLineSegment(sketch, "E1546", {"start": v(233.72, -141.77) * mm, "end": v(198.86, -141.77) * mm});
            skLineSegment(sketch, "E1547", {"start": v(198.86, -141.77) * mm, "end": v(198.53, -141.77) * mm});
            skLineSegment(sketch, "E1548", {"start": v(198.53, -141.77) * mm, "end": v(197.54, -142.04) * mm});
            skLineSegment(sketch, "E1549", {"start": v(197.54, -142.04) * mm, "end": v(196.46, -142.77) * mm});
            skLineSegment(sketch, "E1550", {"start": v(196.46, -142.77) * mm, "end": v(195.73, -143.85) * mm});
            skLineSegment(sketch, "E1551", {"start": v(195.73, -143.85) * mm, "end": v(195.46, -144.84) * mm});
            skLineSegment(sketch, "E1552", {"start": v(195.46, -144.84) * mm, "end": v(195.46, -145.17) * mm});
            skLineSegment(sketch, "E1553", {"start": v(195.46, -145.17) * mm, "end": v(195.46, -203.76) * mm});
            skLineSegment(sketch, "E1554", {"start": v(195.46, -203.76) * mm, "end": v(195.46, -204.09) * mm});
            skLineSegment(sketch, "E1555", {"start": v(195.46, -204.09) * mm, "end": v(195.73, -205.08) * mm});
            skLineSegment(sketch, "E1556", {"start": v(195.73, -205.08) * mm, "end": v(196.46, -206.16) * mm});
            skLineSegment(sketch, "E1557", {"start": v(196.46, -206.16) * mm, "end": v(197.54, -206.89) * mm});
            skLineSegment(sketch, "E1558", {"start": v(197.54, -206.89) * mm, "end": v(198.53, -207.16) * mm});
            skLineSegment(sketch, "E1559", {"start": v(198.53, -207.16) * mm, "end": v(198.86, -207.16) * mm});
            skLineSegment(sketch, "E1560", {"start": v(198.86, -207.16) * mm, "end": v(233.72, -207.16) * mm});
            skLineSegment(sketch, "E1561", {"start": v(233.72, -207.16) * mm, "end": v(234.04, -207.16) * mm});
            skLineSegment(sketch, "E1562", {"start": v(234.04, -207.16) * mm, "end": v(235.04, -206.89) * mm});
            skLineSegment(sketch, "E1563", {"start": v(235.04, -206.89) * mm, "end": v(236.12, -206.16) * mm});
            skLineSegment(sketch, "E1564", {"start": v(236.12, -206.16) * mm, "end": v(236.85, -205.08) * mm});
            skLineSegment(sketch, "E1565", {"start": v(236.85, -205.08) * mm, "end": v(237.12, -204.09) * mm});
            skLineSegment(sketch, "E1566", {"start": v(237.12, -204.09) * mm, "end": v(237.12, -203.76) * mm});
            skLineSegment(sketch, "E1567", {"start": v(237.12, -203.76) * mm, "end": v(237.12, -202.36) * mm});
            skLineSegment(sketch, "E1568", {"start": v(237.12, -202.36) * mm, "end": v(237.12, -202.03) * mm});
            skLineSegment(sketch, "E1569", {"start": v(237.12, -202.03) * mm, "end": v(236.85, -201.04) * mm});
            skLineSegment(sketch, "E1570", {"start": v(236.85, -201.04) * mm, "end": v(236.12, -199.96) * mm});
            skLineSegment(sketch, "E1571", {"start": v(236.12, -199.96) * mm, "end": v(235.04, -199.23) * mm});
            skLineSegment(sketch, "E1572", {"start": v(235.04, -199.23) * mm, "end": v(234.04, -198.96) * mm});
            skLineSegment(sketch, "E1573", {"start": v(234.04, -198.96) * mm, "end": v(233.72, -198.96) * mm});
            skLineSegment(sketch, "E1574", {"start": v(233.72, -198.96) * mm, "end": v(204.17, -198.96) * mm});
            skLineSegment(sketch, "E1575", {"start": v(204.17, -198.96) * mm, "end": v(204.17, -177.78) * mm});
            skLineSegment(sketch, "E1576", {"start": v(204.17, -177.78) * mm, "end": v(229.45, -177.78) * mm});
            skLineSegment(sketch, "E1577", {"start": v(229.45, -177.78) * mm, "end": v(229.79, -177.78) * mm});
            skLineSegment(sketch, "E1578", {"start": v(229.79, -177.78) * mm, "end": v(230.78, -177.5) * mm});
            skLineSegment(sketch, "E1579", {"start": v(230.78, -177.5) * mm, "end": v(231.86, -176.78) * mm});
            skLineSegment(sketch, "E1580", {"start": v(231.86, -176.78) * mm, "end": v(232.6, -175.7) * mm});
            skLineSegment(sketch, "E1581", {"start": v(232.6, -175.7) * mm, "end": v(232.86, -174.7) * mm});
            skLineSegment(sketch, "E1582", {"start": v(232.86, -174.7) * mm, "end": v(232.86, -174.38) * mm});
            skLineSegment(sketch, "E1583", {"start": v(232.86, -174.38) * mm, "end": v(232.86, -172.9) * mm});
            skLineSegment(sketch, "E1584", {"start": v(232.86, -172.9) * mm, "end": v(232.86, -172.57) * mm});
            skLineSegment(sketch, "E1585", {"start": v(232.86, -172.57) * mm, "end": v(232.6, -171.57) * mm});
            skLineSegment(sketch, "E1586", {"start": v(232.6, -171.57) * mm, "end": v(231.86, -170.5) * mm});
            skLineSegment(sketch, "E1587", {"start": v(231.86, -170.5) * mm, "end": v(230.78, -169.77) * mm});
            skLineSegment(sketch, "E1588", {"start": v(230.78, -169.77) * mm, "end": v(229.79, -169.5) * mm});
            skLineSegment(sketch, "E1589", {"start": v(229.79, -169.5) * mm, "end": v(229.45, -169.5) * mm});
            skLineSegment(sketch, "E1590", {"start": v(229.45, -169.5) * mm, "end": v(204.17, -169.5) * mm});
            skLineSegment(sketch, "E1591", {"start": v(204.17, -169.5) * mm, "end": v(204.17, -150.05) * mm});
            skLineSegment(sketch, "E1592", {"start": v(204.17, -150.05) * mm, "end": v(233.72, -150.05) * mm});
            skLineSegment(sketch, "E1593", {"start": v(233.72, -150.05) * mm, "end": v(234.04, -150.05) * mm});
            skLineSegment(sketch, "E1594", {"start": v(234.04, -150.05) * mm, "end": v(235.04, -149.78) * mm});
            skLineSegment(sketch, "E1595", {"start": v(235.04, -149.78) * mm, "end": v(236.12, -149.05) * mm});
            skLineSegment(sketch, "E1596", {"start": v(236.12, -149.05) * mm, "end": v(236.85, -147.97) * mm});
            skLineSegment(sketch, "E1597", {"start": v(236.85, -147.97) * mm, "end": v(237.12, -146.98) * mm});
            skLineSegment(sketch, "E1598", {"start": v(237.12, -146.98) * mm, "end": v(237.12, -146.65) * mm});
            skLineSegment(sketch, "E1599", {"start": v(237.12, -146.65) * mm, "end": v(237.12, -145.17) * mm});
            skLineSegment(sketch, "E1600", {"start": v(237.12, -145.17) * mm, "end": v(237.12, -144.84) * mm});
            skLineSegment(sketch, "E1601", {"start": v(237.12, -144.84) * mm, "end": v(236.85, -143.85) * mm});
            skLineSegment(sketch, "E1602", {"start": v(236.85, -143.85) * mm, "end": v(236.12, -142.77) * mm});
            skLineSegment(sketch, "E1603", {"start": v(236.12, -142.77) * mm, "end": v(235.04, -142.04) * mm});
            skLineSegment(sketch, "E1604", {"start": v(235.04, -142.04) * mm, "end": v(234.04, -141.77) * mm});
            skLineSegment(sketch, "E1605", {"start": v(234.04, -141.77) * mm, "end": v(233.72, -141.77) * mm});
            skLineSegment(sketch, "E1606", {"start": v(274.65, -182.45) * mm, "end": v(286.4, -155.26) * mm});
            skLineSegment(sketch, "E1607", {"start": v(286.4, -155.26) * mm, "end": v(297.93, -182.45) * mm});
            skLineSegment(sketch, "E1608", {"start": v(297.93, -182.45) * mm, "end": v(274.65, -182.45) * mm});
            skLineSegment(sketch, "E1609", {"start": v(289.71, -142.43) * mm, "end": v(289.66, -142.32) * mm});
            skLineSegment(sketch, "E1610", {"start": v(289.66, -142.32) * mm, "end": v(289.58, -142.17) * mm});
            skLineSegment(sketch, "E1611", {"start": v(289.58, -142.17) * mm, "end": v(289.29, -141.74) * mm});
            skLineSegment(sketch, "E1612", {"start": v(289.29, -141.74) * mm, "end": v(288.67, -141.13) * mm});
            skLineSegment(sketch, "E1613", {"start": v(288.67, -141.13) * mm, "end": v(287.76, -140.66) * mm});
            skLineSegment(sketch, "E1614", {"start": v(287.76, -140.66) * mm, "end": v(286.8, -140.46) * mm});
            skLineSegment(sketch, "E1615", {"start": v(286.8, -140.46) * mm, "end": v(286.5, -140.46) * mm});
            skLineSegment(sketch, "E1616", {"start": v(286.5, -140.46) * mm, "end": v(286.24, -140.46) * mm});
            skLineSegment(sketch, "E1617", {"start": v(286.24, -140.46) * mm, "end": v(286, -140.46) * mm});
            skLineSegment(sketch, "E1618", {"start": v(286, -140.46) * mm, "end": v(285.29, -140.6) * mm});
            skLineSegment(sketch, "E1619", {"start": v(285.29, -140.6) * mm, "end": v(284.42, -140.98) * mm});
            skLineSegment(sketch, "E1620", {"start": v(284.42, -140.98) * mm, "end": v(283.7, -141.57) * mm});
            skLineSegment(sketch, "E1621", {"start": v(283.7, -141.57) * mm, "end": v(283.26, -142.13) * mm});
            skLineSegment(sketch, "E1622", {"start": v(283.26, -142.13) * mm, "end": v(283.15, -142.34) * mm});
            skLineSegment(sketch, "E1623", {"start": v(283.15, -142.34) * mm, "end": v(256.34, -202.92) * mm});
            skLineSegment(sketch, "E1624", {"start": v(256.34, -202.92) * mm, "end": v(256.3, -203.04) * mm});
            skLineSegment(sketch, "E1625", {"start": v(256.3, -203.04) * mm, "end": v(256.2, -203.27) * mm});
            skLineSegment(sketch, "E1626", {"start": v(256.2, -203.27) * mm, "end": v(256.06, -204.03) * mm});
            skLineSegment(sketch, "E1627", {"start": v(256.06, -204.03) * mm, "end": v(256.1, -204.85) * mm});
            skLineSegment(sketch, "E1628", {"start": v(256.1, -204.85) * mm, "end": v(256.29, -205.49) * mm});
            skLineSegment(sketch, "E1629", {"start": v(256.29, -205.49) * mm, "end": v(256.47, -205.83) * mm});
            skLineSegment(sketch, "E1630", {"start": v(256.47, -205.83) * mm, "end": v(256.54, -205.93) * mm});
            skLineSegment(sketch, "E1631", {"start": v(256.54, -205.93) * mm, "end": v(256.67, -206.13) * mm});
            skLineSegment(sketch, "E1632", {"start": v(256.67, -206.13) * mm, "end": v(257.6, -206.84) * mm});
            skLineSegment(sketch, "E1633", {"start": v(257.6, -206.84) * mm, "end": v(258.67, -207.16) * mm});
            skLineSegment(sketch, "E1634", {"start": v(258.67, -207.16) * mm, "end": v(259.03, -207.16) * mm});
            skLineSegment(sketch, "E1635", {"start": v(259.03, -207.16) * mm, "end": v(261.46, -207.16) * mm});
            skLineSegment(sketch, "E1636", {"start": v(261.46, -207.16) * mm, "end": v(261.71, -207.16) * mm});
            skLineSegment(sketch, "E1637", {"start": v(261.71, -207.16) * mm, "end": v(262.46, -207.01) * mm});
            skLineSegment(sketch, "E1638", {"start": v(262.46, -207.01) * mm, "end": v(263.37, -206.6) * mm});
            skLineSegment(sketch, "E1639", {"start": v(263.37, -206.6) * mm, "end": v(264.14, -205.95) * mm});
            skLineSegment(sketch, "E1640", {"start": v(264.14, -205.95) * mm, "end": v(264.6, -205.33) * mm});
            skLineSegment(sketch, "E1641", {"start": v(264.6, -205.33) * mm, "end": v(264.72, -205.1) * mm});
            skLineSegment(sketch, "E1642", {"start": v(264.72, -205.1) * mm, "end": v(271.12, -190.38) * mm});
            skLineSegment(sketch, "E1643", {"start": v(271.12, -190.38) * mm, "end": v(301.35, -190.38) * mm});
            skLineSegment(sketch, "E1644", {"start": v(301.35, -190.38) * mm, "end": v(307.8, -205.02) * mm});
            skLineSegment(sketch, "E1645", {"start": v(307.8, -205.02) * mm, "end": v(307.85, -205.12) * mm});
            skLineSegment(sketch, "E1646", {"start": v(307.85, -205.12) * mm, "end": v(307.96, -205.34) * mm});
            skLineSegment(sketch, "E1647", {"start": v(307.96, -205.34) * mm, "end": v(308.43, -205.96) * mm});
            skLineSegment(sketch, "E1648", {"start": v(308.43, -205.96) * mm, "end": v(309.2, -206.6) * mm});
            skLineSegment(sketch, "E1649", {"start": v(309.2, -206.6) * mm, "end": v(310.1, -207.01) * mm});
            skLineSegment(sketch, "E1650", {"start": v(310.1, -207.01) * mm, "end": v(310.85, -207.16) * mm});
            skLineSegment(sketch, "E1651", {"start": v(310.85, -207.16) * mm, "end": v(311.1, -207.16) * mm});
            skLineSegment(sketch, "E1652", {"start": v(311.1, -207.16) * mm, "end": v(313.35, -207.16) * mm});
            skLineSegment(sketch, "E1653", {"start": v(313.35, -207.16) * mm, "end": v(313.6, -207.16) * mm});
            skLineSegment(sketch, "E1654", {"start": v(313.6, -207.16) * mm, "end": v(314.32, -207.05) * mm});
            skLineSegment(sketch, "E1655", {"start": v(314.32, -207.05) * mm, "end": v(315.06, -206.76) * mm});
            skLineSegment(sketch, "E1656", {"start": v(315.06, -206.76) * mm, "end": v(315.61, -206.37) * mm});
            skLineSegment(sketch, "E1657", {"start": v(315.61, -206.37) * mm, "end": v(315.9, -206.06) * mm});
            skLineSegment(sketch, "E1658", {"start": v(315.9, -206.06) * mm, "end": v(315.98, -205.94) * mm});
            skLineSegment(sketch, "E1659", {"start": v(315.98, -205.94) * mm, "end": v(316.07, -205.83) * mm});
            skLineSegment(sketch, "E1660", {"start": v(316.07, -205.83) * mm, "end": v(316.26, -205.46) * mm});
            skLineSegment(sketch, "E1661", {"start": v(316.26, -205.46) * mm, "end": v(316.46, -204.83) * mm});
            skLineSegment(sketch, "E1662", {"start": v(316.46, -204.83) * mm, "end": v(316.49, -204.04) * mm});
            skLineSegment(sketch, "E1663", {"start": v(316.49, -204.04) * mm, "end": v(316.36, -203.33) * mm});
            skLineSegment(sketch, "E1664", {"start": v(316.36, -203.33) * mm, "end": v(316.29, -203.1) * mm});
            skLineSegment(sketch, "E1665", {"start": v(316.29, -203.1) * mm, "end": v(289.71, -142.43) * mm});
            skLineSegment(sketch, "E1666", {"start": v(367.88, -141.77) * mm, "end": v(330.5, -141.77) * mm});
            skLineSegment(sketch, "E1667", {"start": v(330.5, -141.77) * mm, "end": v(330.16, -141.77) * mm});
            skLineSegment(sketch, "E1668", {"start": v(330.16, -141.77) * mm, "end": v(329.16, -142.03) * mm});
            skLineSegment(sketch, "E1669", {"start": v(329.16, -142.03) * mm, "end": v(328.08, -142.76) * mm});
            skLineSegment(sketch, "E1670", {"start": v(328.08, -142.76) * mm, "end": v(327.36, -143.83) * mm});
            skLineSegment(sketch, "E1671", {"start": v(327.36, -143.83) * mm, "end": v(327.1, -144.84) * mm});
            skLineSegment(sketch, "E1672", {"start": v(327.1, -144.84) * mm, "end": v(327.1, -145.17) * mm});
            skLineSegment(sketch, "E1673", {"start": v(327.1, -145.17) * mm, "end": v(327.1, -146.48) * mm});
            skLineSegment(sketch, "E1674", {"start": v(327.1, -146.48) * mm, "end": v(327.1, -146.88) * mm});
            skLineSegment(sketch, "E1675", {"start": v(327.1, -146.88) * mm, "end": v(327.39, -148.08) * mm});
            skLineSegment(sketch, "E1676", {"start": v(327.39, -148.08) * mm, "end": v(328.16, -149.19) * mm});
            skLineSegment(sketch, "E1677", {"start": v(328.16, -149.19) * mm, "end": v(329.25, -149.84) * mm});
            skLineSegment(sketch, "E1678", {"start": v(329.25, -149.84) * mm, "end": v(330.19, -150.05) * mm});
            skLineSegment(sketch, "E1679", {"start": v(330.19, -150.05) * mm, "end": v(330.5, -150.05) * mm});
            skLineSegment(sketch, "E1680", {"start": v(330.5, -150.05) * mm, "end": v(344.83, -150.05) * mm});
            skLineSegment(sketch, "E1681", {"start": v(344.83, -150.05) * mm, "end": v(344.83, -203.76) * mm});
            skLineSegment(sketch, "E1682", {"start": v(344.83, -203.76) * mm, "end": v(344.83, -204.09) * mm});
            skLineSegment(sketch, "E1683", {"start": v(344.83, -204.09) * mm, "end": v(345.1, -205.08) * mm});
            skLineSegment(sketch, "E1684", {"start": v(345.1, -205.08) * mm, "end": v(345.83, -206.16) * mm});
            skLineSegment(sketch, "E1685", {"start": v(345.83, -206.16) * mm, "end": v(346.9, -206.89) * mm});
            skLineSegment(sketch, "E1686", {"start": v(346.9, -206.89) * mm, "end": v(347.9, -207.16) * mm});
            skLineSegment(sketch, "E1687", {"start": v(347.9, -207.16) * mm, "end": v(348.23, -207.16) * mm});
            skLineSegment(sketch, "E1688", {"start": v(348.23, -207.16) * mm, "end": v(349.8, -207.16) * mm});
            skLineSegment(sketch, "E1689", {"start": v(349.8, -207.16) * mm, "end": v(350.15, -207.16) * mm});
            skLineSegment(sketch, "E1690", {"start": v(350.15, -207.16) * mm, "end": v(351.23, -206.9) * mm});
            skLineSegment(sketch, "E1691", {"start": v(351.23, -206.9) * mm, "end": v(352.4, -206.17) * mm});
            skLineSegment(sketch, "E1692", {"start": v(352.4, -206.17) * mm, "end": v(353.18, -205.1) * mm});
            skLineSegment(sketch, "E1693", {"start": v(353.18, -205.1) * mm, "end": v(353.46, -204.09) * mm});
            skLineSegment(sketch, "E1694", {"start": v(353.46, -204.09) * mm, "end": v(353.46, -203.76) * mm});
            skLineSegment(sketch, "E1695", {"start": v(353.46, -203.76) * mm, "end": v(353.46, -150.05) * mm});
            skLineSegment(sketch, "E1696", {"start": v(353.46, -150.05) * mm, "end": v(367.88, -150.05) * mm});
            skLineSegment(sketch, "E1697", {"start": v(367.88, -150.05) * mm, "end": v(368.21, -150.05) * mm});
            skLineSegment(sketch, "E1698", {"start": v(368.21, -150.05) * mm, "end": v(369.21, -149.79) * mm});
            skLineSegment(sketch, "E1699", {"start": v(369.21, -149.79) * mm, "end": v(370.3, -149.07) * mm});
            skLineSegment(sketch, "E1700", {"start": v(370.3, -149.07) * mm, "end": v(371.02, -147.99) * mm});
            skLineSegment(sketch, "E1701", {"start": v(371.02, -147.99) * mm, "end": v(371.28, -146.98) * mm});
            skLineSegment(sketch, "E1702", {"start": v(371.28, -146.98) * mm, "end": v(371.28, -146.65) * mm});
            skLineSegment(sketch, "E1703", {"start": v(371.28, -146.65) * mm, "end": v(371.28, -145.17) * mm});
            skLineSegment(sketch, "E1704", {"start": v(371.28, -145.17) * mm, "end": v(371.28, -144.84) * mm});
            skLineSegment(sketch, "E1705", {"start": v(371.28, -144.84) * mm, "end": v(371.02, -143.83) * mm});
            skLineSegment(sketch, "E1706", {"start": v(371.02, -143.83) * mm, "end": v(370.3, -142.76) * mm});
            skLineSegment(sketch, "E1707", {"start": v(370.3, -142.76) * mm, "end": v(369.21, -142.03) * mm});
            skLineSegment(sketch, "E1708", {"start": v(369.21, -142.03) * mm, "end": v(368.21, -141.77) * mm});
            skLineSegment(sketch, "E1709", {"start": v(368.21, -141.77) * mm, "end": v(367.88, -141.77) * mm});
            skSolve(sketch);
        }
        {
            var Q0;
            Q0 = qSketchRegion(id + "F0", true);
            extrude(context, id + "F1", {"entities" : qUnion([Q0]), "depth" : 25.4 * mm, "offsetDistance" : 25.4 * mm});
        }
        {
            var Q0;
            Q0=makeQuery(id+"F1.opExtrude","CAP_FACE",FACE,{"disambiguationData":[OSD([sQuery(id+"F0.wireOp",EDGE,"E842"),sQuery(id+"F0.wireOp",EDGE,"E843"),sQuery(id+"F0.wireOp",EDGE,"E844"),sQuery(id+"F0.wireOp",EDGE,"E845"),sQuery(id+"F0.wireOp",EDGE,"E846"),sQuery(id+"F0.wireOp",EDGE,"E847"),sQuery(id+"F0.wireOp",EDGE,"E848"),sQuery(id+"F0.wireOp",EDGE,"E849"),sQuery(id+"F0.wireOp",EDGE,"E850"),sQuery(id+"F0.wireOp",EDGE,"E851"),sQuery(id+"F0.wireOp",EDGE,"E852"),sQuery(id+"F0.wireOp",EDGE,"E853"),sQuery(id+"F0.wireOp",EDGE,"E854"),sQuery(id+"F0.wireOp",EDGE,"E855"),sQuery(id+"F0.wireOp",EDGE,"E856"),sQuery(id+"F0.wireOp",EDGE,"E857"),sQuery(id+"F0.wireOp",EDGE,"E858"),sQuery(id+"F0.wireOp",EDGE,"E859"),sQuery(id+"F0.wireOp",EDGE,"E860"),sQuery(id+"F0.wireOp",EDGE,"E861"),sQuery(id+"F0.wireOp",EDGE,"E862"),sQuery(id+"F0.wireOp",EDGE,"E863"),sQuery(id+"F0.wireOp",EDGE,"E864"),sQuery(id+"F0.wireOp",EDGE,"E865"),sQuery(id+"F0.wireOp",EDGE,"E866"),sQuery(id+"F0.wireOp",EDGE,"E867"),sQuery(id+"F0.wireOp",EDGE,"E868"),sQuery(id+"F0.wireOp",EDGE,"E869"),sQuery(id+"F0.wireOp",EDGE,"E870"),sQuery(id+"F0.wireOp",EDGE,"E871"),sQuery(id+"F0.wireOp",EDGE,"E872"),sQuery(id+"F0.wireOp",EDGE,"E873"),sQuery(id+"F0.wireOp",EDGE,"E874"),sQuery(id+"F0.wireOp",EDGE,"E875"),sQuery(id+"F0.wireOp",EDGE,"E876"),sQuery(id+"F0.wireOp",EDGE,"E877"),sQuery(id+"F0.wireOp",EDGE,"E878"),sQuery(id+"F0.wireOp",EDGE,"E879"),sQuery(id+"F0.wireOp",EDGE,"E880"),sQuery(id+"F0.wireOp",EDGE,"E881"),sQuery(id+"F0.wireOp",EDGE,"E882"),sQuery(id+"F0.wireOp",EDGE,"E883"),sQuery(id+"F0.wireOp",EDGE,"E884"),sQuery(id+"F0.wireOp",EDGE,"E885"),sQuery(id+"F0.wireOp",EDGE,"E886"),sQuery(id+"F0.wireOp",EDGE,"E887"),sQuery(id+"F0.wireOp",EDGE,"E888"),sQuery(id+"F0.wireOp",EDGE,"E889"),sQuery(id+"F0.wireOp",EDGE,"E890"),sQuery(id+"F0.wireOp",EDGE,"E891"),sQuery(id+"F0.wireOp",EDGE,"E892"),sQuery(id+"F0.wireOp",EDGE,"E893"),sQuery(id+"F0.wireOp",EDGE,"E894"),sQuery(id+"F0.wireOp",EDGE,"E895"),sQuery(id+"F0.wireOp",EDGE,"E896"),sQuery(id+"F0.wireOp",EDGE,"E897"),sQuery(id+"F0.wireOp",EDGE,"E898"),sQuery(id+"F0.wireOp",EDGE,"E899"),sQuery(id+"F0.wireOp",EDGE,"E900"),sQuery(id+"F0.wireOp",EDGE,"E901"),sQuery(id+"F0.wireOp",EDGE,"E902"),sQuery(id+"F0.wireOp",EDGE,"E903"),sQuery(id+"F0.wireOp",EDGE,"E904"),sQuery(id+"F0.wireOp",EDGE,"E905"),sQuery(id+"F0.wireOp",EDGE,"E906"),sQuery(id+"F0.wireOp",EDGE,"E907"),sQuery(id+"F0.wireOp",EDGE,"E908"),sQuery(id+"F0.wireOp",EDGE,"E909"),sQuery(id+"F0.wireOp",EDGE,"E910"),sQuery(id+"F0.wireOp",EDGE,"E911"),sQuery(id+"F0.wireOp",EDGE,"E912"),sQuery(id+"F0.wireOp",EDGE,"E913"),sQuery(id+"F0.wireOp",EDGE,"E914"),sQuery(id+"F0.wireOp",EDGE,"E915"),sQuery(id+"F0.wireOp",EDGE,"E916"),sQuery(id+"F0.wireOp",EDGE,"E917"),sQuery(id+"F0.wireOp",EDGE,"E918"),sQuery(id+"F0.wireOp",EDGE,"E919"),sQuery(id+"F0.wireOp",EDGE,"E920"),sQuery(id+"F0.wireOp",EDGE,"E921"),sQuery(id+"F0.wireOp",EDGE,"E922"),sQuery(id+"F0.wireOp",EDGE,"E923")])],"isStart":true});
            var Q1;
            Q1=makeQuery(id+"F1.opExtrude","CAP_FACE",FACE,{"disambiguationData":[OSD([sQuery(id+"F0.wireOp",EDGE,"E590"),sQuery(id+"F0.wireOp",EDGE,"E591"),sQuery(id+"F0.wireOp",EDGE,"E592"),sQuery(id+"F0.wireOp",EDGE,"E593"),sQuery(id+"F0.wireOp",EDGE,"E594"),sQuery(id+"F0.wireOp",EDGE,"E595"),sQuery(id+"F0.wireOp",EDGE,"E596"),sQuery(id+"F0.wireOp",EDGE,"E597"),sQuery(id+"F0.wireOp",EDGE,"E598"),sQuery(id+"F0.wireOp",EDGE,"E599"),sQuery(id+"F0.wireOp",EDGE,"E600"),sQuery(id+"F0.wireOp",EDGE,"E601"),sQuery(id+"F0.wireOp",EDGE,"E602"),sQuery(id+"F0.wireOp",EDGE,"E603"),sQuery(id+"F0.wireOp",EDGE,"E604"),sQuery(id+"F0.wireOp",EDGE,"E605"),sQuery(id+"F0.wireOp",EDGE,"E606"),sQuery(id+"F0.wireOp",EDGE,"E607"),sQuery(id+"F0.wireOp",EDGE,"E608"),sQuery(id+"F0.wireOp",EDGE,"E609"),sQuery(id+"F0.wireOp",EDGE,"E610"),sQuery(id+"F0.wireOp",EDGE,"E611"),sQuery(id+"F0.wireOp",EDGE,"E612"),sQuery(id+"F0.wireOp",EDGE,"E613"),sQuery(id+"F0.wireOp",EDGE,"E614"),sQuery(id+"F0.wireOp",EDGE,"E615"),sQuery(id+"F0.wireOp",EDGE,"E616"),sQuery(id+"F0.wireOp",EDGE,"E617"),sQuery(id+"F0.wireOp",EDGE,"E618"),sQuery(id+"F0.wireOp",EDGE,"E619"),sQuery(id+"F0.wireOp",EDGE,"E620"),sQuery(id+"F0.wireOp",EDGE,"E621"),sQuery(id+"F0.wireOp",EDGE,"E622"),sQuery(id+"F0.wireOp",EDGE,"E623"),sQuery(id+"F0.wireOp",EDGE,"E624"),sQuery(id+"F0.wireOp",EDGE,"E625"),sQuery(id+"F0.wireOp",EDGE,"E626"),sQuery(id+"F0.wireOp",EDGE,"E627"),sQuery(id+"F0.wireOp",EDGE,"E628"),sQuery(id+"F0.wireOp",EDGE,"E629"),sQuery(id+"F0.wireOp",EDGE,"E630"),sQuery(id+"F0.wireOp",EDGE,"E631"),sQuery(id+"F0.wireOp",EDGE,"E632"),sQuery(id+"F0.wireOp",EDGE,"E633"),sQuery(id+"F0.wireOp",EDGE,"E634"),sQuery(id+"F0.wireOp",EDGE,"E635"),sQuery(id+"F0.wireOp",EDGE,"E636"),sQuery(id+"F0.wireOp",EDGE,"E637"),sQuery(id+"F0.wireOp",EDGE,"E638"),sQuery(id+"F0.wireOp",EDGE,"E639"),sQuery(id+"F0.wireOp",EDGE,"E640"),sQuery(id+"F0.wireOp",EDGE,"E641"),sQuery(id+"F0.wireOp",EDGE,"E642"),sQuery(id+"F0.wireOp",EDGE,"E643"),sQuery(id+"F0.wireOp",EDGE,"E644"),sQuery(id+"F0.wireOp",EDGE,"E645"),sQuery(id+"F0.wireOp",EDGE,"E646"),sQuery(id+"F0.wireOp",EDGE,"E647"),sQuery(id+"F0.wireOp",EDGE,"E648"),sQuery(id+"F0.wireOp",EDGE,"E649"),sQuery(id+"F0.wireOp",EDGE,"E650"),sQuery(id+"F0.wireOp",EDGE,"E651"),sQuery(id+"F0.wireOp",EDGE,"E652"),sQuery(id+"F0.wireOp",EDGE,"E653"),sQuery(id+"F0.wireOp",EDGE,"E654"),sQuery(id+"F0.wireOp",EDGE,"E655"),sQuery(id+"F0.wireOp",EDGE,"E656"),sQuery(id+"F0.wireOp",EDGE,"E657"),sQuery(id+"F0.wireOp",EDGE,"E658"),sQuery(id+"F0.wireOp",EDGE,"E659"),sQuery(id+"F0.wireOp",EDGE,"E660"),sQuery(id+"F0.wireOp",EDGE,"E661"),sQuery(id+"F0.wireOp",EDGE,"E662"),sQuery(id+"F0.wireOp",EDGE,"E663"),sQuery(id+"F0.wireOp",EDGE,"E664"),sQuery(id+"F0.wireOp",EDGE,"E665"),sQuery(id+"F0.wireOp",EDGE,"E666"),sQuery(id+"F0.wireOp",EDGE,"E667"),sQuery(id+"F0.wireOp",EDGE,"E668"),sQuery(id+"F0.wireOp",EDGE,"E669"),sQuery(id+"F0.wireOp",EDGE,"E670"),sQuery(id+"F0.wireOp",EDGE,"E671"),sQuery(id+"F0.wireOp",EDGE,"E672"),sQuery(id+"F0.wireOp",EDGE,"E673"),sQuery(id+"F0.wireOp",EDGE,"E674"),sQuery(id+"F0.wireOp",EDGE,"E675"),sQuery(id+"F0.wireOp",EDGE,"E676"),sQuery(id+"F0.wireOp",EDGE,"E677"),sQuery(id+"F0.wireOp",EDGE,"E678"),sQuery(id+"F0.wireOp",EDGE,"E679"),sQuery(id+"F0.wireOp",EDGE,"E680"),sQuery(id+"F0.wireOp",EDGE,"E681"),sQuery(id+"F0.wireOp",EDGE,"E682"),sQuery(id+"F0.wireOp",EDGE,"E683"),sQuery(id+"F0.wireOp",EDGE,"E684"),sQuery(id+"F0.wireOp",EDGE,"E685"),sQuery(id+"F0.wireOp",EDGE,"E686"),sQuery(id+"F0.wireOp",EDGE,"E687"),sQuery(id+"F0.wireOp",EDGE,"E688"),sQuery(id+"F0.wireOp",EDGE,"E689"),sQuery(id+"F0.wireOp",EDGE,"E690"),sQuery(id+"F0.wireOp",EDGE,"E691"),sQuery(id+"F0.wireOp",EDGE,"E692"),sQuery(id+"F0.wireOp",EDGE,"E693"),sQuery(id+"F0.wireOp",EDGE,"E694"),sQuery(id+"F0.wireOp",EDGE,"E695"),sQuery(id+"F0.wireOp",EDGE,"E696"),sQuery(id+"F0.wireOp",EDGE,"E697"),sQuery(id+"F0.wireOp",EDGE,"E698"),sQuery(id+"F0.wireOp",EDGE,"E699"),sQuery(id+"F0.wireOp",EDGE,"E700"),sQuery(id+"F0.wireOp",EDGE,"E701"),sQuery(id+"F0.wireOp",EDGE,"E702"),sQuery(id+"F0.wireOp",EDGE,"E703"),sQuery(id+"F0.wireOp",EDGE,"E704"),sQuery(id+"F0.wireOp",EDGE,"E705"),sQuery(id+"F0.wireOp",EDGE,"E706"),sQuery(id+"F0.wireOp",EDGE,"E707"),sQuery(id+"F0.wireOp",EDGE,"E708"),sQuery(id+"F0.wireOp",EDGE,"E709"),sQuery(id+"F0.wireOp",EDGE,"E710"),sQuery(id+"F0.wireOp",EDGE,"E711"),sQuery(id+"F0.wireOp",EDGE,"E712"),sQuery(id+"F0.wireOp",EDGE,"E713"),sQuery(id+"F0.wireOp",EDGE,"E714"),sQuery(id+"F0.wireOp",EDGE,"E715"),sQuery(id+"F0.wireOp",EDGE,"E716"),sQuery(id+"F0.wireOp",EDGE,"E717"),sQuery(id+"F0.wireOp",EDGE,"E718"),sQuery(id+"F0.wireOp",EDGE,"E719"),sQuery(id+"F0.wireOp",EDGE,"E720"),sQuery(id+"F0.wireOp",EDGE,"E721"),sQuery(id+"F0.wireOp",EDGE,"E722"),sQuery(id+"F0.wireOp",EDGE,"E723"),sQuery(id+"F0.wireOp",EDGE,"E724"),sQuery(id+"F0.wireOp",EDGE,"E725"),sQuery(id+"F0.wireOp",EDGE,"E726"),sQuery(id+"F0.wireOp",EDGE,"E727"),sQuery(id+"F0.wireOp",EDGE,"E728"),sQuery(id+"F0.wireOp",EDGE,"E729"),sQuery(id+"F0.wireOp",EDGE,"E730"),sQuery(id+"F0.wireOp",EDGE,"E731"),sQuery(id+"F0.wireOp",EDGE,"E732"),sQuery(id+"F0.wireOp",EDGE,"E733"),sQuery(id+"F0.wireOp",EDGE,"E734"),sQuery(id+"F0.wireOp",EDGE,"E735"),sQuery(id+"F0.wireOp",EDGE,"E736"),sQuery(id+"F0.wireOp",EDGE,"E737"),sQuery(id+"F0.wireOp",EDGE,"E738"),sQuery(id+"F0.wireOp",EDGE,"E739"),sQuery(id+"F0.wireOp",EDGE,"E740"),sQuery(id+"F0.wireOp",EDGE,"E741"),sQuery(id+"F0.wireOp",EDGE,"E742"),sQuery(id+"F0.wireOp",EDGE,"E743"),sQuery(id+"F0.wireOp",EDGE,"E744"),sQuery(id+"F0.wireOp",EDGE,"E745"),sQuery(id+"F0.wireOp",EDGE,"E746"),sQuery(id+"F0.wireOp",EDGE,"E747"),sQuery(id+"F0.wireOp",EDGE,"E748"),sQuery(id+"F0.wireOp",EDGE,"E749"),sQuery(id+"F0.wireOp",EDGE,"E750"),sQuery(id+"F0.wireOp",EDGE,"E751"),sQuery(id+"F0.wireOp",EDGE,"E752"),sQuery(id+"F0.wireOp",EDGE,"E753"),sQuery(id+"F0.wireOp",EDGE,"E754"),sQuery(id+"F0.wireOp",EDGE,"E755"),sQuery(id+"F0.wireOp",EDGE,"E756"),sQuery(id+"F0.wireOp",EDGE,"E757"),sQuery(id+"F0.wireOp",EDGE,"E758"),sQuery(id+"F0.wireOp",EDGE,"E759"),sQuery(id+"F0.wireOp",EDGE,"E760"),sQuery(id+"F0.wireOp",EDGE,"E761"),sQuery(id+"F0.wireOp",EDGE,"E762"),sQuery(id+"F0.wireOp",EDGE,"E763"),sQuery(id+"F0.wireOp",EDGE,"E764"),sQuery(id+"F0.wireOp",EDGE,"E765"),sQuery(id+"F0.wireOp",EDGE,"E766"),sQuery(id+"F0.wireOp",EDGE,"E767"),sQuery(id+"F0.wireOp",EDGE,"E768"),sQuery(id+"F0.wireOp",EDGE,"E769"),sQuery(id+"F0.wireOp",EDGE,"E770"),sQuery(id+"F0.wireOp",EDGE,"E771"),sQuery(id+"F0.wireOp",EDGE,"E772"),sQuery(id+"F0.wireOp",EDGE,"E773"),sQuery(id+"F0.wireOp",EDGE,"E774"),sQuery(id+"F0.wireOp",EDGE,"E775"),sQuery(id+"F0.wireOp",EDGE,"E776"),sQuery(id+"F0.wireOp",EDGE,"E777"),sQuery(id+"F0.wireOp",EDGE,"E778"),sQuery(id+"F0.wireOp",EDGE,"E779"),sQuery(id+"F0.wireOp",EDGE,"E780"),sQuery(id+"F0.wireOp",EDGE,"E781"),sQuery(id+"F0.wireOp",EDGE,"E782"),sQuery(id+"F0.wireOp",EDGE,"E783"),sQuery(id+"F0.wireOp",EDGE,"E784"),sQuery(id+"F0.wireOp",EDGE,"E785"),sQuery(id+"F0.wireOp",EDGE,"E786"),sQuery(id+"F0.wireOp",EDGE,"E787"),sQuery(id+"F0.wireOp",EDGE,"E788"),sQuery(id+"F0.wireOp",EDGE,"E789"),sQuery(id+"F0.wireOp",EDGE,"E790"),sQuery(id+"F0.wireOp",EDGE,"E791"),sQuery(id+"F0.wireOp",EDGE,"E792"),sQuery(id+"F0.wireOp",EDGE,"E793"),sQuery(id+"F0.wireOp",EDGE,"E794"),sQuery(id+"F0.wireOp",EDGE,"E795"),sQuery(id+"F0.wireOp",EDGE,"E796"),sQuery(id+"F0.wireOp",EDGE,"E797"),sQuery(id+"F0.wireOp",EDGE,"E798"),sQuery(id+"F0.wireOp",EDGE,"E799"),sQuery(id+"F0.wireOp",EDGE,"E800"),sQuery(id+"F0.wireOp",EDGE,"E801"),sQuery(id+"F0.wireOp",EDGE,"E802"),sQuery(id+"F0.wireOp",EDGE,"E803"),sQuery(id+"F0.wireOp",EDGE,"E804"),sQuery(id+"F0.wireOp",EDGE,"E805"),sQuery(id+"F0.wireOp",EDGE,"E806"),sQuery(id+"F0.wireOp",EDGE,"E807"),sQuery(id+"F0.wireOp",EDGE,"E808"),sQuery(id+"F0.wireOp",EDGE,"E809"),sQuery(id+"F0.wireOp",EDGE,"E810"),sQuery(id+"F0.wireOp",EDGE,"E811"),sQuery(id+"F0.wireOp",EDGE,"E812"),sQuery(id+"F0.wireOp",EDGE,"E813"),sQuery(id+"F0.wireOp",EDGE,"E814"),sQuery(id+"F0.wireOp",EDGE,"E815"),sQuery(id+"F0.wireOp",EDGE,"E816"),sQuery(id+"F0.wireOp",EDGE,"E817"),sQuery(id+"F0.wireOp",EDGE,"E818"),sQuery(id+"F0.wireOp",EDGE,"E819"),sQuery(id+"F0.wireOp",EDGE,"E820"),sQuery(id+"F0.wireOp",EDGE,"E821"),sQuery(id+"F0.wireOp",EDGE,"E822"),sQuery(id+"F0.wireOp",EDGE,"E823"),sQuery(id+"F0.wireOp",EDGE,"E824"),sQuery(id+"F0.wireOp",EDGE,"E825"),sQuery(id+"F0.wireOp",EDGE,"E826"),sQuery(id+"F0.wireOp",EDGE,"E827"),sQuery(id+"F0.wireOp",EDGE,"E828"),sQuery(id+"F0.wireOp",EDGE,"E829"),sQuery(id+"F0.wireOp",EDGE,"E830"),sQuery(id+"F0.wireOp",EDGE,"E831"),sQuery(id+"F0.wireOp",EDGE,"E832"),sQuery(id+"F0.wireOp",EDGE,"E833"),sQuery(id+"F0.wireOp",EDGE,"E834"),sQuery(id+"F0.wireOp",EDGE,"E835"),sQuery(id+"F0.wireOp",EDGE,"E836"),sQuery(id+"F0.wireOp",EDGE,"E837"),sQuery(id+"F0.wireOp",EDGE,"E838"),sQuery(id+"F0.wireOp",EDGE,"E839"),sQuery(id+"F0.wireOp",EDGE,"E840"),sQuery(id+"F0.wireOp",EDGE,"E841")])],"isStart":true});
            var Q2;
            Q2=makeQuery(id+"F1.opExtrude","CAP_FACE",FACE,{"disambiguationData":[OSD([sQuery(id+"F0.wireOp",EDGE,"E520"),sQuery(id+"F0.wireOp",EDGE,"E521"),sQuery(id+"F0.wireOp",EDGE,"E522"),sQuery(id+"F0.wireOp",EDGE,"E523"),sQuery(id+"F0.wireOp",EDGE,"E524"),sQuery(id+"F0.wireOp",EDGE,"E525"),sQuery(id+"F0.wireOp",EDGE,"E526"),sQuery(id+"F0.wireOp",EDGE,"E527"),sQuery(id+"F0.wireOp",EDGE,"E528"),sQuery(id+"F0.wireOp",EDGE,"E529"),sQuery(id+"F0.wireOp",EDGE,"E530"),sQuery(id+"F0.wireOp",EDGE,"E531"),sQuery(id+"F0.wireOp",EDGE,"E532"),sQuery(id+"F0.wireOp",EDGE,"E533"),sQuery(id+"F0.wireOp",EDGE,"E534"),sQuery(id+"F0.wireOp",EDGE,"E535"),sQuery(id+"F0.wireOp",EDGE,"E536"),sQuery(id+"F0.wireOp",EDGE,"E537"),sQuery(id+"F0.wireOp",EDGE,"E538"),sQuery(id+"F0.wireOp",EDGE,"E539"),sQuery(id+"F0.wireOp",EDGE,"E540"),sQuery(id+"F0.wireOp",EDGE,"E541"),sQuery(id+"F0.wireOp",EDGE,"E542"),sQuery(id+"F0.wireOp",EDGE,"E543"),sQuery(id+"F0.wireOp",EDGE,"E544"),sQuery(id+"F0.wireOp",EDGE,"E545"),sQuery(id+"F0.wireOp",EDGE,"E546"),sQuery(id+"F0.wireOp",EDGE,"E547"),sQuery(id+"F0.wireOp",EDGE,"E548"),sQuery(id+"F0.wireOp",EDGE,"E549"),sQuery(id+"F0.wireOp",EDGE,"E550"),sQuery(id+"F0.wireOp",EDGE,"E551"),sQuery(id+"F0.wireOp",EDGE,"E552"),sQuery(id+"F0.wireOp",EDGE,"E553"),sQuery(id+"F0.wireOp",EDGE,"E554"),sQuery(id+"F0.wireOp",EDGE,"E555"),sQuery(id+"F0.wireOp",EDGE,"E556"),sQuery(id+"F0.wireOp",EDGE,"E557"),sQuery(id+"F0.wireOp",EDGE,"E558"),sQuery(id+"F0.wireOp",EDGE,"E559"),sQuery(id+"F0.wireOp",EDGE,"E560"),sQuery(id+"F0.wireOp",EDGE,"E561"),sQuery(id+"F0.wireOp",EDGE,"E562"),sQuery(id+"F0.wireOp",EDGE,"E563"),sQuery(id+"F0.wireOp",EDGE,"E564"),sQuery(id+"F0.wireOp",EDGE,"E565"),sQuery(id+"F0.wireOp",EDGE,"E566"),sQuery(id+"F0.wireOp",EDGE,"E567"),sQuery(id+"F0.wireOp",EDGE,"E568"),sQuery(id+"F0.wireOp",EDGE,"E569"),sQuery(id+"F0.wireOp",EDGE,"E570"),sQuery(id+"F0.wireOp",EDGE,"E571"),sQuery(id+"F0.wireOp",EDGE,"E572"),sQuery(id+"F0.wireOp",EDGE,"E573"),sQuery(id+"F0.wireOp",EDGE,"E574"),sQuery(id+"F0.wireOp",EDGE,"E575"),sQuery(id+"F0.wireOp",EDGE,"E576"),sQuery(id+"F0.wireOp",EDGE,"E577"),sQuery(id+"F0.wireOp",EDGE,"E578"),sQuery(id+"F0.wireOp",EDGE,"E579"),sQuery(id+"F0.wireOp",EDGE,"E580"),sQuery(id+"F0.wireOp",EDGE,"E581"),sQuery(id+"F0.wireOp",EDGE,"E582"),sQuery(id+"F0.wireOp",EDGE,"E583"),sQuery(id+"F0.wireOp",EDGE,"E584"),sQuery(id+"F0.wireOp",EDGE,"E585"),sQuery(id+"F0.wireOp",EDGE,"E586"),sQuery(id+"F0.wireOp",EDGE,"E587"),sQuery(id+"F0.wireOp",EDGE,"E588"),sQuery(id+"F0.wireOp",EDGE,"E589")])],"isStart":true});
            var Q3;
            Q3=makeQuery(id+"F1.opExtrude","CAP_FACE",FACE,{"disambiguationData":[OSD([sQuery(id+"F0.wireOp",EDGE,"E448"),sQuery(id+"F0.wireOp",EDGE,"E449"),sQuery(id+"F0.wireOp",EDGE,"E450"),sQuery(id+"F0.wireOp",EDGE,"E451"),sQuery(id+"F0.wireOp",EDGE,"E452"),sQuery(id+"F0.wireOp",EDGE,"E453"),sQuery(id+"F0.wireOp",EDGE,"E454"),sQuery(id+"F0.wireOp",EDGE,"E455"),sQuery(id+"F0.wireOp",EDGE,"E456"),sQuery(id+"F0.wireOp",EDGE,"E457"),sQuery(id+"F0.wireOp",EDGE,"E458"),sQuery(id+"F0.wireOp",EDGE,"E459"),sQuery(id+"F0.wireOp",EDGE,"E460"),sQuery(id+"F0.wireOp",EDGE,"E461"),sQuery(id+"F0.wireOp",EDGE,"E462"),sQuery(id+"F0.wireOp",EDGE,"E463"),sQuery(id+"F0.wireOp",EDGE,"E464"),sQuery(id+"F0.wireOp",EDGE,"E465"),sQuery(id+"F0.wireOp",EDGE,"E466"),sQuery(id+"F0.wireOp",EDGE,"E467"),sQuery(id+"F0.wireOp",EDGE,"E468"),sQuery(id+"F0.wireOp",EDGE,"E469"),sQuery(id+"F0.wireOp",EDGE,"E470"),sQuery(id+"F0.wireOp",EDGE,"E471"),sQuery(id+"F0.wireOp",EDGE,"E472"),sQuery(id+"F0.wireOp",EDGE,"E473"),sQuery(id+"F0.wireOp",EDGE,"E474"),sQuery(id+"F0.wireOp",EDGE,"E475"),sQuery(id+"F0.wireOp",EDGE,"E476"),sQuery(id+"F0.wireOp",EDGE,"E477"),sQuery(id+"F0.wireOp",EDGE,"E478"),sQuery(id+"F0.wireOp",EDGE,"E479"),sQuery(id+"F0.wireOp",EDGE,"E480"),sQuery(id+"F0.wireOp",EDGE,"E481"),sQuery(id+"F0.wireOp",EDGE,"E482"),sQuery(id+"F0.wireOp",EDGE,"E483"),sQuery(id+"F0.wireOp",EDGE,"E484"),sQuery(id+"F0.wireOp",EDGE,"E485"),sQuery(id+"F0.wireOp",EDGE,"E486"),sQuery(id+"F0.wireOp",EDGE,"E487"),sQuery(id+"F0.wireOp",EDGE,"E488"),sQuery(id+"F0.wireOp",EDGE,"E489"),sQuery(id+"F0.wireOp",EDGE,"E490"),sQuery(id+"F0.wireOp",EDGE,"E491"),sQuery(id+"F0.wireOp",EDGE,"E492"),sQuery(id+"F0.wireOp",EDGE,"E493"),sQuery(id+"F0.wireOp",EDGE,"E494"),sQuery(id+"F0.wireOp",EDGE,"E495"),sQuery(id+"F0.wireOp",EDGE,"E496"),sQuery(id+"F0.wireOp",EDGE,"E497"),sQuery(id+"F0.wireOp",EDGE,"E498"),sQuery(id+"F0.wireOp",EDGE,"E499"),sQuery(id+"F0.wireOp",EDGE,"E500"),sQuery(id+"F0.wireOp",EDGE,"E501"),sQuery(id+"F0.wireOp",EDGE,"E502"),sQuery(id+"F0.wireOp",EDGE,"E503"),sQuery(id+"F0.wireOp",EDGE,"E504"),sQuery(id+"F0.wireOp",EDGE,"E505"),sQuery(id+"F0.wireOp",EDGE,"E506"),sQuery(id+"F0.wireOp",EDGE,"E507"),sQuery(id+"F0.wireOp",EDGE,"E508"),sQuery(id+"F0.wireOp",EDGE,"E509"),sQuery(id+"F0.wireOp",EDGE,"E510"),sQuery(id+"F0.wireOp",EDGE,"E511"),sQuery(id+"F0.wireOp",EDGE,"E512"),sQuery(id+"F0.wireOp",EDGE,"E513"),sQuery(id+"F0.wireOp",EDGE,"E514"),sQuery(id+"F0.wireOp",EDGE,"E515"),sQuery(id+"F0.wireOp",EDGE,"E516"),sQuery(id+"F0.wireOp",EDGE,"E517"),sQuery(id+"F0.wireOp",EDGE,"E518"),sQuery(id+"F0.wireOp",EDGE,"E519")])],"isStart":true});
            var Q4;
            Q4=makeQuery(id+"F1.opExtrude","CAP_FACE",FACE,{"disambiguationData":[OSD([sQuery(id+"F0.wireOp",EDGE,"E206"),sQuery(id+"F0.wireOp",EDGE,"E207"),sQuery(id+"F0.wireOp",EDGE,"E208"),sQuery(id+"F0.wireOp",EDGE,"E209"),sQuery(id+"F0.wireOp",EDGE,"E210"),sQuery(id+"F0.wireOp",EDGE,"E211"),sQuery(id+"F0.wireOp",EDGE,"E212"),sQuery(id+"F0.wireOp",EDGE,"E213"),sQuery(id+"F0.wireOp",EDGE,"E214"),sQuery(id+"F0.wireOp",EDGE,"E215"),sQuery(id+"F0.wireOp",EDGE,"E216"),sQuery(id+"F0.wireOp",EDGE,"E217"),sQuery(id+"F0.wireOp",EDGE,"E218"),sQuery(id+"F0.wireOp",EDGE,"E219"),sQuery(id+"F0.wireOp",EDGE,"E220"),sQuery(id+"F0.wireOp",EDGE,"E221"),sQuery(id+"F0.wireOp",EDGE,"E222"),sQuery(id+"F0.wireOp",EDGE,"E223"),sQuery(id+"F0.wireOp",EDGE,"E224"),sQuery(id+"F0.wireOp",EDGE,"E225"),sQuery(id+"F0.wireOp",EDGE,"E226"),sQuery(id+"F0.wireOp",EDGE,"E227"),sQuery(id+"F0.wireOp",EDGE,"E228"),sQuery(id+"F0.wireOp",EDGE,"E229"),sQuery(id+"F0.wireOp",EDGE,"E230"),sQuery(id+"F0.wireOp",EDGE,"E231"),sQuery(id+"F0.wireOp",EDGE,"E232"),sQuery(id+"F0.wireOp",EDGE,"E233"),sQuery(id+"F0.wireOp",EDGE,"E234"),sQuery(id+"F0.wireOp",EDGE,"E235"),sQuery(id+"F0.wireOp",EDGE,"E236"),sQuery(id+"F0.wireOp",EDGE,"E237"),sQuery(id+"F0.wireOp",EDGE,"E238"),sQuery(id+"F0.wireOp",EDGE,"E239"),sQuery(id+"F0.wireOp",EDGE,"E240"),sQuery(id+"F0.wireOp",EDGE,"E241"),sQuery(id+"F0.wireOp",EDGE,"E242"),sQuery(id+"F0.wireOp",EDGE,"E243"),sQuery(id+"F0.wireOp",EDGE,"E244"),sQuery(id+"F0.wireOp",EDGE,"E245"),sQuery(id+"F0.wireOp",EDGE,"E246"),sQuery(id+"F0.wireOp",EDGE,"E247"),sQuery(id+"F0.wireOp",EDGE,"E248"),sQuery(id+"F0.wireOp",EDGE,"E249"),sQuery(id+"F0.wireOp",EDGE,"E250"),sQuery(id+"F0.wireOp",EDGE,"E251"),sQuery(id+"F0.wireOp",EDGE,"E252"),sQuery(id+"F0.wireOp",EDGE,"E253"),sQuery(id+"F0.wireOp",EDGE,"E254"),sQuery(id+"F0.wireOp",EDGE,"E255"),sQuery(id+"F0.wireOp",EDGE,"E256"),sQuery(id+"F0.wireOp",EDGE,"E257"),sQuery(id+"F0.wireOp",EDGE,"E258"),sQuery(id+"F0.wireOp",EDGE,"E259"),sQuery(id+"F0.wireOp",EDGE,"E260"),sQuery(id+"F0.wireOp",EDGE,"E261"),sQuery(id+"F0.wireOp",EDGE,"E262"),sQuery(id+"F0.wireOp",EDGE,"E263"),sQuery(id+"F0.wireOp",EDGE,"E264"),sQuery(id+"F0.wireOp",EDGE,"E265"),sQuery(id+"F0.wireOp",EDGE,"E266"),sQuery(id+"F0.wireOp",EDGE,"E267"),sQuery(id+"F0.wireOp",EDGE,"E268"),sQuery(id+"F0.wireOp",EDGE,"E269"),sQuery(id+"F0.wireOp",EDGE,"E270"),sQuery(id+"F0.wireOp",EDGE,"E271"),sQuery(id+"F0.wireOp",EDGE,"E272"),sQuery(id+"F0.wireOp",EDGE,"E273"),sQuery(id+"F0.wireOp",EDGE,"E274"),sQuery(id+"F0.wireOp",EDGE,"E275"),sQuery(id+"F0.wireOp",EDGE,"E276"),sQuery(id+"F0.wireOp",EDGE,"E277"),sQuery(id+"F0.wireOp",EDGE,"E278"),sQuery(id+"F0.wireOp",EDGE,"E279"),sQuery(id+"F0.wireOp",EDGE,"E280"),sQuery(id+"F0.wireOp",EDGE,"E281"),sQuery(id+"F0.wireOp",EDGE,"E282"),sQuery(id+"F0.wireOp",EDGE,"E283"),sQuery(id+"F0.wireOp",EDGE,"E284"),sQuery(id+"F0.wireOp",EDGE,"E285"),sQuery(id+"F0.wireOp",EDGE,"E286"),sQuery(id+"F0.wireOp",EDGE,"E287"),sQuery(id+"F0.wireOp",EDGE,"E288"),sQuery(id+"F0.wireOp",EDGE,"E289"),sQuery(id+"F0.wireOp",EDGE,"E290"),sQuery(id+"F0.wireOp",EDGE,"E291"),sQuery(id+"F0.wireOp",EDGE,"E292"),sQuery(id+"F0.wireOp",EDGE,"E293"),sQuery(id+"F0.wireOp",EDGE,"E294"),sQuery(id+"F0.wireOp",EDGE,"E295"),sQuery(id+"F0.wireOp",EDGE,"E296"),sQuery(id+"F0.wireOp",EDGE,"E297"),sQuery(id+"F0.wireOp",EDGE,"E298"),sQuery(id+"F0.wireOp",EDGE,"E299"),sQuery(id+"F0.wireOp",EDGE,"E300"),sQuery(id+"F0.wireOp",EDGE,"E301"),sQuery(id+"F0.wireOp",EDGE,"E302"),sQuery(id+"F0.wireOp",EDGE,"E303"),sQuery(id+"F0.wireOp",EDGE,"E304"),sQuery(id+"F0.wireOp",EDGE,"E305"),sQuery(id+"F0.wireOp",EDGE,"E306"),sQuery(id+"F0.wireOp",EDGE,"E307"),sQuery(id+"F0.wireOp",EDGE,"E308"),sQuery(id+"F0.wireOp",EDGE,"E309"),sQuery(id+"F0.wireOp",EDGE,"E310"),sQuery(id+"F0.wireOp",EDGE,"E311"),sQuery(id+"F0.wireOp",EDGE,"E312"),sQuery(id+"F0.wireOp",EDGE,"E313"),sQuery(id+"F0.wireOp",EDGE,"E314"),sQuery(id+"F0.wireOp",EDGE,"E315"),sQuery(id+"F0.wireOp",EDGE,"E316"),sQuery(id+"F0.wireOp",EDGE,"E317"),sQuery(id+"F0.wireOp",EDGE,"E318"),sQuery(id+"F0.wireOp",EDGE,"E319"),sQuery(id+"F0.wireOp",EDGE,"E320"),sQuery(id+"F0.wireOp",EDGE,"E321"),sQuery(id+"F0.wireOp",EDGE,"E322"),sQuery(id+"F0.wireOp",EDGE,"E323"),sQuery(id+"F0.wireOp",EDGE,"E324"),sQuery(id+"F0.wireOp",EDGE,"E325"),sQuery(id+"F0.wireOp",EDGE,"E326"),sQuery(id+"F0.wireOp",EDGE,"E327"),sQuery(id+"F0.wireOp",EDGE,"E328"),sQuery(id+"F0.wireOp",EDGE,"E329"),sQuery(id+"F0.wireOp",EDGE,"E330"),sQuery(id+"F0.wireOp",EDGE,"E331"),sQuery(id+"F0.wireOp",EDGE,"E332"),sQuery(id+"F0.wireOp",EDGE,"E333"),sQuery(id+"F0.wireOp",EDGE,"E334"),sQuery(id+"F0.wireOp",EDGE,"E335"),sQuery(id+"F0.wireOp",EDGE,"E336"),sQuery(id+"F0.wireOp",EDGE,"E337"),sQuery(id+"F0.wireOp",EDGE,"E338"),sQuery(id+"F0.wireOp",EDGE,"E339"),sQuery(id+"F0.wireOp",EDGE,"E340"),sQuery(id+"F0.wireOp",EDGE,"E341"),sQuery(id+"F0.wireOp",EDGE,"E342"),sQuery(id+"F0.wireOp",EDGE,"E343"),sQuery(id+"F0.wireOp",EDGE,"E344"),sQuery(id+"F0.wireOp",EDGE,"E345"),sQuery(id+"F0.wireOp",EDGE,"E346"),sQuery(id+"F0.wireOp",EDGE,"E347"),sQuery(id+"F0.wireOp",EDGE,"E348"),sQuery(id+"F0.wireOp",EDGE,"E349"),sQuery(id+"F0.wireOp",EDGE,"E350"),sQuery(id+"F0.wireOp",EDGE,"E351"),sQuery(id+"F0.wireOp",EDGE,"E352"),sQuery(id+"F0.wireOp",EDGE,"E353"),sQuery(id+"F0.wireOp",EDGE,"E354"),sQuery(id+"F0.wireOp",EDGE,"E355"),sQuery(id+"F0.wireOp",EDGE,"E356"),sQuery(id+"F0.wireOp",EDGE,"E357"),sQuery(id+"F0.wireOp",EDGE,"E358"),sQuery(id+"F0.wireOp",EDGE,"E359"),sQuery(id+"F0.wireOp",EDGE,"E360"),sQuery(id+"F0.wireOp",EDGE,"E361"),sQuery(id+"F0.wireOp",EDGE,"E362"),sQuery(id+"F0.wireOp",EDGE,"E363"),sQuery(id+"F0.wireOp",EDGE,"E364"),sQuery(id+"F0.wireOp",EDGE,"E365"),sQuery(id+"F0.wireOp",EDGE,"E366"),sQuery(id+"F0.wireOp",EDGE,"E367"),sQuery(id+"F0.wireOp",EDGE,"E368"),sQuery(id+"F0.wireOp",EDGE,"E369"),sQuery(id+"F0.wireOp",EDGE,"E370"),sQuery(id+"F0.wireOp",EDGE,"E371"),sQuery(id+"F0.wireOp",EDGE,"E372"),sQuery(id+"F0.wireOp",EDGE,"E373"),sQuery(id+"F0.wireOp",EDGE,"E374"),sQuery(id+"F0.wireOp",EDGE,"E375"),sQuery(id+"F0.wireOp",EDGE,"E376"),sQuery(id+"F0.wireOp",EDGE,"E377"),sQuery(id+"F0.wireOp",EDGE,"E378"),sQuery(id+"F0.wireOp",EDGE,"E379"),sQuery(id+"F0.wireOp",EDGE,"E380"),sQuery(id+"F0.wireOp",EDGE,"E381"),sQuery(id+"F0.wireOp",EDGE,"E382"),sQuery(id+"F0.wireOp",EDGE,"E383"),sQuery(id+"F0.wireOp",EDGE,"E384"),sQuery(id+"F0.wireOp",EDGE,"E385"),sQuery(id+"F0.wireOp",EDGE,"E386"),sQuery(id+"F0.wireOp",EDGE,"E387"),sQuery(id+"F0.wireOp",EDGE,"E388"),sQuery(id+"F0.wireOp",EDGE,"E389"),sQuery(id+"F0.wireOp",EDGE,"E390"),sQuery(id+"F0.wireOp",EDGE,"E391"),sQuery(id+"F0.wireOp",EDGE,"E392"),sQuery(id+"F0.wireOp",EDGE,"E393"),sQuery(id+"F0.wireOp",EDGE,"E394"),sQuery(id+"F0.wireOp",EDGE,"E395"),sQuery(id+"F0.wireOp",EDGE,"E396"),sQuery(id+"F0.wireOp",EDGE,"E397"),sQuery(id+"F0.wireOp",EDGE,"E398"),sQuery(id+"F0.wireOp",EDGE,"E399"),sQuery(id+"F0.wireOp",EDGE,"E400"),sQuery(id+"F0.wireOp",EDGE,"E401"),sQuery(id+"F0.wireOp",EDGE,"E402"),sQuery(id+"F0.wireOp",EDGE,"E403"),sQuery(id+"F0.wireOp",EDGE,"E404"),sQuery(id+"F0.wireOp",EDGE,"E405"),sQuery(id+"F0.wireOp",EDGE,"E406"),sQuery(id+"F0.wireOp",EDGE,"E407"),sQuery(id+"F0.wireOp",EDGE,"E408"),sQuery(id+"F0.wireOp",EDGE,"E409"),sQuery(id+"F0.wireOp",EDGE,"E410"),sQuery(id+"F0.wireOp",EDGE,"E411"),sQuery(id+"F0.wireOp",EDGE,"E412"),sQuery(id+"F0.wireOp",EDGE,"E413"),sQuery(id+"F0.wireOp",EDGE,"E414"),sQuery(id+"F0.wireOp",EDGE,"E415"),sQuery(id+"F0.wireOp",EDGE,"E416"),sQuery(id+"F0.wireOp",EDGE,"E417"),sQuery(id+"F0.wireOp",EDGE,"E418"),sQuery(id+"F0.wireOp",EDGE,"E419"),sQuery(id+"F0.wireOp",EDGE,"E420"),sQuery(id+"F0.wireOp",EDGE,"E421"),sQuery(id+"F0.wireOp",EDGE,"E422"),sQuery(id+"F0.wireOp",EDGE,"E423"),sQuery(id+"F0.wireOp",EDGE,"E424"),sQuery(id+"F0.wireOp",EDGE,"E425"),sQuery(id+"F0.wireOp",EDGE,"E426"),sQuery(id+"F0.wireOp",EDGE,"E427"),sQuery(id+"F0.wireOp",EDGE,"E428"),sQuery(id+"F0.wireOp",EDGE,"E429"),sQuery(id+"F0.wireOp",EDGE,"E430"),sQuery(id+"F0.wireOp",EDGE,"E431"),sQuery(id+"F0.wireOp",EDGE,"E432"),sQuery(id+"F0.wireOp",EDGE,"E433"),sQuery(id+"F0.wireOp",EDGE,"E434"),sQuery(id+"F0.wireOp",EDGE,"E435"),sQuery(id+"F0.wireOp",EDGE,"E436"),sQuery(id+"F0.wireOp",EDGE,"E437"),sQuery(id+"F0.wireOp",EDGE,"E438"),sQuery(id+"F0.wireOp",EDGE,"E439"),sQuery(id+"F0.wireOp",EDGE,"E440"),sQuery(id+"F0.wireOp",EDGE,"E441"),sQuery(id+"F0.wireOp",EDGE,"E442"),sQuery(id+"F0.wireOp",EDGE,"E443"),sQuery(id+"F0.wireOp",EDGE,"E444"),sQuery(id+"F0.wireOp",EDGE,"E445"),sQuery(id+"F0.wireOp",EDGE,"E446"),sQuery(id+"F0.wireOp",EDGE,"E447")])],"isStart":true});
            var Q5;
            Q5=makeQuery(id+"F1.opExtrude","CAP_FACE",FACE,{"disambiguationData":[OSD([sQuery(id+"F0.wireOp",EDGE,"E156"),sQuery(id+"F0.wireOp",EDGE,"E157"),sQuery(id+"F0.wireOp",EDGE,"E158"),sQuery(id+"F0.wireOp",EDGE,"E159"),sQuery(id+"F0.wireOp",EDGE,"E160"),sQuery(id+"F0.wireOp",EDGE,"E161"),sQuery(id+"F0.wireOp",EDGE,"E162"),sQuery(id+"F0.wireOp",EDGE,"E163"),sQuery(id+"F0.wireOp",EDGE,"E164"),sQuery(id+"F0.wireOp",EDGE,"E165")])],"isStart":true});
            var Q6;
            Q6=makeQuery(id+"F1.opExtrude","CAP_FACE",FACE,{"disambiguationData":[OSD([sQuery(id+"F0.wireOp",EDGE,"E166"),sQuery(id+"F0.wireOp",EDGE,"E167"),sQuery(id+"F0.wireOp",EDGE,"E168"),sQuery(id+"F0.wireOp",EDGE,"E169"),sQuery(id+"F0.wireOp",EDGE,"E170"),sQuery(id+"F0.wireOp",EDGE,"E171"),sQuery(id+"F0.wireOp",EDGE,"E172"),sQuery(id+"F0.wireOp",EDGE,"E173"),sQuery(id+"F0.wireOp",EDGE,"E174"),sQuery(id+"F0.wireOp",EDGE,"E175"),sQuery(id+"F0.wireOp",EDGE,"E176"),sQuery(id+"F0.wireOp",EDGE,"E177"),sQuery(id+"F0.wireOp",EDGE,"E178"),sQuery(id+"F0.wireOp",EDGE,"E179"),sQuery(id+"F0.wireOp",EDGE,"E180"),sQuery(id+"F0.wireOp",EDGE,"E181"),sQuery(id+"F0.wireOp",EDGE,"E182"),sQuery(id+"F0.wireOp",EDGE,"E183"),sQuery(id+"F0.wireOp",EDGE,"E184"),sQuery(id+"F0.wireOp",EDGE,"E185"),sQuery(id+"F0.wireOp",EDGE,"E186"),sQuery(id+"F0.wireOp",EDGE,"E187"),sQuery(id+"F0.wireOp",EDGE,"E188"),sQuery(id+"F0.wireOp",EDGE,"E189"),sQuery(id+"F0.wireOp",EDGE,"E190"),sQuery(id+"F0.wireOp",EDGE,"E191"),sQuery(id+"F0.wireOp",EDGE,"E192"),sQuery(id+"F0.wireOp",EDGE,"E193"),sQuery(id+"F0.wireOp",EDGE,"E194"),sQuery(id+"F0.wireOp",EDGE,"E195"),sQuery(id+"F0.wireOp",EDGE,"E196"),sQuery(id+"F0.wireOp",EDGE,"E197"),sQuery(id+"F0.wireOp",EDGE,"E198"),sQuery(id+"F0.wireOp",EDGE,"E199"),sQuery(id+"F0.wireOp",EDGE,"E200"),sQuery(id+"F0.wireOp",EDGE,"E201"),sQuery(id+"F0.wireOp",EDGE,"E202"),sQuery(id+"F0.wireOp",EDGE,"E203"),sQuery(id+"F0.wireOp",EDGE,"E204"),sQuery(id+"F0.wireOp",EDGE,"E205")])],"isStart":true});
            var Q7;
            Q7=makeQuery(id+"F1.opExtrude","CAP_FACE",FACE,{"disambiguationData":[OSD([sQuery(id+"F0.wireOp",EDGE,"E82"),sQuery(id+"F0.wireOp",EDGE,"E83"),sQuery(id+"F0.wireOp",EDGE,"E84"),sQuery(id+"F0.wireOp",EDGE,"E85"),sQuery(id+"F0.wireOp",EDGE,"E86"),sQuery(id+"F0.wireOp",EDGE,"E87"),sQuery(id+"F0.wireOp",EDGE,"E88"),sQuery(id+"F0.wireOp",EDGE,"E89"),sQuery(id+"F0.wireOp",EDGE,"E90"),sQuery(id+"F0.wireOp",EDGE,"E91"),sQuery(id+"F0.wireOp",EDGE,"E92"),sQuery(id+"F0.wireOp",EDGE,"E93"),sQuery(id+"F0.wireOp",EDGE,"E94"),sQuery(id+"F0.wireOp",EDGE,"E95"),sQuery(id+"F0.wireOp",EDGE,"E96"),sQuery(id+"F0.wireOp",EDGE,"E97"),sQuery(id+"F0.wireOp",EDGE,"E98"),sQuery(id+"F0.wireOp",EDGE,"E99"),sQuery(id+"F0.wireOp",EDGE,"E100"),sQuery(id+"F0.wireOp",EDGE,"E101"),sQuery(id+"F0.wireOp",EDGE,"E102"),sQuery(id+"F0.wireOp",EDGE,"E103"),sQuery(id+"F0.wireOp",EDGE,"E104"),sQuery(id+"F0.wireOp",EDGE,"E105"),sQuery(id+"F0.wireOp",EDGE,"E106"),sQuery(id+"F0.wireOp",EDGE,"E107"),sQuery(id+"F0.wireOp",EDGE,"E108"),sQuery(id+"F0.wireOp",EDGE,"E109"),sQuery(id+"F0.wireOp",EDGE,"E110"),sQuery(id+"F0.wireOp",EDGE,"E111"),sQuery(id+"F0.wireOp",EDGE,"E112"),sQuery(id+"F0.wireOp",EDGE,"E113"),sQuery(id+"F0.wireOp",EDGE,"E114"),sQuery(id+"F0.wireOp",EDGE,"E115"),sQuery(id+"F0.wireOp",EDGE,"E116"),sQuery(id+"F0.wireOp",EDGE,"E117"),sQuery(id+"F0.wireOp",EDGE,"E118"),sQuery(id+"F0.wireOp",EDGE,"E119"),sQuery(id+"F0.wireOp",EDGE,"E120"),sQuery(id+"F0.wireOp",EDGE,"E121"),sQuery(id+"F0.wireOp",EDGE,"E122"),sQuery(id+"F0.wireOp",EDGE,"E123"),sQuery(id+"F0.wireOp",EDGE,"E124"),sQuery(id+"F0.wireOp",EDGE,"E125"),sQuery(id+"F0.wireOp",EDGE,"E126"),sQuery(id+"F0.wireOp",EDGE,"E127"),sQuery(id+"F0.wireOp",EDGE,"E128"),sQuery(id+"F0.wireOp",EDGE,"E129"),sQuery(id+"F0.wireOp",EDGE,"E130"),sQuery(id+"F0.wireOp",EDGE,"E131"),sQuery(id+"F0.wireOp",EDGE,"E132"),sQuery(id+"F0.wireOp",EDGE,"E133"),sQuery(id+"F0.wireOp",EDGE,"E134"),sQuery(id+"F0.wireOp",EDGE,"E135"),sQuery(id+"F0.wireOp",EDGE,"E136"),sQuery(id+"F0.wireOp",EDGE,"E137"),sQuery(id+"F0.wireOp",EDGE,"E138"),sQuery(id+"F0.wireOp",EDGE,"E139"),sQuery(id+"F0.wireOp",EDGE,"E140"),sQuery(id+"F0.wireOp",EDGE,"E141"),sQuery(id+"F0.wireOp",EDGE,"E142"),sQuery(id+"F0.wireOp",EDGE,"E143"),sQuery(id+"F0.wireOp",EDGE,"E144"),sQuery(id+"F0.wireOp",EDGE,"E145"),sQuery(id+"F0.wireOp",EDGE,"E146"),sQuery(id+"F0.wireOp",EDGE,"E147"),sQuery(id+"F0.wireOp",EDGE,"E148"),sQuery(id+"F0.wireOp",EDGE,"E149"),sQuery(id+"F0.wireOp",EDGE,"E150"),sQuery(id+"F0.wireOp",EDGE,"E151"),sQuery(id+"F0.wireOp",EDGE,"E152"),sQuery(id+"F0.wireOp",EDGE,"E153"),sQuery(id+"F0.wireOp",EDGE,"E154"),sQuery(id+"F0.wireOp",EDGE,"E155")])],"isStart":true});
            var Q8;
            Q8=makeQuery(id+"F1.opExtrude","CAP_FACE",FACE,{"disambiguationData":[OSD([sQuery(id+"F0.wireOp",EDGE,"E0"),sQuery(id+"F0.wireOp",EDGE,"E1"),sQuery(id+"F0.wireOp",EDGE,"E2"),sQuery(id+"F0.wireOp",EDGE,"E3"),sQuery(id+"F0.wireOp",EDGE,"E4"),sQuery(id+"F0.wireOp",EDGE,"E5"),sQuery(id+"F0.wireOp",EDGE,"E6"),sQuery(id+"F0.wireOp",EDGE,"E7"),sQuery(id+"F0.wireOp",EDGE,"E8"),sQuery(id+"F0.wireOp",EDGE,"E9"),sQuery(id+"F0.wireOp",EDGE,"E10"),sQuery(id+"F0.wireOp",EDGE,"E11"),sQuery(id+"F0.wireOp",EDGE,"E12"),sQuery(id+"F0.wireOp",EDGE,"E13"),sQuery(id+"F0.wireOp",EDGE,"E14"),sQuery(id+"F0.wireOp",EDGE,"E15"),sQuery(id+"F0.wireOp",EDGE,"E16"),sQuery(id+"F0.wireOp",EDGE,"E17"),sQuery(id+"F0.wireOp",EDGE,"E18"),sQuery(id+"F0.wireOp",EDGE,"E19"),sQuery(id+"F0.wireOp",EDGE,"E20"),sQuery(id+"F0.wireOp",EDGE,"E21"),sQuery(id+"F0.wireOp",EDGE,"E22"),sQuery(id+"F0.wireOp",EDGE,"E23"),sQuery(id+"F0.wireOp",EDGE,"E24"),sQuery(id+"F0.wireOp",EDGE,"E25"),sQuery(id+"F0.wireOp",EDGE,"E26"),sQuery(id+"F0.wireOp",EDGE,"E27"),sQuery(id+"F0.wireOp",EDGE,"E28"),sQuery(id+"F0.wireOp",EDGE,"E29"),sQuery(id+"F0.wireOp",EDGE,"E30"),sQuery(id+"F0.wireOp",EDGE,"E31"),sQuery(id+"F0.wireOp",EDGE,"E32"),sQuery(id+"F0.wireOp",EDGE,"E33"),sQuery(id+"F0.wireOp",EDGE,"E34"),sQuery(id+"F0.wireOp",EDGE,"E35"),sQuery(id+"F0.wireOp",EDGE,"E36"),sQuery(id+"F0.wireOp",EDGE,"E37"),sQuery(id+"F0.wireOp",EDGE,"E38"),sQuery(id+"F0.wireOp",EDGE,"E39"),sQuery(id+"F0.wireOp",EDGE,"E40"),sQuery(id+"F0.wireOp",EDGE,"E41"),sQuery(id+"F0.wireOp",EDGE,"E42"),sQuery(id+"F0.wireOp",EDGE,"E43"),sQuery(id+"F0.wireOp",EDGE,"E44"),sQuery(id+"F0.wireOp",EDGE,"E45"),sQuery(id+"F0.wireOp",EDGE,"E46"),sQuery(id+"F0.wireOp",EDGE,"E47"),sQuery(id+"F0.wireOp",EDGE,"E48"),sQuery(id+"F0.wireOp",EDGE,"E49"),sQuery(id+"F0.wireOp",EDGE,"E50"),sQuery(id+"F0.wireOp",EDGE,"E51"),sQuery(id+"F0.wireOp",EDGE,"E52"),sQuery(id+"F0.wireOp",EDGE,"E53"),sQuery(id+"F0.wireOp",EDGE,"E54"),sQuery(id+"F0.wireOp",EDGE,"E55"),sQuery(id+"F0.wireOp",EDGE,"E56"),sQuery(id+"F0.wireOp",EDGE,"E57"),sQuery(id+"F0.wireOp",EDGE,"E58"),sQuery(id+"F0.wireOp",EDGE,"E59"),sQuery(id+"F0.wireOp",EDGE,"E60"),sQuery(id+"F0.wireOp",EDGE,"E61"),sQuery(id+"F0.wireOp",EDGE,"E62"),sQuery(id+"F0.wireOp",EDGE,"E63"),sQuery(id+"F0.wireOp",EDGE,"E64"),sQuery(id+"F0.wireOp",EDGE,"E65"),sQuery(id+"F0.wireOp",EDGE,"E66"),sQuery(id+"F0.wireOp",EDGE,"E67"),sQuery(id+"F0.wireOp",EDGE,"E68"),sQuery(id+"F0.wireOp",EDGE,"E69"),sQuery(id+"F0.wireOp",EDGE,"E70"),sQuery(id+"F0.wireOp",EDGE,"E71"),sQuery(id+"F0.wireOp",EDGE,"E72"),sQuery(id+"F0.wireOp",EDGE,"E73"),sQuery(id+"F0.wireOp",EDGE,"E74"),sQuery(id+"F0.wireOp",EDGE,"E75"),sQuery(id+"F0.wireOp",EDGE,"E76"),sQuery(id+"F0.wireOp",EDGE,"E77"),sQuery(id+"F0.wireOp",EDGE,"E78"),sQuery(id+"F0.wireOp",EDGE,"E79"),sQuery(id+"F0.wireOp",EDGE,"E80"),sQuery(id+"F0.wireOp",EDGE,"E81")])],"isStart":true});
            shell(context, id + "F2", {"entities" : qUnion([Q0, Q1, Q2, Q3, Q4, Q5, Q6, Q7, Q8]), "thickness" : 3.17 * mm});
        }
        {
            var Q0;
            Q0=makeQuery(id+"F2.opShell","OFFSET_FACE",FACE,{"disambiguationData":[OSD([sQuery(id+"F0.wireOp",EDGE,"E448"),sQuery(id+"F0.wireOp",EDGE,"E449"),sQuery(id+"F0.wireOp",EDGE,"E450"),sQuery(id+"F0.wireOp",EDGE,"E451"),sQuery(id+"F0.wireOp",EDGE,"E452"),sQuery(id+"F0.wireOp",EDGE,"E453"),sQuery(id+"F0.wireOp",EDGE,"E454"),sQuery(id+"F0.wireOp",EDGE,"E455"),sQuery(id+"F0.wireOp",EDGE,"E456"),sQuery(id+"F0.wireOp",EDGE,"E457"),sQuery(id+"F0.wireOp",EDGE,"E458"),sQuery(id+"F0.wireOp",EDGE,"E459"),sQuery(id+"F0.wireOp",EDGE,"E460"),sQuery(id+"F0.wireOp",EDGE,"E461"),sQuery(id+"F0.wireOp",EDGE,"E462"),sQuery(id+"F0.wireOp",EDGE,"E463"),sQuery(id+"F0.wireOp",EDGE,"E464"),sQuery(id+"F0.wireOp",EDGE,"E465"),sQuery(id+"F0.wireOp",EDGE,"E466"),sQuery(id+"F0.wireOp",EDGE,"E467"),sQuery(id+"F0.wireOp",EDGE,"E468"),sQuery(id+"F0.wireOp",EDGE,"E469"),sQuery(id+"F0.wireOp",EDGE,"E470"),sQuery(id+"F0.wireOp",EDGE,"E471"),sQuery(id+"F0.wireOp",EDGE,"E472"),sQuery(id+"F0.wireOp",EDGE,"E473"),sQuery(id+"F0.wireOp",EDGE,"E474"),sQuery(id+"F0.wireOp",EDGE,"E475"),sQuery(id+"F0.wireOp",EDGE,"E476"),sQuery(id+"F0.wireOp",EDGE,"E477"),sQuery(id+"F0.wireOp",EDGE,"E478"),sQuery(id+"F0.wireOp",EDGE,"E479"),sQuery(id+"F0.wireOp",EDGE,"E480"),sQuery(id+"F0.wireOp",EDGE,"E481"),sQuery(id+"F0.wireOp",EDGE,"E482"),sQuery(id+"F0.wireOp",EDGE,"E483"),sQuery(id+"F0.wireOp",EDGE,"E484"),sQuery(id+"F0.wireOp",EDGE,"E485"),sQuery(id+"F0.wireOp",EDGE,"E486"),sQuery(id+"F0.wireOp",EDGE,"E487"),sQuery(id+"F0.wireOp",EDGE,"E488"),sQuery(id+"F0.wireOp",EDGE,"E489"),sQuery(id+"F0.wireOp",EDGE,"E490"),sQuery(id+"F0.wireOp",EDGE,"E491"),sQuery(id+"F0.wireOp",EDGE,"E492"),sQuery(id+"F0.wireOp",EDGE,"E493"),sQuery(id+"F0.wireOp",EDGE,"E494"),sQuery(id+"F0.wireOp",EDGE,"E495"),sQuery(id+"F0.wireOp",EDGE,"E496"),sQuery(id+"F0.wireOp",EDGE,"E497"),sQuery(id+"F0.wireOp",EDGE,"E498"),sQuery(id+"F0.wireOp",EDGE,"E499"),sQuery(id+"F0.wireOp",EDGE,"E500"),sQuery(id+"F0.wireOp",EDGE,"E501"),sQuery(id+"F0.wireOp",EDGE,"E502"),sQuery(id+"F0.wireOp",EDGE,"E503"),sQuery(id+"F0.wireOp",EDGE,"E504"),sQuery(id+"F0.wireOp",EDGE,"E505"),sQuery(id+"F0.wireOp",EDGE,"E506"),sQuery(id+"F0.wireOp",EDGE,"E507"),sQuery(id+"F0.wireOp",EDGE,"E508"),sQuery(id+"F0.wireOp",EDGE,"E509"),sQuery(id+"F0.wireOp",EDGE,"E510"),sQuery(id+"F0.wireOp",EDGE,"E511"),sQuery(id+"F0.wireOp",EDGE,"E512"),sQuery(id+"F0.wireOp",EDGE,"E513"),sQuery(id+"F0.wireOp",EDGE,"E514"),sQuery(id+"F0.wireOp",EDGE,"E515"),sQuery(id+"F0.wireOp",EDGE,"E516"),sQuery(id+"F0.wireOp",EDGE,"E517"),sQuery(id+"F0.wireOp",EDGE,"E518"),sQuery(id+"F0.wireOp",EDGE,"E519")])]});
            var sketch = newSketch(context, id + "F3", { "sketchPlane" : qUnion([Q0])});
            skCircle(sketch, "E1710", {"center": v(-844.42, 111.57) * mm, "radius": 2.38 * mm});
            skCircle(sketch, "E1711", {"center": v(-666.4, 77.97) * mm, "radius": 2.38 * mm});
            skCircle(sketch, "E1712", {"center": v(-616.43, 38.34) * mm, "radius": 2.38 * mm});
            skCircle(sketch, "E1713", {"center": v(-570.76, -4.74) * mm, "radius": 2.38 * mm});
            skCircle(sketch, "E1714", {"center": v(849.04, 111.57) * mm, "radius": 2.38 * mm});
            skCircle(sketch, "E1715", {"center": v(350.4, 173.96) * mm, "radius": 2.38 * mm});
            skCircle(sketch, "E1716", {"center": v(647.44, 144.3) * mm, "radius": 2.38 * mm});
            skCircle(sketch, "E1717", {"center": v(647.44, -4.74) * mm, "radius": 2.38 * mm});
            skCircle(sketch, "E1718", {"center": v(528.55, 31.45) * mm, "radius": 2.38 * mm});
            skCircle(sketch, "E1719", {"center": v(349.9, 80.55) * mm, "radius": 2.38 * mm});
            skCircle(sketch, "E1720", {"center": v(349.9, -4.74) * mm, "radius": 2.38 * mm});
            skCircle(sketch, "E1721", {"center": v(86.58, 73.66) * mm, "radius": 2.38 * mm});
            skCircle(sketch, "E1722", {"center": v(86.58, -1.94) * mm, "radius": 2.38 * mm});
            skCircle(sketch, "E1723", {"center": v(185.05, -1.94) * mm, "radius": 2.38 * mm});
            skCircle(sketch, "E1724", {"center": v(175.8, 73.66) * mm, "radius": 2.38 * mm});
            skCircle(sketch, "E1725", {"center": v(-91.75, 80.55) * mm, "radius": 2.38 * mm});
            skCircle(sketch, "E1726", {"center": v(-91.75, -1.94) * mm, "radius": 2.38 * mm});
            skCircle(sketch, "E1727", {"center": v(-294.7, 80.55) * mm, "radius": 2.38 * mm});
            skCircle(sketch, "E1728", {"center": v(-294.7, -4.74) * mm, "radius": 2.38 * mm});
            skCircle(sketch, "E1729", {"center": v(-409.77, 80.55) * mm, "radius": 2.38 * mm});
            skCircle(sketch, "E1730", {"center": v(-409.77, -4.74) * mm, "radius": 2.38 * mm});
            skCircle(sketch, "E1731", {"center": v(-844.42, -1.26) * mm, "radius": 2.38 * mm});
            skCircle(sketch, "E1732", {"center": v(849.04, 0.46) * mm, "radius": 2.38 * mm});
            skSolve(sketch);
        }
        {
            var Q0;
            Q0=makeQuery(id+"F3.imprint","IMPRINT",FACE,{"disambiguationData":[TD([[makeQuery(id+"F3.imprint","IMPRINT",EDGE,{"derivedFrom":sQuery(id+"F3.wireOp",EDGE,"E1719")}),1.0]])]});
            var Q1;
            Q1=makeQuery(id+"F3.imprint","IMPRINT",FACE,{"disambiguationData":[TD([[makeQuery(id+"F3.imprint","IMPRINT",EDGE,{"derivedFrom":sQuery(id+"F3.wireOp",EDGE,"E1720")}),1.0]])]});
            var Q2;
            Q2=makeQuery(id+"F3.imprint","IMPRINT",FACE,{"disambiguationData":[TD([[makeQuery(id+"F3.imprint","IMPRINT",EDGE,{"derivedFrom":sQuery(id+"F3.wireOp",EDGE,"E1715")}),1.0]])]});
            var Q3;
            Q3=makeQuery(id+"F3.imprint","IMPRINT",FACE,{"disambiguationData":[TD([[makeQuery(id+"F3.imprint","IMPRINT",EDGE,{"derivedFrom":sQuery(id+"F3.wireOp",EDGE,"E1714")}),1.0]])]});
            var Q4;
            Q4=makeQuery(id+"F3.imprint","IMPRINT",FACE,{"disambiguationData":[TD([[makeQuery(id+"F3.imprint","IMPRINT",EDGE,{"derivedFrom":sQuery(id+"F3.wireOp",EDGE,"E1732")}),1.0]])]});
            var Q5;
            Q5=makeQuery(id+"F3.imprint","IMPRINT",FACE,{"disambiguationData":[TD([[makeQuery(id+"F3.imprint","IMPRINT",EDGE,{"derivedFrom":sQuery(id+"F3.wireOp",EDGE,"E1716")}),1.0]])]});
            var Q6;
            Q6=makeQuery(id+"F3.imprint","IMPRINT",FACE,{"disambiguationData":[TD([[makeQuery(id+"F3.imprint","IMPRINT",EDGE,{"derivedFrom":sQuery(id+"F3.wireOp",EDGE,"E1717")}),1.0]])]});
            var Q7;
            Q7=makeQuery(id+"F3.imprint","IMPRINT",FACE,{"disambiguationData":[TD([[makeQuery(id+"F3.imprint","IMPRINT",EDGE,{"derivedFrom":sQuery(id+"F3.wireOp",EDGE,"E1718")}),1.0]])]});
            var Q8;
            Q8=makeQuery(id+"F3.imprint","IMPRINT",FACE,{"disambiguationData":[TD([[makeQuery(id+"F3.imprint","IMPRINT",EDGE,{"derivedFrom":sQuery(id+"F3.wireOp",EDGE,"E1721")}),1.0]])]});
            var Q9;
            Q9=makeQuery(id+"F3.imprint","IMPRINT",FACE,{"disambiguationData":[TD([[makeQuery(id+"F3.imprint","IMPRINT",EDGE,{"derivedFrom":sQuery(id+"F3.wireOp",EDGE,"E1724")}),1.0]])]});
            var Q10;
            Q10=makeQuery(id+"F3.imprint","IMPRINT",FACE,{"disambiguationData":[TD([[makeQuery(id+"F3.imprint","IMPRINT",EDGE,{"derivedFrom":sQuery(id+"F3.wireOp",EDGE,"E1723")}),1.0]])]});
            var Q11;
            Q11=makeQuery(id+"F3.imprint","IMPRINT",FACE,{"disambiguationData":[TD([[makeQuery(id+"F3.imprint","IMPRINT",EDGE,{"derivedFrom":sQuery(id+"F3.wireOp",EDGE,"E1722")}),1.0]])]});
            var Q12;
            Q12=makeQuery(id+"F3.imprint","IMPRINT",FACE,{"disambiguationData":[TD([[makeQuery(id+"F3.imprint","IMPRINT",EDGE,{"derivedFrom":sQuery(id+"F3.wireOp",EDGE,"E1725")}),1.0]])]});
            var Q13;
            Q13=makeQuery(id+"F3.imprint","IMPRINT",FACE,{"disambiguationData":[TD([[makeQuery(id+"F3.imprint","IMPRINT",EDGE,{"derivedFrom":sQuery(id+"F3.wireOp",EDGE,"E1726")}),1.0]])]});
            var Q14;
            Q14=makeQuery(id+"F3.imprint","IMPRINT",FACE,{"disambiguationData":[TD([[makeQuery(id+"F3.imprint","IMPRINT",EDGE,{"derivedFrom":sQuery(id+"F3.wireOp",EDGE,"E1729")}),1.0]])]});
            var Q15;
            Q15=makeQuery(id+"F3.imprint","IMPRINT",FACE,{"disambiguationData":[TD([[makeQuery(id+"F3.imprint","IMPRINT",EDGE,{"derivedFrom":sQuery(id+"F3.wireOp",EDGE,"E1727")}),1.0]])]});
            var Q16;
            Q16=makeQuery(id+"F3.imprint","IMPRINT",FACE,{"disambiguationData":[TD([[makeQuery(id+"F3.imprint","IMPRINT",EDGE,{"derivedFrom":sQuery(id+"F3.wireOp",EDGE,"E1728")}),1.0]])]});
            var Q17;
            Q17=makeQuery(id+"F3.imprint","IMPRINT",FACE,{"disambiguationData":[TD([[makeQuery(id+"F3.imprint","IMPRINT",EDGE,{"derivedFrom":sQuery(id+"F3.wireOp",EDGE,"E1730")}),1.0]])]});
            var Q18;
            Q18=makeQuery(id+"F3.imprint","IMPRINT",FACE,{"disambiguationData":[TD([[makeQuery(id+"F3.imprint","IMPRINT",EDGE,{"derivedFrom":sQuery(id+"F3.wireOp",EDGE,"E1710")}),1.0]])]});
            var Q19;
            Q19=makeQuery(id+"F3.imprint","IMPRINT",FACE,{"disambiguationData":[TD([[makeQuery(id+"F3.imprint","IMPRINT",EDGE,{"derivedFrom":sQuery(id+"F3.wireOp",EDGE,"E1731")}),1.0]])]});
            var Q20;
            Q20=makeQuery(id+"F3.imprint","IMPRINT",FACE,{"disambiguationData":[TD([[makeQuery(id+"F3.imprint","IMPRINT",EDGE,{"derivedFrom":sQuery(id+"F3.wireOp",EDGE,"E1711")}),1.0]])]});
            var Q21;
            Q21=makeQuery(id+"F3.imprint","IMPRINT",FACE,{"disambiguationData":[TD([[makeQuery(id+"F3.imprint","IMPRINT",EDGE,{"derivedFrom":sQuery(id+"F3.wireOp",EDGE,"E1712")}),1.0]])]});
            var Q22;
            Q22=makeQuery(id+"F3.imprint","IMPRINT",FACE,{"disambiguationData":[TD([[makeQuery(id+"F3.imprint","IMPRINT",EDGE,{"derivedFrom":sQuery(id+"F3.wireOp",EDGE,"E1713")}),1.0]])]});
            extrude(context, id + "F4", {"entities" : qUnion([Q0, Q1, Q2, Q3, Q4, Q5, Q6, Q7, Q8, Q9, Q10, Q11, Q12, Q13, Q14, Q15, Q16, Q17, Q18, Q19, Q20, Q21, Q22]), "operationType" : NewBodyOperationType.ADD, "depth" : 98.42 * mm, "offsetDistance" : 25.4 * mm});
        }
        {
            var Q0;
            Q0=makeQuery(id+"F1.opExtrude","CAP_FACE",FACE,{"disambiguationData":[OSD([sQuery(id+"F0.wireOp",EDGE,"E1666"),sQuery(id+"F0.wireOp",EDGE,"E1667"),sQuery(id+"F0.wireOp",EDGE,"E1668"),sQuery(id+"F0.wireOp",EDGE,"E1669"),sQuery(id+"F0.wireOp",EDGE,"E1670"),sQuery(id+"F0.wireOp",EDGE,"E1671"),sQuery(id+"F0.wireOp",EDGE,"E1672"),sQuery(id+"F0.wireOp",EDGE,"E1673"),sQuery(id+"F0.wireOp",EDGE,"E1674"),sQuery(id+"F0.wireOp",EDGE,"E1675"),sQuery(id+"F0.wireOp",EDGE,"E1676"),sQuery(id+"F0.wireOp",EDGE,"E1677"),sQuery(id+"F0.wireOp",EDGE,"E1678"),sQuery(id+"F0.wireOp",EDGE,"E1679"),sQuery(id+"F0.wireOp",EDGE,"E1680"),sQuery(id+"F0.wireOp",EDGE,"E1681"),sQuery(id+"F0.wireOp",EDGE,"E1682"),sQuery(id+"F0.wireOp",EDGE,"E1683"),sQuery(id+"F0.wireOp",EDGE,"E1684"),sQuery(id+"F0.wireOp",EDGE,"E1685"),sQuery(id+"F0.wireOp",EDGE,"E1686"),sQuery(id+"F0.wireOp",EDGE,"E1687"),sQuery(id+"F0.wireOp",EDGE,"E1688"),sQuery(id+"F0.wireOp",EDGE,"E1689"),sQuery(id+"F0.wireOp",EDGE,"E1690"),sQuery(id+"F0.wireOp",EDGE,"E1691"),sQuery(id+"F0.wireOp",EDGE,"E1692"),sQuery(id+"F0.wireOp",EDGE,"E1693"),sQuery(id+"F0.wireOp",EDGE,"E1694"),sQuery(id+"F0.wireOp",EDGE,"E1695"),sQuery(id+"F0.wireOp",EDGE,"E1696"),sQuery(id+"F0.wireOp",EDGE,"E1697"),sQuery(id+"F0.wireOp",EDGE,"E1698"),sQuery(id+"F0.wireOp",EDGE,"E1699"),sQuery(id+"F0.wireOp",EDGE,"E1700"),sQuery(id+"F0.wireOp",EDGE,"E1701"),sQuery(id+"F0.wireOp",EDGE,"E1702"),sQuery(id+"F0.wireOp",EDGE,"E1703"),sQuery(id+"F0.wireOp",EDGE,"E1704"),sQuery(id+"F0.wireOp",EDGE,"E1705"),sQuery(id+"F0.wireOp",EDGE,"E1706"),sQuery(id+"F0.wireOp",EDGE,"E1707"),sQuery(id+"F0.wireOp",EDGE,"E1708"),sQuery(id+"F0.wireOp",EDGE,"E1709")])],"isStart":true});
            var Q1;
            Q1=makeQuery(id+"F1.opExtrude","CAP_FACE",FACE,{"disambiguationData":[OSD([sQuery(id+"F0.wireOp",EDGE,"E1606"),sQuery(id+"F0.wireOp",EDGE,"E1607"),sQuery(id+"F0.wireOp",EDGE,"E1608"),sQuery(id+"F0.wireOp",EDGE,"E1609"),sQuery(id+"F0.wireOp",EDGE,"E1610"),sQuery(id+"F0.wireOp",EDGE,"E1611"),sQuery(id+"F0.wireOp",EDGE,"E1612"),sQuery(id+"F0.wireOp",EDGE,"E1613"),sQuery(id+"F0.wireOp",EDGE,"E1614"),sQuery(id+"F0.wireOp",EDGE,"E1615"),sQuery(id+"F0.wireOp",EDGE,"E1616"),sQuery(id+"F0.wireOp",EDGE,"E1617"),sQuery(id+"F0.wireOp",EDGE,"E1618"),sQuery(id+"F0.wireOp",EDGE,"E1619"),sQuery(id+"F0.wireOp",EDGE,"E1620"),sQuery(id+"F0.wireOp",EDGE,"E1621"),sQuery(id+"F0.wireOp",EDGE,"E1622"),sQuery(id+"F0.wireOp",EDGE,"E1623"),sQuery(id+"F0.wireOp",EDGE,"E1624"),sQuery(id+"F0.wireOp",EDGE,"E1625"),sQuery(id+"F0.wireOp",EDGE,"E1626"),sQuery(id+"F0.wireOp",EDGE,"E1627"),sQuery(id+"F0.wireOp",EDGE,"E1628"),sQuery(id+"F0.wireOp",EDGE,"E1629"),sQuery(id+"F0.wireOp",EDGE,"E1630"),sQuery(id+"F0.wireOp",EDGE,"E1631"),sQuery(id+"F0.wireOp",EDGE,"E1632"),sQuery(id+"F0.wireOp",EDGE,"E1633"),sQuery(id+"F0.wireOp",EDGE,"E1634"),sQuery(id+"F0.wireOp",EDGE,"E1635"),sQuery(id+"F0.wireOp",EDGE,"E1636"),sQuery(id+"F0.wireOp",EDGE,"E1637"),sQuery(id+"F0.wireOp",EDGE,"E1638"),sQuery(id+"F0.wireOp",EDGE,"E1639"),sQuery(id+"F0.wireOp",EDGE,"E1640"),sQuery(id+"F0.wireOp",EDGE,"E1641"),sQuery(id+"F0.wireOp",EDGE,"E1642"),sQuery(id+"F0.wireOp",EDGE,"E1643"),sQuery(id+"F0.wireOp",EDGE,"E1644"),sQuery(id+"F0.wireOp",EDGE,"E1645"),sQuery(id+"F0.wireOp",EDGE,"E1646"),sQuery(id+"F0.wireOp",EDGE,"E1647"),sQuery(id+"F0.wireOp",EDGE,"E1648"),sQuery(id+"F0.wireOp",EDGE,"E1649"),sQuery(id+"F0.wireOp",EDGE,"E1650"),sQuery(id+"F0.wireOp",EDGE,"E1651"),sQuery(id+"F0.wireOp",EDGE,"E1652"),sQuery(id+"F0.wireOp",EDGE,"E1653"),sQuery(id+"F0.wireOp",EDGE,"E1654"),sQuery(id+"F0.wireOp",EDGE,"E1655"),sQuery(id+"F0.wireOp",EDGE,"E1656"),sQuery(id+"F0.wireOp",EDGE,"E1657"),sQuery(id+"F0.wireOp",EDGE,"E1658"),sQuery(id+"F0.wireOp",EDGE,"E1659"),sQuery(id+"F0.wireOp",EDGE,"E1660"),sQuery(id+"F0.wireOp",EDGE,"E1661"),sQuery(id+"F0.wireOp",EDGE,"E1662"),sQuery(id+"F0.wireOp",EDGE,"E1663"),sQuery(id+"F0.wireOp",EDGE,"E1664"),sQuery(id+"F0.wireOp",EDGE,"E1665")])],"isStart":true});
            var Q2;
            Q2=makeQuery(id+"F1.opExtrude","CAP_FACE",FACE,{"disambiguationData":[OSD([sQuery(id+"F0.wireOp",EDGE,"E1546"),sQuery(id+"F0.wireOp",EDGE,"E1547"),sQuery(id+"F0.wireOp",EDGE,"E1548"),sQuery(id+"F0.wireOp",EDGE,"E1549"),sQuery(id+"F0.wireOp",EDGE,"E1550"),sQuery(id+"F0.wireOp",EDGE,"E1551"),sQuery(id+"F0.wireOp",EDGE,"E1552"),sQuery(id+"F0.wireOp",EDGE,"E1553"),sQuery(id+"F0.wireOp",EDGE,"E1554"),sQuery(id+"F0.wireOp",EDGE,"E1555"),sQuery(id+"F0.wireOp",EDGE,"E1556"),sQuery(id+"F0.wireOp",EDGE,"E1557"),sQuery(id+"F0.wireOp",EDGE,"E1558"),sQuery(id+"F0.wireOp",EDGE,"E1559"),sQuery(id+"F0.wireOp",EDGE,"E1560"),sQuery(id+"F0.wireOp",EDGE,"E1561"),sQuery(id+"F0.wireOp",EDGE,"E1562"),sQuery(id+"F0.wireOp",EDGE,"E1563"),sQuery(id+"F0.wireOp",EDGE,"E1564"),sQuery(id+"F0.wireOp",EDGE,"E1565"),sQuery(id+"F0.wireOp",EDGE,"E1566"),sQuery(id+"F0.wireOp",EDGE,"E1567"),sQuery(id+"F0.wireOp",EDGE,"E1568"),sQuery(id+"F0.wireOp",EDGE,"E1569"),sQuery(id+"F0.wireOp",EDGE,"E1570"),sQuery(id+"F0.wireOp",EDGE,"E1571"),sQuery(id+"F0.wireOp",EDGE,"E1572"),sQuery(id+"F0.wireOp",EDGE,"E1573"),sQuery(id+"F0.wireOp",EDGE,"E1574"),sQuery(id+"F0.wireOp",EDGE,"E1575"),sQuery(id+"F0.wireOp",EDGE,"E1576"),sQuery(id+"F0.wireOp",EDGE,"E1577"),sQuery(id+"F0.wireOp",EDGE,"E1578"),sQuery(id+"F0.wireOp",EDGE,"E1579"),sQuery(id+"F0.wireOp",EDGE,"E1580"),sQuery(id+"F0.wireOp",EDGE,"E1581"),sQuery(id+"F0.wireOp",EDGE,"E1582"),sQuery(id+"F0.wireOp",EDGE,"E1583"),sQuery(id+"F0.wireOp",EDGE,"E1584"),sQuery(id+"F0.wireOp",EDGE,"E1585"),sQuery(id+"F0.wireOp",EDGE,"E1586"),sQuery(id+"F0.wireOp",EDGE,"E1587"),sQuery(id+"F0.wireOp",EDGE,"E1588"),sQuery(id+"F0.wireOp",EDGE,"E1589"),sQuery(id+"F0.wireOp",EDGE,"E1590"),sQuery(id+"F0.wireOp",EDGE,"E1591"),sQuery(id+"F0.wireOp",EDGE,"E1592"),sQuery(id+"F0.wireOp",EDGE,"E1593"),sQuery(id+"F0.wireOp",EDGE,"E1594"),sQuery(id+"F0.wireOp",EDGE,"E1595"),sQuery(id+"F0.wireOp",EDGE,"E1596"),sQuery(id+"F0.wireOp",EDGE,"E1597"),sQuery(id+"F0.wireOp",EDGE,"E1598"),sQuery(id+"F0.wireOp",EDGE,"E1599"),sQuery(id+"F0.wireOp",EDGE,"E1600"),sQuery(id+"F0.wireOp",EDGE,"E1601"),sQuery(id+"F0.wireOp",EDGE,"E1602"),sQuery(id+"F0.wireOp",EDGE,"E1603"),sQuery(id+"F0.wireOp",EDGE,"E1604"),sQuery(id+"F0.wireOp",EDGE,"E1605")])],"isStart":true});
            var Q3;
            Q3=makeQuery(id+"F1.opExtrude","CAP_FACE",FACE,{"disambiguationData":[OSD([sQuery(id+"F0.wireOp",EDGE,"E1458"),sQuery(id+"F0.wireOp",EDGE,"E1459"),sQuery(id+"F0.wireOp",EDGE,"E1460"),sQuery(id+"F0.wireOp",EDGE,"E1461"),sQuery(id+"F0.wireOp",EDGE,"E1462"),sQuery(id+"F0.wireOp",EDGE,"E1463"),sQuery(id+"F0.wireOp",EDGE,"E1464"),sQuery(id+"F0.wireOp",EDGE,"E1465"),sQuery(id+"F0.wireOp",EDGE,"E1466"),sQuery(id+"F0.wireOp",EDGE,"E1467"),sQuery(id+"F0.wireOp",EDGE,"E1468"),sQuery(id+"F0.wireOp",EDGE,"E1469"),sQuery(id+"F0.wireOp",EDGE,"E1470"),sQuery(id+"F0.wireOp",EDGE,"E1471"),sQuery(id+"F0.wireOp",EDGE,"E1472"),sQuery(id+"F0.wireOp",EDGE,"E1473"),sQuery(id+"F0.wireOp",EDGE,"E1474"),sQuery(id+"F0.wireOp",EDGE,"E1475"),sQuery(id+"F0.wireOp",EDGE,"E1476"),sQuery(id+"F0.wireOp",EDGE,"E1477"),sQuery(id+"F0.wireOp",EDGE,"E1478"),sQuery(id+"F0.wireOp",EDGE,"E1479"),sQuery(id+"F0.wireOp",EDGE,"E1480"),sQuery(id+"F0.wireOp",EDGE,"E1481"),sQuery(id+"F0.wireOp",EDGE,"E1482"),sQuery(id+"F0.wireOp",EDGE,"E1483"),sQuery(id+"F0.wireOp",EDGE,"E1484"),sQuery(id+"F0.wireOp",EDGE,"E1485"),sQuery(id+"F0.wireOp",EDGE,"E1486"),sQuery(id+"F0.wireOp",EDGE,"E1487"),sQuery(id+"F0.wireOp",EDGE,"E1488"),sQuery(id+"F0.wireOp",EDGE,"E1489"),sQuery(id+"F0.wireOp",EDGE,"E1490"),sQuery(id+"F0.wireOp",EDGE,"E1491"),sQuery(id+"F0.wireOp",EDGE,"E1492"),sQuery(id+"F0.wireOp",EDGE,"E1493"),sQuery(id+"F0.wireOp",EDGE,"E1494"),sQuery(id+"F0.wireOp",EDGE,"E1495"),sQuery(id+"F0.wireOp",EDGE,"E1496"),sQuery(id+"F0.wireOp",EDGE,"E1497"),sQuery(id+"F0.wireOp",EDGE,"E1498"),sQuery(id+"F0.wireOp",EDGE,"E1499"),sQuery(id+"F0.wireOp",EDGE,"E1500"),sQuery(id+"F0.wireOp",EDGE,"E1501"),sQuery(id+"F0.wireOp",EDGE,"E1502"),sQuery(id+"F0.wireOp",EDGE,"E1503"),sQuery(id+"F0.wireOp",EDGE,"E1504"),sQuery(id+"F0.wireOp",EDGE,"E1505"),sQuery(id+"F0.wireOp",EDGE,"E1506"),sQuery(id+"F0.wireOp",EDGE,"E1507"),sQuery(id+"F0.wireOp",EDGE,"E1508"),sQuery(id+"F0.wireOp",EDGE,"E1509"),sQuery(id+"F0.wireOp",EDGE,"E1510"),sQuery(id+"F0.wireOp",EDGE,"E1511"),sQuery(id+"F0.wireOp",EDGE,"E1512"),sQuery(id+"F0.wireOp",EDGE,"E1513"),sQuery(id+"F0.wireOp",EDGE,"E1514"),sQuery(id+"F0.wireOp",EDGE,"E1515"),sQuery(id+"F0.wireOp",EDGE,"E1516"),sQuery(id+"F0.wireOp",EDGE,"E1517"),sQuery(id+"F0.wireOp",EDGE,"E1518"),sQuery(id+"F0.wireOp",EDGE,"E1519"),sQuery(id+"F0.wireOp",EDGE,"E1520"),sQuery(id+"F0.wireOp",EDGE,"E1521"),sQuery(id+"F0.wireOp",EDGE,"E1522"),sQuery(id+"F0.wireOp",EDGE,"E1523"),sQuery(id+"F0.wireOp",EDGE,"E1524"),sQuery(id+"F0.wireOp",EDGE,"E1525"),sQuery(id+"F0.wireOp",EDGE,"E1526"),sQuery(id+"F0.wireOp",EDGE,"E1527"),sQuery(id+"F0.wireOp",EDGE,"E1528"),sQuery(id+"F0.wireOp",EDGE,"E1529"),sQuery(id+"F0.wireOp",EDGE,"E1530"),sQuery(id+"F0.wireOp",EDGE,"E1531"),sQuery(id+"F0.wireOp",EDGE,"E1532"),sQuery(id+"F0.wireOp",EDGE,"E1533"),sQuery(id+"F0.wireOp",EDGE,"E1534"),sQuery(id+"F0.wireOp",EDGE,"E1535"),sQuery(id+"F0.wireOp",EDGE,"E1536"),sQuery(id+"F0.wireOp",EDGE,"E1537"),sQuery(id+"F0.wireOp",EDGE,"E1538"),sQuery(id+"F0.wireOp",EDGE,"E1539"),sQuery(id+"F0.wireOp",EDGE,"E1540"),sQuery(id+"F0.wireOp",EDGE,"E1541"),sQuery(id+"F0.wireOp",EDGE,"E1542"),sQuery(id+"F0.wireOp",EDGE,"E1543"),sQuery(id+"F0.wireOp",EDGE,"E1544"),sQuery(id+"F0.wireOp",EDGE,"E1545")])],"isStart":true});
            var Q4;
            Q4=makeQuery(id+"F1.opExtrude","CAP_FACE",FACE,{"disambiguationData":[OSD([sQuery(id+"F0.wireOp",EDGE,"E1414"),sQuery(id+"F0.wireOp",EDGE,"E1415"),sQuery(id+"F0.wireOp",EDGE,"E1416"),sQuery(id+"F0.wireOp",EDGE,"E1417"),sQuery(id+"F0.wireOp",EDGE,"E1418"),sQuery(id+"F0.wireOp",EDGE,"E1419"),sQuery(id+"F0.wireOp",EDGE,"E1420"),sQuery(id+"F0.wireOp",EDGE,"E1421"),sQuery(id+"F0.wireOp",EDGE,"E1422"),sQuery(id+"F0.wireOp",EDGE,"E1423"),sQuery(id+"F0.wireOp",EDGE,"E1424"),sQuery(id+"F0.wireOp",EDGE,"E1425"),sQuery(id+"F0.wireOp",EDGE,"E1426"),sQuery(id+"F0.wireOp",EDGE,"E1427"),sQuery(id+"F0.wireOp",EDGE,"E1428"),sQuery(id+"F0.wireOp",EDGE,"E1429"),sQuery(id+"F0.wireOp",EDGE,"E1430"),sQuery(id+"F0.wireOp",EDGE,"E1431"),sQuery(id+"F0.wireOp",EDGE,"E1432"),sQuery(id+"F0.wireOp",EDGE,"E1433"),sQuery(id+"F0.wireOp",EDGE,"E1434"),sQuery(id+"F0.wireOp",EDGE,"E1435"),sQuery(id+"F0.wireOp",EDGE,"E1436"),sQuery(id+"F0.wireOp",EDGE,"E1437"),sQuery(id+"F0.wireOp",EDGE,"E1438"),sQuery(id+"F0.wireOp",EDGE,"E1439"),sQuery(id+"F0.wireOp",EDGE,"E1440"),sQuery(id+"F0.wireOp",EDGE,"E1441"),sQuery(id+"F0.wireOp",EDGE,"E1442"),sQuery(id+"F0.wireOp",EDGE,"E1443"),sQuery(id+"F0.wireOp",EDGE,"E1444"),sQuery(id+"F0.wireOp",EDGE,"E1445"),sQuery(id+"F0.wireOp",EDGE,"E1446"),sQuery(id+"F0.wireOp",EDGE,"E1447"),sQuery(id+"F0.wireOp",EDGE,"E1448"),sQuery(id+"F0.wireOp",EDGE,"E1449"),sQuery(id+"F0.wireOp",EDGE,"E1450"),sQuery(id+"F0.wireOp",EDGE,"E1451"),sQuery(id+"F0.wireOp",EDGE,"E1452"),sQuery(id+"F0.wireOp",EDGE,"E1453"),sQuery(id+"F0.wireOp",EDGE,"E1454"),sQuery(id+"F0.wireOp",EDGE,"E1455"),sQuery(id+"F0.wireOp",EDGE,"E1456"),sQuery(id+"F0.wireOp",EDGE,"E1457")])],"isStart":true});
            var Q5;
            Q5=makeQuery(id+"F1.opExtrude","CAP_FACE",FACE,{"disambiguationData":[OSD([sQuery(id+"F0.wireOp",EDGE,"E1354"),sQuery(id+"F0.wireOp",EDGE,"E1355"),sQuery(id+"F0.wireOp",EDGE,"E1356"),sQuery(id+"F0.wireOp",EDGE,"E1357"),sQuery(id+"F0.wireOp",EDGE,"E1358"),sQuery(id+"F0.wireOp",EDGE,"E1359"),sQuery(id+"F0.wireOp",EDGE,"E1360"),sQuery(id+"F0.wireOp",EDGE,"E1361"),sQuery(id+"F0.wireOp",EDGE,"E1362"),sQuery(id+"F0.wireOp",EDGE,"E1363"),sQuery(id+"F0.wireOp",EDGE,"E1364"),sQuery(id+"F0.wireOp",EDGE,"E1365"),sQuery(id+"F0.wireOp",EDGE,"E1366"),sQuery(id+"F0.wireOp",EDGE,"E1367"),sQuery(id+"F0.wireOp",EDGE,"E1368"),sQuery(id+"F0.wireOp",EDGE,"E1369"),sQuery(id+"F0.wireOp",EDGE,"E1370"),sQuery(id+"F0.wireOp",EDGE,"E1371"),sQuery(id+"F0.wireOp",EDGE,"E1372"),sQuery(id+"F0.wireOp",EDGE,"E1373"),sQuery(id+"F0.wireOp",EDGE,"E1374"),sQuery(id+"F0.wireOp",EDGE,"E1375"),sQuery(id+"F0.wireOp",EDGE,"E1376"),sQuery(id+"F0.wireOp",EDGE,"E1377"),sQuery(id+"F0.wireOp",EDGE,"E1378"),sQuery(id+"F0.wireOp",EDGE,"E1379"),sQuery(id+"F0.wireOp",EDGE,"E1380"),sQuery(id+"F0.wireOp",EDGE,"E1381"),sQuery(id+"F0.wireOp",EDGE,"E1382"),sQuery(id+"F0.wireOp",EDGE,"E1383"),sQuery(id+"F0.wireOp",EDGE,"E1384"),sQuery(id+"F0.wireOp",EDGE,"E1385"),sQuery(id+"F0.wireOp",EDGE,"E1386"),sQuery(id+"F0.wireOp",EDGE,"E1387"),sQuery(id+"F0.wireOp",EDGE,"E1388"),sQuery(id+"F0.wireOp",EDGE,"E1389"),sQuery(id+"F0.wireOp",EDGE,"E1390"),sQuery(id+"F0.wireOp",EDGE,"E1391"),sQuery(id+"F0.wireOp",EDGE,"E1392"),sQuery(id+"F0.wireOp",EDGE,"E1393"),sQuery(id+"F0.wireOp",EDGE,"E1394"),sQuery(id+"F0.wireOp",EDGE,"E1395"),sQuery(id+"F0.wireOp",EDGE,"E1396"),sQuery(id+"F0.wireOp",EDGE,"E1397"),sQuery(id+"F0.wireOp",EDGE,"E1398"),sQuery(id+"F0.wireOp",EDGE,"E1399"),sQuery(id+"F0.wireOp",EDGE,"E1400"),sQuery(id+"F0.wireOp",EDGE,"E1401"),sQuery(id+"F0.wireOp",EDGE,"E1402"),sQuery(id+"F0.wireOp",EDGE,"E1403"),sQuery(id+"F0.wireOp",EDGE,"E1404"),sQuery(id+"F0.wireOp",EDGE,"E1405"),sQuery(id+"F0.wireOp",EDGE,"E1406"),sQuery(id+"F0.wireOp",EDGE,"E1407"),sQuery(id+"F0.wireOp",EDGE,"E1408"),sQuery(id+"F0.wireOp",EDGE,"E1409"),sQuery(id+"F0.wireOp",EDGE,"E1410"),sQuery(id+"F0.wireOp",EDGE,"E1411"),sQuery(id+"F0.wireOp",EDGE,"E1412"),sQuery(id+"F0.wireOp",EDGE,"E1413")])],"isStart":true});
            var Q6;
            Q6=makeQuery(id+"F1.opExtrude","CAP_FACE",FACE,{"disambiguationData":[OSD([sQuery(id+"F0.wireOp",EDGE,"E1266"),sQuery(id+"F0.wireOp",EDGE,"E1267"),sQuery(id+"F0.wireOp",EDGE,"E1268"),sQuery(id+"F0.wireOp",EDGE,"E1269"),sQuery(id+"F0.wireOp",EDGE,"E1270"),sQuery(id+"F0.wireOp",EDGE,"E1271"),sQuery(id+"F0.wireOp",EDGE,"E1272"),sQuery(id+"F0.wireOp",EDGE,"E1273"),sQuery(id+"F0.wireOp",EDGE,"E1274"),sQuery(id+"F0.wireOp",EDGE,"E1275"),sQuery(id+"F0.wireOp",EDGE,"E1276"),sQuery(id+"F0.wireOp",EDGE,"E1277"),sQuery(id+"F0.wireOp",EDGE,"E1278"),sQuery(id+"F0.wireOp",EDGE,"E1279"),sQuery(id+"F0.wireOp",EDGE,"E1280"),sQuery(id+"F0.wireOp",EDGE,"E1281"),sQuery(id+"F0.wireOp",EDGE,"E1282"),sQuery(id+"F0.wireOp",EDGE,"E1283"),sQuery(id+"F0.wireOp",EDGE,"E1284"),sQuery(id+"F0.wireOp",EDGE,"E1285"),sQuery(id+"F0.wireOp",EDGE,"E1286"),sQuery(id+"F0.wireOp",EDGE,"E1287"),sQuery(id+"F0.wireOp",EDGE,"E1288"),sQuery(id+"F0.wireOp",EDGE,"E1289"),sQuery(id+"F0.wireOp",EDGE,"E1290"),sQuery(id+"F0.wireOp",EDGE,"E1291"),sQuery(id+"F0.wireOp",EDGE,"E1292"),sQuery(id+"F0.wireOp",EDGE,"E1293"),sQuery(id+"F0.wireOp",EDGE,"E1294"),sQuery(id+"F0.wireOp",EDGE,"E1295"),sQuery(id+"F0.wireOp",EDGE,"E1296"),sQuery(id+"F0.wireOp",EDGE,"E1297"),sQuery(id+"F0.wireOp",EDGE,"E1298"),sQuery(id+"F0.wireOp",EDGE,"E1299"),sQuery(id+"F0.wireOp",EDGE,"E1300"),sQuery(id+"F0.wireOp",EDGE,"E1301"),sQuery(id+"F0.wireOp",EDGE,"E1302"),sQuery(id+"F0.wireOp",EDGE,"E1303"),sQuery(id+"F0.wireOp",EDGE,"E1304"),sQuery(id+"F0.wireOp",EDGE,"E1305"),sQuery(id+"F0.wireOp",EDGE,"E1306"),sQuery(id+"F0.wireOp",EDGE,"E1307"),sQuery(id+"F0.wireOp",EDGE,"E1308"),sQuery(id+"F0.wireOp",EDGE,"E1309"),sQuery(id+"F0.wireOp",EDGE,"E1310"),sQuery(id+"F0.wireOp",EDGE,"E1311"),sQuery(id+"F0.wireOp",EDGE,"E1312"),sQuery(id+"F0.wireOp",EDGE,"E1313"),sQuery(id+"F0.wireOp",EDGE,"E1314"),sQuery(id+"F0.wireOp",EDGE,"E1315"),sQuery(id+"F0.wireOp",EDGE,"E1316"),sQuery(id+"F0.wireOp",EDGE,"E1317"),sQuery(id+"F0.wireOp",EDGE,"E1318"),sQuery(id+"F0.wireOp",EDGE,"E1319"),sQuery(id+"F0.wireOp",EDGE,"E1320"),sQuery(id+"F0.wireOp",EDGE,"E1321"),sQuery(id+"F0.wireOp",EDGE,"E1322"),sQuery(id+"F0.wireOp",EDGE,"E1323"),sQuery(id+"F0.wireOp",EDGE,"E1324"),sQuery(id+"F0.wireOp",EDGE,"E1325"),sQuery(id+"F0.wireOp",EDGE,"E1326"),sQuery(id+"F0.wireOp",EDGE,"E1327"),sQuery(id+"F0.wireOp",EDGE,"E1328"),sQuery(id+"F0.wireOp",EDGE,"E1329"),sQuery(id+"F0.wireOp",EDGE,"E1330"),sQuery(id+"F0.wireOp",EDGE,"E1331"),sQuery(id+"F0.wireOp",EDGE,"E1332"),sQuery(id+"F0.wireOp",EDGE,"E1333"),sQuery(id+"F0.wireOp",EDGE,"E1334"),sQuery(id+"F0.wireOp",EDGE,"E1335"),sQuery(id+"F0.wireOp",EDGE,"E1336"),sQuery(id+"F0.wireOp",EDGE,"E1337"),sQuery(id+"F0.wireOp",EDGE,"E1338"),sQuery(id+"F0.wireOp",EDGE,"E1339"),sQuery(id+"F0.wireOp",EDGE,"E1340"),sQuery(id+"F0.wireOp",EDGE,"E1341"),sQuery(id+"F0.wireOp",EDGE,"E1342"),sQuery(id+"F0.wireOp",EDGE,"E1343"),sQuery(id+"F0.wireOp",EDGE,"E1344"),sQuery(id+"F0.wireOp",EDGE,"E1345"),sQuery(id+"F0.wireOp",EDGE,"E1346"),sQuery(id+"F0.wireOp",EDGE,"E1347"),sQuery(id+"F0.wireOp",EDGE,"E1348"),sQuery(id+"F0.wireOp",EDGE,"E1349"),sQuery(id+"F0.wireOp",EDGE,"E1350"),sQuery(id+"F0.wireOp",EDGE,"E1351"),sQuery(id+"F0.wireOp",EDGE,"E1352"),sQuery(id+"F0.wireOp",EDGE,"E1353")])],"isStart":true});
            var Q7;
            Q7=makeQuery(id+"F1.opExtrude","CAP_FACE",FACE,{"disambiguationData":[OSD([sQuery(id+"F0.wireOp",EDGE,"E1206"),sQuery(id+"F0.wireOp",EDGE,"E1207"),sQuery(id+"F0.wireOp",EDGE,"E1208"),sQuery(id+"F0.wireOp",EDGE,"E1209"),sQuery(id+"F0.wireOp",EDGE,"E1210"),sQuery(id+"F0.wireOp",EDGE,"E1211"),sQuery(id+"F0.wireOp",EDGE,"E1212"),sQuery(id+"F0.wireOp",EDGE,"E1213"),sQuery(id+"F0.wireOp",EDGE,"E1214"),sQuery(id+"F0.wireOp",EDGE,"E1215"),sQuery(id+"F0.wireOp",EDGE,"E1216"),sQuery(id+"F0.wireOp",EDGE,"E1217"),sQuery(id+"F0.wireOp",EDGE,"E1218"),sQuery(id+"F0.wireOp",EDGE,"E1219"),sQuery(id+"F0.wireOp",EDGE,"E1220"),sQuery(id+"F0.wireOp",EDGE,"E1221"),sQuery(id+"F0.wireOp",EDGE,"E1222"),sQuery(id+"F0.wireOp",EDGE,"E1223"),sQuery(id+"F0.wireOp",EDGE,"E1224"),sQuery(id+"F0.wireOp",EDGE,"E1225"),sQuery(id+"F0.wireOp",EDGE,"E1226"),sQuery(id+"F0.wireOp",EDGE,"E1227"),sQuery(id+"F0.wireOp",EDGE,"E1228"),sQuery(id+"F0.wireOp",EDGE,"E1229"),sQuery(id+"F0.wireOp",EDGE,"E1230"),sQuery(id+"F0.wireOp",EDGE,"E1231"),sQuery(id+"F0.wireOp",EDGE,"E1232"),sQuery(id+"F0.wireOp",EDGE,"E1233"),sQuery(id+"F0.wireOp",EDGE,"E1234"),sQuery(id+"F0.wireOp",EDGE,"E1235"),sQuery(id+"F0.wireOp",EDGE,"E1236"),sQuery(id+"F0.wireOp",EDGE,"E1237"),sQuery(id+"F0.wireOp",EDGE,"E1238"),sQuery(id+"F0.wireOp",EDGE,"E1239"),sQuery(id+"F0.wireOp",EDGE,"E1240"),sQuery(id+"F0.wireOp",EDGE,"E1241"),sQuery(id+"F0.wireOp",EDGE,"E1242"),sQuery(id+"F0.wireOp",EDGE,"E1243"),sQuery(id+"F0.wireOp",EDGE,"E1244"),sQuery(id+"F0.wireOp",EDGE,"E1245"),sQuery(id+"F0.wireOp",EDGE,"E1246"),sQuery(id+"F0.wireOp",EDGE,"E1247"),sQuery(id+"F0.wireOp",EDGE,"E1248"),sQuery(id+"F0.wireOp",EDGE,"E1249"),sQuery(id+"F0.wireOp",EDGE,"E1250"),sQuery(id+"F0.wireOp",EDGE,"E1251"),sQuery(id+"F0.wireOp",EDGE,"E1252"),sQuery(id+"F0.wireOp",EDGE,"E1253"),sQuery(id+"F0.wireOp",EDGE,"E1254"),sQuery(id+"F0.wireOp",EDGE,"E1255"),sQuery(id+"F0.wireOp",EDGE,"E1256"),sQuery(id+"F0.wireOp",EDGE,"E1257"),sQuery(id+"F0.wireOp",EDGE,"E1258"),sQuery(id+"F0.wireOp",EDGE,"E1259"),sQuery(id+"F0.wireOp",EDGE,"E1260"),sQuery(id+"F0.wireOp",EDGE,"E1261"),sQuery(id+"F0.wireOp",EDGE,"E1262"),sQuery(id+"F0.wireOp",EDGE,"E1263"),sQuery(id+"F0.wireOp",EDGE,"E1264"),sQuery(id+"F0.wireOp",EDGE,"E1265")])],"isStart":true});
            var Q8;
            Q8=makeQuery(id+"F1.opExtrude","CAP_FACE",FACE,{"disambiguationData":[OSD([sQuery(id+"F0.wireOp",EDGE,"E1146"),sQuery(id+"F0.wireOp",EDGE,"E1147"),sQuery(id+"F0.wireOp",EDGE,"E1148"),sQuery(id+"F0.wireOp",EDGE,"E1149"),sQuery(id+"F0.wireOp",EDGE,"E1150"),sQuery(id+"F0.wireOp",EDGE,"E1151"),sQuery(id+"F0.wireOp",EDGE,"E1152"),sQuery(id+"F0.wireOp",EDGE,"E1153"),sQuery(id+"F0.wireOp",EDGE,"E1154"),sQuery(id+"F0.wireOp",EDGE,"E1155"),sQuery(id+"F0.wireOp",EDGE,"E1156"),sQuery(id+"F0.wireOp",EDGE,"E1157"),sQuery(id+"F0.wireOp",EDGE,"E1158"),sQuery(id+"F0.wireOp",EDGE,"E1159"),sQuery(id+"F0.wireOp",EDGE,"E1160"),sQuery(id+"F0.wireOp",EDGE,"E1161"),sQuery(id+"F0.wireOp",EDGE,"E1162"),sQuery(id+"F0.wireOp",EDGE,"E1163"),sQuery(id+"F0.wireOp",EDGE,"E1164"),sQuery(id+"F0.wireOp",EDGE,"E1165"),sQuery(id+"F0.wireOp",EDGE,"E1166"),sQuery(id+"F0.wireOp",EDGE,"E1167"),sQuery(id+"F0.wireOp",EDGE,"E1168"),sQuery(id+"F0.wireOp",EDGE,"E1169"),sQuery(id+"F0.wireOp",EDGE,"E1170"),sQuery(id+"F0.wireOp",EDGE,"E1171"),sQuery(id+"F0.wireOp",EDGE,"E1172"),sQuery(id+"F0.wireOp",EDGE,"E1173"),sQuery(id+"F0.wireOp",EDGE,"E1174"),sQuery(id+"F0.wireOp",EDGE,"E1175"),sQuery(id+"F0.wireOp",EDGE,"E1176"),sQuery(id+"F0.wireOp",EDGE,"E1177"),sQuery(id+"F0.wireOp",EDGE,"E1178"),sQuery(id+"F0.wireOp",EDGE,"E1179"),sQuery(id+"F0.wireOp",EDGE,"E1180"),sQuery(id+"F0.wireOp",EDGE,"E1181"),sQuery(id+"F0.wireOp",EDGE,"E1182"),sQuery(id+"F0.wireOp",EDGE,"E1183"),sQuery(id+"F0.wireOp",EDGE,"E1184"),sQuery(id+"F0.wireOp",EDGE,"E1185"),sQuery(id+"F0.wireOp",EDGE,"E1186"),sQuery(id+"F0.wireOp",EDGE,"E1187"),sQuery(id+"F0.wireOp",EDGE,"E1188"),sQuery(id+"F0.wireOp",EDGE,"E1189"),sQuery(id+"F0.wireOp",EDGE,"E1190"),sQuery(id+"F0.wireOp",EDGE,"E1191"),sQuery(id+"F0.wireOp",EDGE,"E1192"),sQuery(id+"F0.wireOp",EDGE,"E1193"),sQuery(id+"F0.wireOp",EDGE,"E1194"),sQuery(id+"F0.wireOp",EDGE,"E1195"),sQuery(id+"F0.wireOp",EDGE,"E1196"),sQuery(id+"F0.wireOp",EDGE,"E1197"),sQuery(id+"F0.wireOp",EDGE,"E1198"),sQuery(id+"F0.wireOp",EDGE,"E1199"),sQuery(id+"F0.wireOp",EDGE,"E1200"),sQuery(id+"F0.wireOp",EDGE,"E1201"),sQuery(id+"F0.wireOp",EDGE,"E1202"),sQuery(id+"F0.wireOp",EDGE,"E1203"),sQuery(id+"F0.wireOp",EDGE,"E1204"),sQuery(id+"F0.wireOp",EDGE,"E1205")])],"isStart":true});
            var Q9;
            Q9=makeQuery(id+"F1.opExtrude","CAP_FACE",FACE,{"disambiguationData":[OSD([sQuery(id+"F0.wireOp",EDGE,"E1080"),sQuery(id+"F0.wireOp",EDGE,"E1081"),sQuery(id+"F0.wireOp",EDGE,"E1082"),sQuery(id+"F0.wireOp",EDGE,"E1083"),sQuery(id+"F0.wireOp",EDGE,"E1084"),sQuery(id+"F0.wireOp",EDGE,"E1085"),sQuery(id+"F0.wireOp",EDGE,"E1086"),sQuery(id+"F0.wireOp",EDGE,"E1087"),sQuery(id+"F0.wireOp",EDGE,"E1088"),sQuery(id+"F0.wireOp",EDGE,"E1089"),sQuery(id+"F0.wireOp",EDGE,"E1090"),sQuery(id+"F0.wireOp",EDGE,"E1091"),sQuery(id+"F0.wireOp",EDGE,"E1092"),sQuery(id+"F0.wireOp",EDGE,"E1093"),sQuery(id+"F0.wireOp",EDGE,"E1094"),sQuery(id+"F0.wireOp",EDGE,"E1095"),sQuery(id+"F0.wireOp",EDGE,"E1096"),sQuery(id+"F0.wireOp",EDGE,"E1097"),sQuery(id+"F0.wireOp",EDGE,"E1098"),sQuery(id+"F0.wireOp",EDGE,"E1099"),sQuery(id+"F0.wireOp",EDGE,"E1100"),sQuery(id+"F0.wireOp",EDGE,"E1101"),sQuery(id+"F0.wireOp",EDGE,"E1102"),sQuery(id+"F0.wireOp",EDGE,"E1103"),sQuery(id+"F0.wireOp",EDGE,"E1104"),sQuery(id+"F0.wireOp",EDGE,"E1105"),sQuery(id+"F0.wireOp",EDGE,"E1106"),sQuery(id+"F0.wireOp",EDGE,"E1107"),sQuery(id+"F0.wireOp",EDGE,"E1108"),sQuery(id+"F0.wireOp",EDGE,"E1109"),sQuery(id+"F0.wireOp",EDGE,"E1110"),sQuery(id+"F0.wireOp",EDGE,"E1111"),sQuery(id+"F0.wireOp",EDGE,"E1112"),sQuery(id+"F0.wireOp",EDGE,"E1113"),sQuery(id+"F0.wireOp",EDGE,"E1114"),sQuery(id+"F0.wireOp",EDGE,"E1115"),sQuery(id+"F0.wireOp",EDGE,"E1116"),sQuery(id+"F0.wireOp",EDGE,"E1117"),sQuery(id+"F0.wireOp",EDGE,"E1118"),sQuery(id+"F0.wireOp",EDGE,"E1119"),sQuery(id+"F0.wireOp",EDGE,"E1120"),sQuery(id+"F0.wireOp",EDGE,"E1121"),sQuery(id+"F0.wireOp",EDGE,"E1122"),sQuery(id+"F0.wireOp",EDGE,"E1123"),sQuery(id+"F0.wireOp",EDGE,"E1124"),sQuery(id+"F0.wireOp",EDGE,"E1125"),sQuery(id+"F0.wireOp",EDGE,"E1126"),sQuery(id+"F0.wireOp",EDGE,"E1127"),sQuery(id+"F0.wireOp",EDGE,"E1128"),sQuery(id+"F0.wireOp",EDGE,"E1129"),sQuery(id+"F0.wireOp",EDGE,"E1130"),sQuery(id+"F0.wireOp",EDGE,"E1131"),sQuery(id+"F0.wireOp",EDGE,"E1132"),sQuery(id+"F0.wireOp",EDGE,"E1133"),sQuery(id+"F0.wireOp",EDGE,"E1134"),sQuery(id+"F0.wireOp",EDGE,"E1135"),sQuery(id+"F0.wireOp",EDGE,"E1136"),sQuery(id+"F0.wireOp",EDGE,"E1137"),sQuery(id+"F0.wireOp",EDGE,"E1138"),sQuery(id+"F0.wireOp",EDGE,"E1139"),sQuery(id+"F0.wireOp",EDGE,"E1140"),sQuery(id+"F0.wireOp",EDGE,"E1141"),sQuery(id+"F0.wireOp",EDGE,"E1142"),sQuery(id+"F0.wireOp",EDGE,"E1143"),sQuery(id+"F0.wireOp",EDGE,"E1144"),sQuery(id+"F0.wireOp",EDGE,"E1145")])],"isStart":true});
            var Q10;
            Q10=makeQuery(id+"F1.opExtrude","CAP_FACE",FACE,{"disambiguationData":[OSD([sQuery(id+"F0.wireOp",EDGE,"E924"),sQuery(id+"F0.wireOp",EDGE,"E925"),sQuery(id+"F0.wireOp",EDGE,"E926"),sQuery(id+"F0.wireOp",EDGE,"E927"),sQuery(id+"F0.wireOp",EDGE,"E928"),sQuery(id+"F0.wireOp",EDGE,"E929"),sQuery(id+"F0.wireOp",EDGE,"E930"),sQuery(id+"F0.wireOp",EDGE,"E931"),sQuery(id+"F0.wireOp",EDGE,"E932"),sQuery(id+"F0.wireOp",EDGE,"E933"),sQuery(id+"F0.wireOp",EDGE,"E934"),sQuery(id+"F0.wireOp",EDGE,"E935"),sQuery(id+"F0.wireOp",EDGE,"E936"),sQuery(id+"F0.wireOp",EDGE,"E937"),sQuery(id+"F0.wireOp",EDGE,"E938"),sQuery(id+"F0.wireOp",EDGE,"E939"),sQuery(id+"F0.wireOp",EDGE,"E940"),sQuery(id+"F0.wireOp",EDGE,"E941"),sQuery(id+"F0.wireOp",EDGE,"E942"),sQuery(id+"F0.wireOp",EDGE,"E943"),sQuery(id+"F0.wireOp",EDGE,"E944"),sQuery(id+"F0.wireOp",EDGE,"E945"),sQuery(id+"F0.wireOp",EDGE,"E946"),sQuery(id+"F0.wireOp",EDGE,"E947"),sQuery(id+"F0.wireOp",EDGE,"E948"),sQuery(id+"F0.wireOp",EDGE,"E949"),sQuery(id+"F0.wireOp",EDGE,"E950"),sQuery(id+"F0.wireOp",EDGE,"E951"),sQuery(id+"F0.wireOp",EDGE,"E952"),sQuery(id+"F0.wireOp",EDGE,"E953"),sQuery(id+"F0.wireOp",EDGE,"E954"),sQuery(id+"F0.wireOp",EDGE,"E955"),sQuery(id+"F0.wireOp",EDGE,"E956"),sQuery(id+"F0.wireOp",EDGE,"E957"),sQuery(id+"F0.wireOp",EDGE,"E958"),sQuery(id+"F0.wireOp",EDGE,"E959"),sQuery(id+"F0.wireOp",EDGE,"E960"),sQuery(id+"F0.wireOp",EDGE,"E961"),sQuery(id+"F0.wireOp",EDGE,"E962"),sQuery(id+"F0.wireOp",EDGE,"E963"),sQuery(id+"F0.wireOp",EDGE,"E964"),sQuery(id+"F0.wireOp",EDGE,"E965"),sQuery(id+"F0.wireOp",EDGE,"E966"),sQuery(id+"F0.wireOp",EDGE,"E967"),sQuery(id+"F0.wireOp",EDGE,"E968"),sQuery(id+"F0.wireOp",EDGE,"E969"),sQuery(id+"F0.wireOp",EDGE,"E970"),sQuery(id+"F0.wireOp",EDGE,"E971"),sQuery(id+"F0.wireOp",EDGE,"E972"),sQuery(id+"F0.wireOp",EDGE,"E973"),sQuery(id+"F0.wireOp",EDGE,"E974"),sQuery(id+"F0.wireOp",EDGE,"E975"),sQuery(id+"F0.wireOp",EDGE,"E976"),sQuery(id+"F0.wireOp",EDGE,"E977"),sQuery(id+"F0.wireOp",EDGE,"E978"),sQuery(id+"F0.wireOp",EDGE,"E979"),sQuery(id+"F0.wireOp",EDGE,"E980"),sQuery(id+"F0.wireOp",EDGE,"E981"),sQuery(id+"F0.wireOp",EDGE,"E982"),sQuery(id+"F0.wireOp",EDGE,"E983"),sQuery(id+"F0.wireOp",EDGE,"E984"),sQuery(id+"F0.wireOp",EDGE,"E985"),sQuery(id+"F0.wireOp",EDGE,"E986"),sQuery(id+"F0.wireOp",EDGE,"E987"),sQuery(id+"F0.wireOp",EDGE,"E988"),sQuery(id+"F0.wireOp",EDGE,"E989"),sQuery(id+"F0.wireOp",EDGE,"E990"),sQuery(id+"F0.wireOp",EDGE,"E991"),sQuery(id+"F0.wireOp",EDGE,"E992"),sQuery(id+"F0.wireOp",EDGE,"E993"),sQuery(id+"F0.wireOp",EDGE,"E994"),sQuery(id+"F0.wireOp",EDGE,"E995"),sQuery(id+"F0.wireOp",EDGE,"E996"),sQuery(id+"F0.wireOp",EDGE,"E997"),sQuery(id+"F0.wireOp",EDGE,"E998"),sQuery(id+"F0.wireOp",EDGE,"E999"),sQuery(id+"F0.wireOp",EDGE,"E1000"),sQuery(id+"F0.wireOp",EDGE,"E1001"),sQuery(id+"F0.wireOp",EDGE,"E1002"),sQuery(id+"F0.wireOp",EDGE,"E1003"),sQuery(id+"F0.wireOp",EDGE,"E1004"),sQuery(id+"F0.wireOp",EDGE,"E1005"),sQuery(id+"F0.wireOp",EDGE,"E1006"),sQuery(id+"F0.wireOp",EDGE,"E1007"),sQuery(id+"F0.wireOp",EDGE,"E1008"),sQuery(id+"F0.wireOp",EDGE,"E1009"),sQuery(id+"F0.wireOp",EDGE,"E1010"),sQuery(id+"F0.wireOp",EDGE,"E1011"),sQuery(id+"F0.wireOp",EDGE,"E1012"),sQuery(id+"F0.wireOp",EDGE,"E1013"),sQuery(id+"F0.wireOp",EDGE,"E1014"),sQuery(id+"F0.wireOp",EDGE,"E1015"),sQuery(id+"F0.wireOp",EDGE,"E1016"),sQuery(id+"F0.wireOp",EDGE,"E1017"),sQuery(id+"F0.wireOp",EDGE,"E1018"),sQuery(id+"F0.wireOp",EDGE,"E1019"),sQuery(id+"F0.wireOp",EDGE,"E1020"),sQuery(id+"F0.wireOp",EDGE,"E1021"),sQuery(id+"F0.wireOp",EDGE,"E1022"),sQuery(id+"F0.wireOp",EDGE,"E1023"),sQuery(id+"F0.wireOp",EDGE,"E1024"),sQuery(id+"F0.wireOp",EDGE,"E1025"),sQuery(id+"F0.wireOp",EDGE,"E1026"),sQuery(id+"F0.wireOp",EDGE,"E1027"),sQuery(id+"F0.wireOp",EDGE,"E1028"),sQuery(id+"F0.wireOp",EDGE,"E1029"),sQuery(id+"F0.wireOp",EDGE,"E1030"),sQuery(id+"F0.wireOp",EDGE,"E1031"),sQuery(id+"F0.wireOp",EDGE,"E1032"),sQuery(id+"F0.wireOp",EDGE,"E1033"),sQuery(id+"F0.wireOp",EDGE,"E1034"),sQuery(id+"F0.wireOp",EDGE,"E1035"),sQuery(id+"F0.wireOp",EDGE,"E1036"),sQuery(id+"F0.wireOp",EDGE,"E1037"),sQuery(id+"F0.wireOp",EDGE,"E1038"),sQuery(id+"F0.wireOp",EDGE,"E1039"),sQuery(id+"F0.wireOp",EDGE,"E1040"),sQuery(id+"F0.wireOp",EDGE,"E1041"),sQuery(id+"F0.wireOp",EDGE,"E1042"),sQuery(id+"F0.wireOp",EDGE,"E1043"),sQuery(id+"F0.wireOp",EDGE,"E1044"),sQuery(id+"F0.wireOp",EDGE,"E1045"),sQuery(id+"F0.wireOp",EDGE,"E1046"),sQuery(id+"F0.wireOp",EDGE,"E1047"),sQuery(id+"F0.wireOp",EDGE,"E1048"),sQuery(id+"F0.wireOp",EDGE,"E1049"),sQuery(id+"F0.wireOp",EDGE,"E1050"),sQuery(id+"F0.wireOp",EDGE,"E1051"),sQuery(id+"F0.wireOp",EDGE,"E1052"),sQuery(id+"F0.wireOp",EDGE,"E1053"),sQuery(id+"F0.wireOp",EDGE,"E1054"),sQuery(id+"F0.wireOp",EDGE,"E1055"),sQuery(id+"F0.wireOp",EDGE,"E1056"),sQuery(id+"F0.wireOp",EDGE,"E1057"),sQuery(id+"F0.wireOp",EDGE,"E1058"),sQuery(id+"F0.wireOp",EDGE,"E1059"),sQuery(id+"F0.wireOp",EDGE,"E1060"),sQuery(id+"F0.wireOp",EDGE,"E1061"),sQuery(id+"F0.wireOp",EDGE,"E1062"),sQuery(id+"F0.wireOp",EDGE,"E1063"),sQuery(id+"F0.wireOp",EDGE,"E1064"),sQuery(id+"F0.wireOp",EDGE,"E1065"),sQuery(id+"F0.wireOp",EDGE,"E1066"),sQuery(id+"F0.wireOp",EDGE,"E1067"),sQuery(id+"F0.wireOp",EDGE,"E1068"),sQuery(id+"F0.wireOp",EDGE,"E1069"),sQuery(id+"F0.wireOp",EDGE,"E1070"),sQuery(id+"F0.wireOp",EDGE,"E1071"),sQuery(id+"F0.wireOp",EDGE,"E1072"),sQuery(id+"F0.wireOp",EDGE,"E1073"),sQuery(id+"F0.wireOp",EDGE,"E1074"),sQuery(id+"F0.wireOp",EDGE,"E1075"),sQuery(id+"F0.wireOp",EDGE,"E1076"),sQuery(id+"F0.wireOp",EDGE,"E1077"),sQuery(id+"F0.wireOp",EDGE,"E1078"),sQuery(id+"F0.wireOp",EDGE,"E1079")])],"isStart":true});
            extrude(context, id + "F5", {"entities" : qUnion([Q0, Q1, Q2, Q3, Q4, Q5, Q6, Q7, Q8, Q9, Q10]), "operationType" : NewBodyOperationType.REMOVE, "oppositeDirection" : true, "depth" : 22.22 * mm, "offsetDistance" : 25.4 * mm});
        }
        {
            var Q0;
            Q0=makeQuery(id+"F5.boolean.opBoolean","COPY",FACE,{"derivedFrom":makeQuery(id+"F5.opExtrude","CAP_FACE",FACE,{"disambiguationData":[OSD([sQuery(id+"F0.wireOp",EDGE,"E1414"),sQuery(id+"F0.wireOp",EDGE,"E1415"),sQuery(id+"F0.wireOp",EDGE,"E1416"),sQuery(id+"F0.wireOp",EDGE,"E1417"),sQuery(id+"F0.wireOp",EDGE,"E1418"),sQuery(id+"F0.wireOp",EDGE,"E1419"),sQuery(id+"F0.wireOp",EDGE,"E1420"),sQuery(id+"F0.wireOp",EDGE,"E1421"),sQuery(id+"F0.wireOp",EDGE,"E1422"),sQuery(id+"F0.wireOp",EDGE,"E1423"),sQuery(id+"F0.wireOp",EDGE,"E1424"),sQuery(id+"F0.wireOp",EDGE,"E1425"),sQuery(id+"F0.wireOp",EDGE,"E1426"),sQuery(id+"F0.wireOp",EDGE,"E1427"),sQuery(id+"F0.wireOp",EDGE,"E1428"),sQuery(id+"F0.wireOp",EDGE,"E1429"),sQuery(id+"F0.wireOp",EDGE,"E1430"),sQuery(id+"F0.wireOp",EDGE,"E1431"),sQuery(id+"F0.wireOp",EDGE,"E1432"),sQuery(id+"F0.wireOp",EDGE,"E1433"),sQuery(id+"F0.wireOp",EDGE,"E1434"),sQuery(id+"F0.wireOp",EDGE,"E1435"),sQuery(id+"F0.wireOp",EDGE,"E1436"),sQuery(id+"F0.wireOp",EDGE,"E1437"),sQuery(id+"F0.wireOp",EDGE,"E1438"),sQuery(id+"F0.wireOp",EDGE,"E1439"),sQuery(id+"F0.wireOp",EDGE,"E1440"),sQuery(id+"F0.wireOp",EDGE,"E1441"),sQuery(id+"F0.wireOp",EDGE,"E1442"),sQuery(id+"F0.wireOp",EDGE,"E1443"),sQuery(id+"F0.wireOp",EDGE,"E1444"),sQuery(id+"F0.wireOp",EDGE,"E1445"),sQuery(id+"F0.wireOp",EDGE,"E1446"),sQuery(id+"F0.wireOp",EDGE,"E1447"),sQuery(id+"F0.wireOp",EDGE,"E1448"),sQuery(id+"F0.wireOp",EDGE,"E1449"),sQuery(id+"F0.wireOp",EDGE,"E1450"),sQuery(id+"F0.wireOp",EDGE,"E1451"),sQuery(id+"F0.wireOp",EDGE,"E1452"),sQuery(id+"F0.wireOp",EDGE,"E1453"),sQuery(id+"F0.wireOp",EDGE,"E1454"),sQuery(id+"F0.wireOp",EDGE,"E1455"),sQuery(id+"F0.wireOp",EDGE,"E1456"),sQuery(id+"F0.wireOp",EDGE,"E1457")])],"isStart":false})});
            var sketch = newSketch(context, id + "F6", { "sketchPlane" : qUnion([Q0])});
            skCircle(sketch, "E1733", {"center": v(-349.37, -176.24) * mm, "radius": 1.59 * mm});
            skCircle(sketch, "E1734", {"center": v(-301.34, -185.92) * mm, "radius": 1.59 * mm});
            skCircle(sketch, "E1735", {"center": v(-270.82, -185.84) * mm, "radius": 1.59 * mm});
            skCircle(sketch, "E1736", {"center": v(-200.13, -173.7) * mm, "radius": 1.59 * mm});
            skCircle(sketch, "E1737", {"center": v(-147.97, -179.86) * mm, "radius": 1.59 * mm});
            skCircle(sketch, "E1738", {"center": v(-127.83, -179.65) * mm, "radius": 1.59 * mm});
            skCircle(sketch, "E1739", {"center": v(-76.9, -176.24) * mm, "radius": 1.59 * mm});
            skCircle(sketch, "E1740", {"center": v(1.15, -174.07) * mm, "radius": 1.59 * mm});
            skCircle(sketch, "E1741", {"center": v(52.36, -179.57) * mm, "radius": 1.59 * mm});
            skCircle(sketch, "E1742", {"center": v(72.5, -179.36) * mm, "radius": 1.59 * mm});
            skCircle(sketch, "E1743", {"center": v(136.66, -175.15) * mm, "radius": 1.59 * mm});
            skCircle(sketch, "E1744", {"center": v(200.24, -186.78) * mm, "radius": 1.59 * mm});
            skCircle(sketch, "E1745", {"center": v(230.76, -186.7) * mm, "radius": 1.59 * mm});
            skCircle(sketch, "E1746", {"center": v(288.06, -181.3) * mm, "radius": 1.59 * mm});
            skCircle(sketch, "E1747", {"center": v(350.94, -173.7) * mm, "radius": 1.59 * mm});
            skSolve(sketch);
        }
        {
            var Q0;
            Q0 = qSketchRegion(id + "F6", true);
            extrude(context, id + "F7", {"entities" : qUnion([Q0]), "operationType" : NewBodyOperationType.ADD, "depth" : 98.42 * mm, "offsetDistance" : 25.4 * mm});
        }
        {
            var Q0;
            Q0=makeQuery(id+"F4.opExtrude","CAP_FACE",FACE,{"disambiguationData":[OSD([sQuery(id+"F3.wireOp",EDGE,"E1729")])],"isStart":false});
            var sketch = newSketch(context, id + "F8", { "sketchPlane" : qUnion([Q0])});
            skLineSegment(sketch, "E1748.bottom", {"start": v(-916.54, 224.3) * mm, "end": v(912.26, 224.3) * mm});
            skLineSegment(sketch, "E1748.top", {"start": v(-916.54, -220.2) * mm, "end": v(912.26, -220.2) * mm});
            skLineSegment(sketch, "E1748.left", {"start": v(-916.54, 224.3) * mm, "end": v(-916.54, -220.2) * mm});
            skLineSegment(sketch, "E1748.right", {"start": v(912.26, 224.3) * mm, "end": v(912.26, -220.2) * mm});
            skSolve(sketch);
        }
        {
            var Q0;
            Q0=makeQuery(id+"F8.imprint","IMPRINT",FACE,{"disambiguationData":[TD([[makeQuery(id+"F8.imprint","IMPRINT",EDGE,{"derivedFrom":sQuery(id+"F8.wireOp",EDGE,"E1748.bottom")}),-1.0]])]});
            var Q1;
            Q1=makeQuery(id+"F8.imprint","IMPRINT",FACE,{"disambiguationData":[TD([[makeQuery(id+"F8.imprint","IMPRINT",EDGE,{"derivedFrom":makeQuery(id+"F4.opExtrude","CAP_EDGE",EDGE,{"disambiguationData":[OSD([sQuery(id+"F3.wireOp",EDGE,"E1727")])],"isStart":true})}),1.0]])]});
            var Q2;
            Q2=makeQuery(id+"F8.imprint","IMPRINT",FACE,{"disambiguationData":[TD([[makeQuery(id+"F8.imprint","IMPRINT",EDGE,{"derivedFrom":makeQuery(id+"F4.opExtrude","CAP_EDGE",EDGE,{"disambiguationData":[OSD([sQuery(id+"F3.wireOp",EDGE,"E1729")])],"isStart":false})}),1.0]])]});
            extrude(context, id + "F9", {"entities" : qUnion([Q0, Q1, Q2]), "depth" : 3.17 * mm, "offsetDistance" : 25.4 * mm});
        }
        {
            var Q0;
            Q0=makeQuery(id+"F9.opExtrude","CAP_FACE",FACE,{"disambiguationData":[OSD([sQuery(id+"F8.wireOp",EDGE,"E1748.bottom"),sQuery(id+"F8.wireOp",EDGE,"E1748.top"),sQuery(id+"F8.wireOp",EDGE,"E1748.left"),sQuery(id+"F8.wireOp",EDGE,"E1748.right")])],"isStart":false});
            var sketch = newSketch(context, id + "F10", { "sketchPlane" : qUnion([Q0])});
            skLineSegment(sketch, "E1749.bottom", {"start": v(-913.36, 221.12) * mm, "end": v(909.09, 221.12) * mm});
            skLineSegment(sketch, "E1749.top", {"start": v(-913.36, -217.03) * mm, "end": v(909.09, -217.03) * mm});
            skLineSegment(sketch, "E1749.left", {"start": v(-913.36, 221.12) * mm, "end": v(-913.36, -217.03) * mm});
            skLineSegment(sketch, "E1749.right", {"start": v(909.09, 221.12) * mm, "end": v(909.09, -217.03) * mm});
            skSolve(sketch);
        }
        {
            var Q0;
            Q0=makeQuery(id+"F10.imprint","IMPRINT",FACE,{"disambiguationData":[TD([[makeQuery(id+"F10.imprint","IMPRINT",EDGE,{"derivedFrom":sQuery(id+"F10.wireOp",EDGE,"E1749.bottom")}),1.0]])]});
            extrude(context, id + "F11", {"entities" : qUnion([Q0]), "operationType" : NewBodyOperationType.ADD, "depth" : 50.8 * mm, "offsetDistance" : 25.4 * mm});
        }
        {
            var Q0;
            {var subQ0=sQuery(id+"F8.wireOp",EDGE,"E1748.bottom");Q0=makeQuery(id+"F11.boolean.opBoolean","MERGE",FACE,{"derivedFrom":[makeQuery(id+"F9.opExtrude","SWEPT_FACE",FACE,{"disambiguationData":[OSD([subQ0])]}),makeQuery(id+"F11.opExtrude","SWEPT_FACE",FACE,{"disambiguationData":[OSD([subQ0])]})]});}
            var sketch = newSketch(context, id + "F12", { "sketchPlane" : qUnion([Q0])});
            skLineSegment(sketch, "E1750.bottom", {"start": v(-239.16, 130.18) * mm, "end": v(268.84, 130.18) * mm});
            skLineSegment(sketch, "E1750.top", {"start": v(-239.16, 111.13) * mm, "end": v(268.84, 111.13) * mm});
            skLineSegment(sketch, "E1750.left", {"start": v(-239.16, 130.18) * mm, "end": v(-239.16, 111.13) * mm});
            skLineSegment(sketch, "E1750.right", {"start": v(268.84, 130.18) * mm, "end": v(268.84, 111.13) * mm});
            skSolve(sketch);
        }
        {
            var Q0;
            Q0 = qSketchRegion(id + "F12", true);
            extrude(context, id + "F13", {"entities" : qUnion([Q0]), "operationType" : NewBodyOperationType.REMOVE, "endBound" : BoundingType.THROUGH_ALL, "oppositeDirection" : true, "depth" : 25.4 * mm, "offsetDistance" : 25.4 * mm});
        }
        {
            var Q0;
            {var subQ0=sQuery(id+"F8.wireOp",EDGE,"E1748.right");Q0=makeQuery(id+"F11.boolean.opBoolean","MERGE",FACE,{"derivedFrom":[makeQuery(id+"F9.opExtrude","SWEPT_FACE",FACE,{"disambiguationData":[OSD([subQ0])]}),makeQuery(id+"F11.opExtrude","SWEPT_FACE",FACE,{"disambiguationData":[OSD([subQ0])]})]});}
            var sketch = newSketch(context, id + "F14", { "sketchPlane" : qUnion([Q0])});
            skCircle(sketch, "E1751", {"center": v(-103.19, 210.63) * mm, "radius": 3.18 * mm});
            skPoint(sketch, "E1751.centerSnap0", {"position": v(-103.19, 224.3) * mm});
            skCircle(sketch, "E1752", {"center": v(-103.19, -208.55) * mm, "radius": 3.18 * mm});
            skSolve(sketch);
        }
        {
            var Q0;
            Q0 = qSketchRegion(id + "F14", true);
            extrude(context, id + "F15", {"entities" : qUnion([Q0]), "operationType" : NewBodyOperationType.REMOVE, "oppositeDirection" : true, "depth" : 25.4 * mm, "offsetDistance" : 25.4 * mm});
        }
    });
